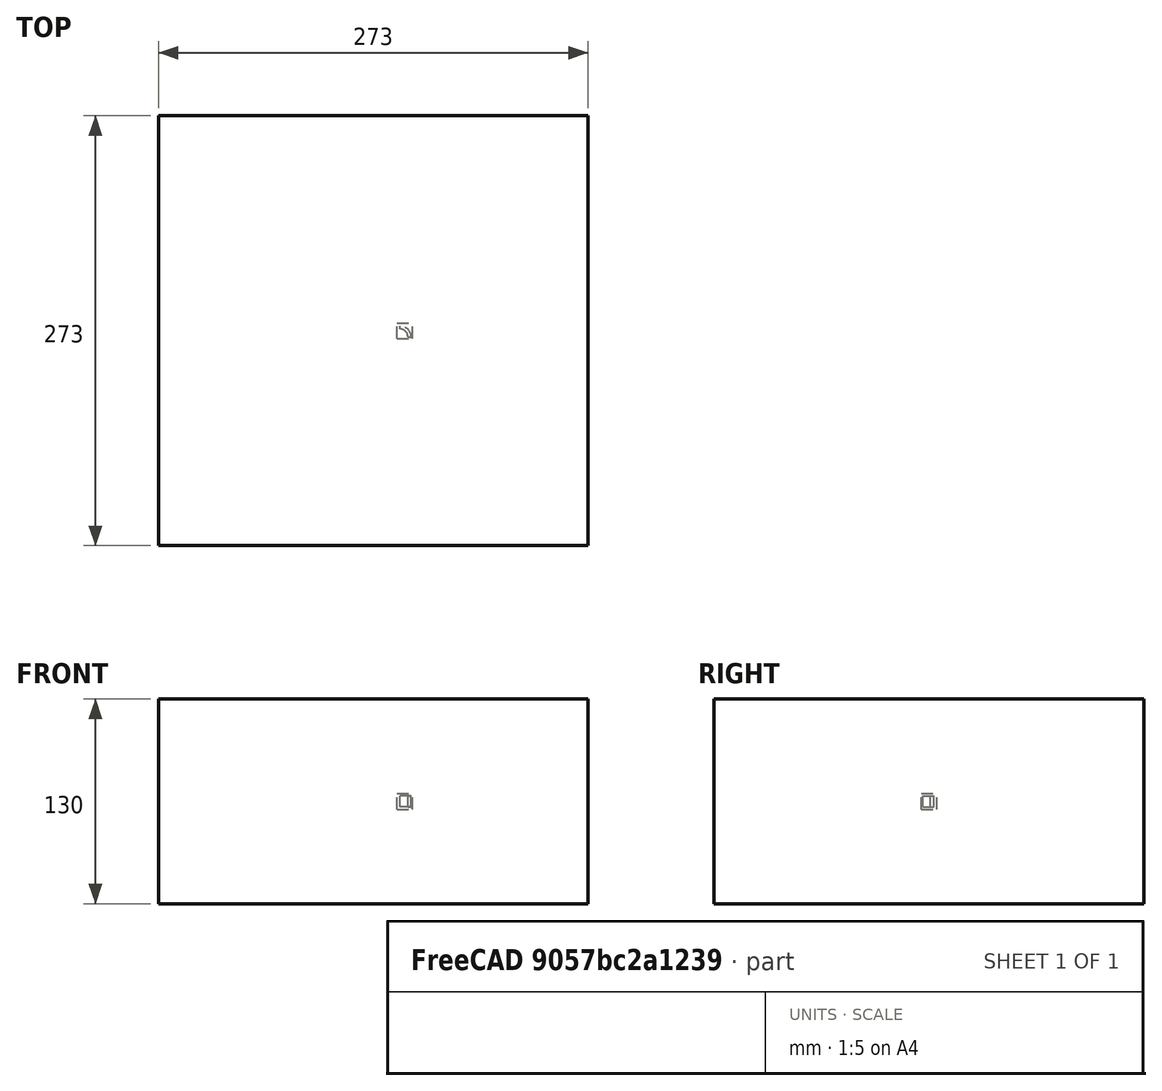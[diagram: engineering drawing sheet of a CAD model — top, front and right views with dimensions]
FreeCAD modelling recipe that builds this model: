
FCSTD DOCUMENT  (FreeCAD 1.0R39109 (Git))
Label: polarArray-of-Part-base-xformed
License: All rights reserved
LicenseURL: http://en.wikipedia.org/wiki/All_rights_reserved
objects: App::DocumentObjectGroupPython×1251, Part::FeaturePython×4, App::Part×4
note: 3 computed .brp shape members not serialized (recipe doc carries the construction recipe); baked Part::Feature solids carry a one-line shape summary decoded from their .brp

FEATURE [App::DocumentObjectGroupPython] HALFPI  # scripted group (container) (typed FeaturePython)
  name = HALFPI
  value = pi/2.
FEATURE [App::DocumentObjectGroupPython] PI  # scripted group (container) (typed FeaturePython)
  name = PI
  value = 1.*pi
FEATURE [App::DocumentObjectGroupPython] TWOPI  # scripted group (container) (typed FeaturePython)
  name = TWOPI
  value = 2.*pi
FEATURE [App::DocumentObjectGroupPython] Constants  # scripted group (container) (typed FeaturePython)
  Group = -> [HALFPI,PI,TWOPI]
FEATURE [App::DocumentObjectGroupPython] Variables  # scripted group (container) (typed FeaturePython)
FEATURE [App::DocumentObjectGroupPython] Quantities  # scripted group (container) (typed FeaturePython)
FEATURE [App::DocumentObjectGroupPython] Isotopes  # scripted group (container) (typed FeaturePython)
FEATURE [App::DocumentObjectGroupPython] Elements  # scripted group (container) (typed FeaturePython)
FEATURE [App::DocumentObjectGroupPython] Matrix  # scripted group (container) (typed FeaturePython)
FEATURE [App::DocumentObjectGroupPython] Surfaces  # scripted group (container) (typed FeaturePython)
FEATURE [App::DocumentObjectGroupPython] Opticals  # scripted group (container) (typed FeaturePython)
  Group = -> [Matrix,Surfaces]
FEATURE [App::DocumentObjectGroupPython] G4Isotopes  # scripted group (container) (typed FeaturePython)
FEATURE [App::DocumentObjectGroupPython] H_element  # scripted group (container) (typed FeaturePython)
  Z = 1
  atom_value = 1.008
  formula = H
  name = H_element
FEATURE [App::DocumentObjectGroupPython] He_element  # scripted group (container) (typed FeaturePython)
  Z = 2
  atom_value = 4.0026
  formula = He
  name = He_element
FEATURE [App::DocumentObjectGroupPython] Li_element  # scripted group (container) (typed FeaturePython)
  Z = 3
  atom_value = 6.94
  formula = Li
  name = Li_element
FEATURE [App::DocumentObjectGroupPython] Be_element  # scripted group (container) (typed FeaturePython)
  Z = 4
  atom_value = 9.01218
  formula = Be
  name = Be_element
FEATURE [App::DocumentObjectGroupPython] B_element  # scripted group (container) (typed FeaturePython)
  Z = 5
  atom_value = 10.81
  formula = B
  name = B_element
FEATURE [App::DocumentObjectGroupPython] C_element  # scripted group (container) (typed FeaturePython)
  Z = 6
  atom_value = 12.011
  formula = C
  name = C_element
FEATURE [App::DocumentObjectGroupPython] N_element  # scripted group (container) (typed FeaturePython)
  Z = 7
  atom_value = 14.007
  formula = N
  name = N_element
FEATURE [App::DocumentObjectGroupPython] O_element  # scripted group (container) (typed FeaturePython)
  Z = 8
  atom_value = 15.999
  formula = O
  name = O_element
FEATURE [App::DocumentObjectGroupPython] F_element  # scripted group (container) (typed FeaturePython)
  Z = 9
  atom_value = 18.9984
  formula = F
  name = F_element
FEATURE [App::DocumentObjectGroupPython] Ne_element  # scripted group (container) (typed FeaturePython)
  Z = 10
  atom_value = 20.1797
  formula = Ne
  name = Ne_element
FEATURE [App::DocumentObjectGroupPython] Na_element  # scripted group (container) (typed FeaturePython)
  Z = 11
  atom_value = 22.9898
  formula = Na
  name = Na_element
FEATURE [App::DocumentObjectGroupPython] Mg_element  # scripted group (container) (typed FeaturePython)
  Z = 12
  atom_value = 24.305
  formula = Mg
  name = Mg_element
FEATURE [App::DocumentObjectGroupPython] Al_element  # scripted group (container) (typed FeaturePython)
  Z = 13
  atom_value = 26.9815
  formula = Al
  name = Al_element
FEATURE [App::DocumentObjectGroupPython] Si_element  # scripted group (container) (typed FeaturePython)
  Z = 14
  atom_value = 28.085
  formula = Si
  name = Si_element
FEATURE [App::DocumentObjectGroupPython] P_element  # scripted group (container) (typed FeaturePython)
  Z = 15
  atom_value = 30.9738
  formula = P
  name = P_element
FEATURE [App::DocumentObjectGroupPython] S_element  # scripted group (container) (typed FeaturePython)
  Z = 16
  atom_value = 32.06
  formula = S
  name = S_element
FEATURE [App::DocumentObjectGroupPython] Cl_element  # scripted group (container) (typed FeaturePython)
  Z = 17
  atom_value = 35.45
  formula = Cl
  name = Cl_element
FEATURE [App::DocumentObjectGroupPython] Ar_element  # scripted group (container) (typed FeaturePython)
  Z = 18
  atom_value = 39.95
  formula = Ar
  name = Ar_element
FEATURE [App::DocumentObjectGroupPython] K_element  # scripted group (container) (typed FeaturePython)
  Z = 19
  atom_value = 39.0983
  formula = K
  name = K_element
FEATURE [App::DocumentObjectGroupPython] Ca_element  # scripted group (container) (typed FeaturePython)
  Z = 20
  atom_value = 40.078
  formula = Ca
  name = Ca_element
FEATURE [App::DocumentObjectGroupPython] Sc_element  # scripted group (container) (typed FeaturePython)
  Z = 21
  atom_value = 44.9559
  formula = Sc
  name = Sc_element
FEATURE [App::DocumentObjectGroupPython] Ti_element  # scripted group (container) (typed FeaturePython)
  Z = 22
  atom_value = 47.867
  formula = Ti
  name = Ti_element
FEATURE [App::DocumentObjectGroupPython] V_element  # scripted group (container) (typed FeaturePython)
  Z = 23
  atom_value = 50.9415
  formula = V
  name = V_element
FEATURE [App::DocumentObjectGroupPython] Cr_element  # scripted group (container) (typed FeaturePython)
  Z = 24
  atom_value = 51.9961
  formula = Cr
  name = Cr_element
FEATURE [App::DocumentObjectGroupPython] Mn_element  # scripted group (container) (typed FeaturePython)
  Z = 25
  atom_value = 54.938
  formula = Mn
  name = Mn_element
FEATURE [App::DocumentObjectGroupPython] Fe_element  # scripted group (container) (typed FeaturePython)
  Z = 26
  atom_value = 55.845
  formula = Fe
  name = Fe_element
FEATURE [App::DocumentObjectGroupPython] Co_element  # scripted group (container) (typed FeaturePython)
  Z = 27
  atom_value = 58.9332
  formula = Co
  name = Co_element
FEATURE [App::DocumentObjectGroupPython] Ni_element  # scripted group (container) (typed FeaturePython)
  Z = 28
  atom_value = 58.6934
  formula = Ni
  name = Ni_element
FEATURE [App::DocumentObjectGroupPython] Cu_element  # scripted group (container) (typed FeaturePython)
  Z = 29
  atom_value = 63.546
  formula = Cu
  name = Cu_element
FEATURE [App::DocumentObjectGroupPython] Zn_element  # scripted group (container) (typed FeaturePython)
  Z = 30
  atom_value = 65.38
  formula = Zn
  name = Zn_element
FEATURE [App::DocumentObjectGroupPython] Ga_element  # scripted group (container) (typed FeaturePython)
  Z = 31
  atom_value = 69.723
  formula = Ga
  name = Ga_element
FEATURE [App::DocumentObjectGroupPython] Ge_element  # scripted group (container) (typed FeaturePython)
  Z = 32
  atom_value = 72.63
  formula = Ge
  name = Ge_element
FEATURE [App::DocumentObjectGroupPython] As_element  # scripted group (container) (typed FeaturePython)
  Z = 33
  atom_value = 74.9216
  formula = As
  name = As_element
FEATURE [App::DocumentObjectGroupPython] Se_element  # scripted group (container) (typed FeaturePython)
  Z = 34
  atom_value = 78.971
  formula = Se
  name = Se_element
FEATURE [App::DocumentObjectGroupPython] Br_element  # scripted group (container) (typed FeaturePython)
  Z = 35
  atom_value = 79.904
  formula = Br
  name = Br_element
FEATURE [App::DocumentObjectGroupPython] Kr_element  # scripted group (container) (typed FeaturePython)
  Z = 36
  atom_value = 83.798
  formula = Kr
  name = Kr_element
FEATURE [App::DocumentObjectGroupPython] Rb_element  # scripted group (container) (typed FeaturePython)
  Z = 37
  atom_value = 85.4678
  formula = Rb
  name = Rb_element
FEATURE [App::DocumentObjectGroupPython] Sr_element  # scripted group (container) (typed FeaturePython)
  Z = 38
  atom_value = 87.62
  formula = Sr
  name = Sr_element
FEATURE [App::DocumentObjectGroupPython] Y_element  # scripted group (container) (typed FeaturePython)
  Z = 39
  atom_value = 88.9058
  formula = Y
  name = Y_element
FEATURE [App::DocumentObjectGroupPython] Zr_element  # scripted group (container) (typed FeaturePython)
  Z = 40
  atom_value = 91.224
  formula = Zr
  name = Zr_element
FEATURE [App::DocumentObjectGroupPython] Nb_element  # scripted group (container) (typed FeaturePython)
  Z = 41
  atom_value = 92.9064
  formula = Nb
  name = Nb_element
FEATURE [App::DocumentObjectGroupPython] Mo_element  # scripted group (container) (typed FeaturePython)
  Z = 42
  atom_value = 95.95
  formula = Mo
  name = Mo_element
FEATURE [App::DocumentObjectGroupPython] Tc_element  # scripted group (container) (typed FeaturePython)
  Z = 43
  atom_value = 97
  formula = Tc
  name = Tc_element
FEATURE [App::DocumentObjectGroupPython] Ru_element  # scripted group (container) (typed FeaturePython)
  Z = 44
  atom_value = 101.07
  formula = Ru
  name = Ru_element
FEATURE [App::DocumentObjectGroupPython] Rh_element  # scripted group (container) (typed FeaturePython)
  Z = 45
  atom_value = 102.905
  formula = Rh
  name = Rh_element
FEATURE [App::DocumentObjectGroupPython] Pd_element  # scripted group (container) (typed FeaturePython)
  Z = 46
  atom_value = 106.42
  formula = Pd
  name = Pd_element
FEATURE [App::DocumentObjectGroupPython] Ag_element  # scripted group (container) (typed FeaturePython)
  Z = 47
  atom_value = 107.868
  formula = Ag
  name = Ag_element
FEATURE [App::DocumentObjectGroupPython] Cd_element  # scripted group (container) (typed FeaturePython)
  Z = 48
  atom_value = 112.414
  formula = Cd
  name = Cd_element
FEATURE [App::DocumentObjectGroupPython] In_element  # scripted group (container) (typed FeaturePython)
  Z = 49
  atom_value = 114.818
  formula = In
  name = In_element
FEATURE [App::DocumentObjectGroupPython] Sn_element  # scripted group (container) (typed FeaturePython)
  Z = 50
  atom_value = 118.71
  formula = Sn
  name = Sn_element
FEATURE [App::DocumentObjectGroupPython] Sb_element  # scripted group (container) (typed FeaturePython)
  Z = 51
  atom_value = 121.76
  formula = Sb
  name = Sb_element
FEATURE [App::DocumentObjectGroupPython] Te_element  # scripted group (container) (typed FeaturePython)
  Z = 52
  atom_value = 127.6
  formula = Te
  name = Te_element
FEATURE [App::DocumentObjectGroupPython] I_element  # scripted group (container) (typed FeaturePython)
  Z = 53
  atom_value = 126.904
  formula = I
  name = I_element
FEATURE [App::DocumentObjectGroupPython] Xe_element  # scripted group (container) (typed FeaturePython)
  Z = 54
  atom_value = 131.293
  formula = Xe
  name = Xe_element
FEATURE [App::DocumentObjectGroupPython] Cs_element  # scripted group (container) (typed FeaturePython)
  Z = 55
  atom_value = 132.905
  formula = Cs
  name = Cs_element
FEATURE [App::DocumentObjectGroupPython] Ba_element  # scripted group (container) (typed FeaturePython)
  Z = 56
  atom_value = 137.327
  formula = Ba
  name = Ba_element
FEATURE [App::DocumentObjectGroupPython] La_element  # scripted group (container) (typed FeaturePython)
  Z = 57
  atom_value = 138.905
  formula = La
  name = La_element
FEATURE [App::DocumentObjectGroupPython] Ce_element  # scripted group (container) (typed FeaturePython)
  Z = 58
  atom_value = 140.116
  formula = Ce
  name = Ce_element
FEATURE [App::DocumentObjectGroupPython] Pr_element  # scripted group (container) (typed FeaturePython)
  Z = 59
  atom_value = 140.908
  formula = Pr
  name = Pr_element
FEATURE [App::DocumentObjectGroupPython] Nd_element  # scripted group (container) (typed FeaturePython)
  Z = 60
  atom_value = 144.242
  formula = Nd
  name = Nd_element
FEATURE [App::DocumentObjectGroupPython] Pm_element  # scripted group (container) (typed FeaturePython)
  Z = 61
  atom_value = 145
  formula = Pm
  name = Pm_element
FEATURE [App::DocumentObjectGroupPython] Sm_element  # scripted group (container) (typed FeaturePython)
  Z = 62
  atom_value = 150.36
  formula = Sm
  name = Sm_element
FEATURE [App::DocumentObjectGroupPython] Eu_element  # scripted group (container) (typed FeaturePython)
  Z = 63
  atom_value = 151.964
  formula = Eu
  name = Eu_element
FEATURE [App::DocumentObjectGroupPython] Gd_element  # scripted group (container) (typed FeaturePython)
  Z = 64
  atom_value = 157.25
  formula = Gd
  name = Gd_element
FEATURE [App::DocumentObjectGroupPython] Tb_element  # scripted group (container) (typed FeaturePython)
  Z = 65
  atom_value = 158.925
  formula = Tb
  name = Tb_element
FEATURE [App::DocumentObjectGroupPython] Dy_element  # scripted group (container) (typed FeaturePython)
  Z = 66
  atom_value = 162.5
  formula = Dy
  name = Dy_element
FEATURE [App::DocumentObjectGroupPython] Ho_element  # scripted group (container) (typed FeaturePython)
  Z = 67
  atom_value = 164.93
  formula = Ho
  name = Ho_element
FEATURE [App::DocumentObjectGroupPython] Er_element  # scripted group (container) (typed FeaturePython)
  Z = 68
  atom_value = 167.259
  formula = Er
  name = Er_element
FEATURE [App::DocumentObjectGroupPython] Tm_element  # scripted group (container) (typed FeaturePython)
  Z = 69
  atom_value = 168.934
  formula = Tm
  name = Tm_element
FEATURE [App::DocumentObjectGroupPython] Yb_element  # scripted group (container) (typed FeaturePython)
  Z = 70
  atom_value = 173.045
  formula = Yb
  name = Yb_element
FEATURE [App::DocumentObjectGroupPython] Lu_element  # scripted group (container) (typed FeaturePython)
  Z = 71
  atom_value = 174.967
  formula = Lu
  name = Lu_element
FEATURE [App::DocumentObjectGroupPython] Hf_element  # scripted group (container) (typed FeaturePython)
  Z = 72
  atom_value = 178.49
  formula = Hf
  name = Hf_element
FEATURE [App::DocumentObjectGroupPython] Ta_element  # scripted group (container) (typed FeaturePython)
  Z = 73
  atom_value = 180.948
  formula = Ta
  name = Ta_element
FEATURE [App::DocumentObjectGroupPython] W_element  # scripted group (container) (typed FeaturePython)
  Z = 74
  atom_value = 183.84
  formula = W
  name = W_element
FEATURE [App::DocumentObjectGroupPython] Re_element  # scripted group (container) (typed FeaturePython)
  Z = 75
  atom_value = 186.207
  formula = Re
  name = Re_element
FEATURE [App::DocumentObjectGroupPython] Os_element  # scripted group (container) (typed FeaturePython)
  Z = 76
  atom_value = 190.23
  formula = Os
  name = Os_element
FEATURE [App::DocumentObjectGroupPython] Ir_element  # scripted group (container) (typed FeaturePython)
  Z = 77
  atom_value = 192.217
  formula = Ir
  name = Ir_element
FEATURE [App::DocumentObjectGroupPython] Pt_element  # scripted group (container) (typed FeaturePython)
  Z = 78
  atom_value = 195.084
  formula = Pt
  name = Pt_element
FEATURE [App::DocumentObjectGroupPython] Au_element  # scripted group (container) (typed FeaturePython)
  Z = 79
  atom_value = 196.967
  formula = Au
  name = Au_element
FEATURE [App::DocumentObjectGroupPython] Hg_element  # scripted group (container) (typed FeaturePython)
  Z = 80
  atom_value = 200.592
  formula = Hg
  name = Hg_element
FEATURE [App::DocumentObjectGroupPython] Tl_element  # scripted group (container) (typed FeaturePython)
  Z = 81
  atom_value = 204.38
  formula = Tl
  name = Tl_element
FEATURE [App::DocumentObjectGroupPython] Pb_element  # scripted group (container) (typed FeaturePython)
  Z = 82
  atom_value = 207.2
  formula = Pb
  name = Pb_element
FEATURE [App::DocumentObjectGroupPython] Bi_element  # scripted group (container) (typed FeaturePython)
  Z = 83
  atom_value = 208.98
  formula = Bi
  name = Bi_element
FEATURE [App::DocumentObjectGroupPython] Po_element  # scripted group (container) (typed FeaturePython)
  Z = 84
  atom_value = 209
  formula = Po
  name = Po_element
FEATURE [App::DocumentObjectGroupPython] At_element  # scripted group (container) (typed FeaturePython)
  Z = 85
  atom_value = 210
  formula = At
  name = At_element
FEATURE [App::DocumentObjectGroupPython] Rn_element  # scripted group (container) (typed FeaturePython)
  Z = 86
  atom_value = 222
  formula = Rn
  name = Rn_element
FEATURE [App::DocumentObjectGroupPython] Fr_element  # scripted group (container) (typed FeaturePython)
  Z = 87
  atom_value = 223
  formula = Fr
  name = Fr_element
FEATURE [App::DocumentObjectGroupPython] Ra_element  # scripted group (container) (typed FeaturePython)
  Z = 88
  atom_value = 226
  formula = Ra
  name = Ra_element
FEATURE [App::DocumentObjectGroupPython] Ac_element  # scripted group (container) (typed FeaturePython)
  Z = 89
  atom_value = 227
  formula = Ac
  name = Ac_element
FEATURE [App::DocumentObjectGroupPython] Th_element  # scripted group (container) (typed FeaturePython)
  Z = 90
  atom_value = 232.038
  formula = Th
  name = Th_element
FEATURE [App::DocumentObjectGroupPython] Pa_element  # scripted group (container) (typed FeaturePython)
  Z = 91
  atom_value = 231.036
  formula = Pa
  name = Pa_element
FEATURE [App::DocumentObjectGroupPython] U_element  # scripted group (container) (typed FeaturePython)
  Z = 92
  atom_value = 238.029
  formula = U
  name = U_element
FEATURE [App::DocumentObjectGroupPython] Np_element  # scripted group (container) (typed FeaturePython)
  Z = 93
  atom_value = 237
  formula = Np
  name = Np_element
FEATURE [App::DocumentObjectGroupPython] Pu_element  # scripted group (container) (typed FeaturePython)
  Z = 94
  atom_value = 244
  formula = Pu
  name = Pu_element
FEATURE [App::DocumentObjectGroupPython] Am_element  # scripted group (container) (typed FeaturePython)
  Z = 95
  atom_value = 243
  formula = Am
  name = Am_element
FEATURE [App::DocumentObjectGroupPython] Cm_element  # scripted group (container) (typed FeaturePython)
  Z = 96
  atom_value = 247
  formula = Cm
  name = Cm_element
FEATURE [App::DocumentObjectGroupPython] Bk_element  # scripted group (container) (typed FeaturePython)
  Z = 97
  atom_value = 247
  formula = Bk
  name = Bk_element
FEATURE [App::DocumentObjectGroupPython] Cf_element  # scripted group (container) (typed FeaturePython)
  Z = 98
  atom_value = 251
  formula = Cf
  name = Cf_element
FEATURE [App::DocumentObjectGroupPython] G4Elements  # scripted group (container) (typed FeaturePython)
  Group = -> [H_element,He_element,Li_element,Be_element,B_element,C_element,N_element,O_element,F_element,Ne_element,Na_element,Mg_element,Al_element,Si_element,P_element,S_element,Cl_element,Ar_element,K_element,Ca_element,Sc_element,Ti_element,V_element,Cr_element,Mn_element,Fe_element,Co_element,Ni_element,Cu_element,Zn_element,Ga_element,Ge_element,As_element,Se_element,Br_element,Kr_element,Rb_element,+61 more]
FEATURE [App::DocumentObjectGroupPython] H_element001  label="H_element : 0.101"  # scripted group (container) (typed FeaturePython)
  n = 0.101327
FEATURE [App::DocumentObjectGroupPython] C_element001  label="C_element : 0.775"  # scripted group (container) (typed FeaturePython)
  n = 0.7755
FEATURE [App::DocumentObjectGroupPython] N_element001  label="N_element : 0.035"  # scripted group (container) (typed FeaturePython)
  n = 0.035057
FEATURE [App::DocumentObjectGroupPython] O_element001  label="O_element : 0.052"  # scripted group (container) (typed FeaturePython)
  n = 0.0523159
FEATURE [App::DocumentObjectGroupPython] F_element001  label="F_element : 0.017"  # scripted group (container) (typed FeaturePython)
  n = 0.017422
FEATURE [App::DocumentObjectGroupPython] Ca_element001  label="Ca_element : 0.018"  # scripted group (container) (typed FeaturePython)
  n = 0.018378
FEATURE [App::DocumentObjectGroupPython] G4_A_150_TISSUE  label="G4_A-150_TISSUE"  # scripted group (container) (typed FeaturePython)
  Dunit = g/cm3
  Dvalue = 1.127
  Group = -> [H_element001,C_element001,N_element001,O_element001,F_element001,Ca_element001]
  conduct = 2
  density = 1
  expand = 3
  formula = G4_A-150_TISSUE
  name = G4_A-150_TISSUE
  specific = 4
FEATURE [App::DocumentObjectGroupPython] C_element002  label="C_element : 3"  # scripted group (container) (typed FeaturePython)
  n = 3
  ref = C_element
FEATURE [App::DocumentObjectGroupPython] H_element002  label="H_element : 6"  # scripted group (container) (typed FeaturePython)
  n = 6
  ref = H_element
FEATURE [App::DocumentObjectGroupPython] O_element002  label="O_element : 1"  # scripted group (container) (typed FeaturePython)
  n = 1
  ref = O_element
FEATURE [App::DocumentObjectGroupPython] G4_ACETONE  # scripted group (container) (typed FeaturePython)
  Dunit = g/cm3
  Dvalue = 0.7899
  Group = -> [C_element002,H_element002,O_element002]
  conduct = 2
  density = 1
  expand = 3
  formula = G4_ACETONE
  name = G4_ACETONE
  specific = 4
FEATURE [App::DocumentObjectGroupPython] C_element003  label="C_element : 2"  # scripted group (container) (typed FeaturePython)
  n = 2
  ref = C_element
FEATURE [App::DocumentObjectGroupPython] H_element003  label="H_element : 2"  # scripted group (container) (typed FeaturePython)
  n = 2
  ref = H_element
FEATURE [App::DocumentObjectGroupPython] G4_ACETYLENE  # scripted group (container) (typed FeaturePython)
  Dunit = g/cm3
  Dvalue = 0.0010967
  Group = -> [C_element003,H_element003]
  conduct = 2
  density = 1
  expand = 3
  formula = G4_ACETYLENE
  name = G4_ACETYLENE
  specific = 4
FEATURE [App::DocumentObjectGroupPython] C_element004  label="C_element : 5"  # scripted group (container) (typed FeaturePython)
  n = 5
  ref = C_element
FEATURE [App::DocumentObjectGroupPython] H_element004  label="H_element : 5"  # scripted group (container) (typed FeaturePython)
  n = 5
  ref = H_element
FEATURE [App::DocumentObjectGroupPython] N_element002  label="N_element : 5"  # scripted group (container) (typed FeaturePython)
  n = 5
  ref = N_element
FEATURE [App::DocumentObjectGroupPython] G4_ADENINE  # scripted group (container) (typed FeaturePython)
  Dunit = g/cm3
  Dvalue = 1.6
  Group = -> [C_element004,H_element004,N_element002]
  conduct = 2
  density = 1
  expand = 3
  formula = G4_ADENINE
  name = G4_ADENINE
  specific = 4
FEATURE [App::DocumentObjectGroupPython] H_element005  label="H_element : 0.114"  # scripted group (container) (typed FeaturePython)
  n = 0.114
FEATURE [App::DocumentObjectGroupPython] C_element005  label="C_element : 0.598"  # scripted group (container) (typed FeaturePython)
  n = 0.598
FEATURE [App::DocumentObjectGroupPython] N_element003  label="N_element : 0.007"  # scripted group (container) (typed FeaturePython)
  n = 0.007
FEATURE [App::DocumentObjectGroupPython] O_element003  label="O_element : 0.278"  # scripted group (container) (typed FeaturePython)
  n = 0.278
FEATURE [App::DocumentObjectGroupPython] Na_element001  label="Na_element : 0.001"  # scripted group (container) (typed FeaturePython)
  n = 0.001
FEATURE [App::DocumentObjectGroupPython] S_element001  label="S_element : 0.001"  # scripted group (container) (typed FeaturePython)
  n = 0.001
FEATURE [App::DocumentObjectGroupPython] Cl_element001  label="Cl_element : 0.001"  # scripted group (container) (typed FeaturePython)
  n = 0.001
FEATURE [App::DocumentObjectGroupPython] G4_ADIPOSE_TISSUE_ICRP  # scripted group (container) (typed FeaturePython)
  Dunit = g/cm3
  Dvalue = 0.95
  Group = -> [H_element005,C_element005,N_element003,O_element003,Na_element001,S_element001,Cl_element001]
  conduct = 2
  density = 1
  expand = 3
  formula = G4_ADIPOSE_TISSUE_ICRP
  name = G4_ADIPOSE_TISSUE_ICRP
  specific = 4
FEATURE [App::DocumentObjectGroupPython] C_element006  label="C_element : 0.000"  # scripted group (container) (typed FeaturePython)
  n = 0.000124
FEATURE [App::DocumentObjectGroupPython] N_element004  label="N_element : 0.755"  # scripted group (container) (typed FeaturePython)
  n = 0.755268
FEATURE [App::DocumentObjectGroupPython] O_element004  label="O_element : 0.232"  # scripted group (container) (typed FeaturePython)
  n = 0.231781
FEATURE [App::DocumentObjectGroupPython] Ar_element001  label="Ar_element : 0.013"  # scripted group (container) (typed FeaturePython)
  n = 0.012827
FEATURE [App::DocumentObjectGroupPython] G4_AIR  # scripted group (container) (typed FeaturePython)
  Dunit = g/cm3
  Dvalue = 0.00120479
  Group = -> [C_element006,N_element004,O_element004,Ar_element001]
  conduct = 2
  density = 1
  expand = 3
  formula = G4_AIR
  name = G4_AIR
  specific = 4
FEATURE [App::DocumentObjectGroupPython] C_element007  label="C_element : 006"  # scripted group (container) (typed FeaturePython)
  n = 3
  ref = C_element
FEATURE [App::DocumentObjectGroupPython] H_element006  label="H_element : 7"  # scripted group (container) (typed FeaturePython)
  n = 7
  ref = H_element
FEATURE [App::DocumentObjectGroupPython] N_element005  label="N_element : 1"  # scripted group (container) (typed FeaturePython)
  n = 1
  ref = N_element
FEATURE [App::DocumentObjectGroupPython] O_element005  label="O_element : 2"  # scripted group (container) (typed FeaturePython)
  n = 2
  ref = O_element
FEATURE [App::DocumentObjectGroupPython] G4_ALANINE  # scripted group (container) (typed FeaturePython)
  Dunit = g/cm3
  Dvalue = 1.42
  Group = -> [C_element007,H_element006,N_element005,O_element005]
  conduct = 2
  density = 1
  expand = 3
  formula = G4_ALANINE
  name = G4_ALANINE
  specific = 4
FEATURE [App::DocumentObjectGroupPython] Al_element001  label="Al_element : 2"  # scripted group (container) (typed FeaturePython)
  n = 2
  ref = Al_element
FEATURE [App::DocumentObjectGroupPython] O_element006  label="O_element : 3"  # scripted group (container) (typed FeaturePython)
  n = 3
  ref = O_element
FEATURE [App::DocumentObjectGroupPython] G4_ALUMINUM_OXIDE  # scripted group (container) (typed FeaturePython)
  Dunit = g/cm3
  Dvalue = 3.97
  Group = -> [Al_element001,O_element006]
  conduct = 2
  density = 1
  expand = 3
  formula = G4_ALUMINUM_OXIDE
  name = G4_ALUMINUM_OXIDE
  specific = 4
FEATURE [App::DocumentObjectGroupPython] H_element007  label="H_element : 0.106"  # scripted group (container) (typed FeaturePython)
  n = 0.10593
FEATURE [App::DocumentObjectGroupPython] C_element008  label="C_element : 0.789"  # scripted group (container) (typed FeaturePython)
  n = 0.788974
FEATURE [App::DocumentObjectGroupPython] O_element007  label="O_element : 0.105"  # scripted group (container) (typed FeaturePython)
  n = 0.105096
FEATURE [App::DocumentObjectGroupPython] G4_AMBER  # scripted group (container) (typed FeaturePython)
  Dunit = g/cm3
  Dvalue = 1.1
  Group = -> [H_element007,C_element008,O_element007]
  conduct = 2
  density = 1
  expand = 3
  formula = G4_AMBER
  name = G4_AMBER
  specific = 4
FEATURE [App::DocumentObjectGroupPython] N_element006  label="N_element : 006"  # scripted group (container) (typed FeaturePython)
  n = 1
  ref = N_element
FEATURE [App::DocumentObjectGroupPython] H_element008  label="H_element : 3"  # scripted group (container) (typed FeaturePython)
  n = 3
  ref = H_element
FEATURE [App::DocumentObjectGroupPython] G4_AMMONIA  # scripted group (container) (typed FeaturePython)
  Dunit = g/cm3
  Dvalue = 0.000826019
  Group = -> [N_element006,H_element008]
  conduct = 2
  density = 1
  expand = 3
  formula = G4_AMMONIA
  name = G4_AMMONIA
  specific = 4
FEATURE [App::DocumentObjectGroupPython] C_element009  label="C_element : 6"  # scripted group (container) (typed FeaturePython)
  n = 6
  ref = C_element
FEATURE [App::DocumentObjectGroupPython] H_element009  label="H_element : 008"  # scripted group (container) (typed FeaturePython)
  n = 7
  ref = H_element
FEATURE [App::DocumentObjectGroupPython] N_element007  label="N_element : 007"  # scripted group (container) (typed FeaturePython)
  n = 1
  ref = N_element
FEATURE [App::DocumentObjectGroupPython] G4_ANILINE  # scripted group (container) (typed FeaturePython)
  Dunit = g/cm3
  Dvalue = 1.0235
  Group = -> [C_element009,H_element009,N_element007]
  conduct = 2
  density = 1
  expand = 3
  formula = G4_ANILINE
  name = G4_ANILINE
  specific = 4
FEATURE [App::DocumentObjectGroupPython] C_element010  label="C_element : 14"  # scripted group (container) (typed FeaturePython)
  n = 14
  ref = C_element
FEATURE [App::DocumentObjectGroupPython] H_element010  label="H_element : 10"  # scripted group (container) (typed FeaturePython)
  n = 10
  ref = H_element
FEATURE [App::DocumentObjectGroupPython] G4_ANTHRACENE  # scripted group (container) (typed FeaturePython)
  Dunit = g/cm3
  Dvalue = 1.283
  Group = -> [C_element010,H_element010]
  conduct = 2
  density = 1
  expand = 3
  formula = G4_ANTHRACENE
  name = G4_ANTHRACENE
  specific = 4
FEATURE [App::DocumentObjectGroupPython] H_element011  label="H_element : 0.065"  # scripted group (container) (typed FeaturePython)
  n = 0.0654709
FEATURE [App::DocumentObjectGroupPython] C_element011  label="C_element : 0.537"  # scripted group (container) (typed FeaturePython)
  n = 0.536944
FEATURE [App::DocumentObjectGroupPython] N_element008  label="N_element : 0.021"  # scripted group (container) (typed FeaturePython)
  n = 0.0215
FEATURE [App::DocumentObjectGroupPython] O_element008  label="O_element : 0.032"  # scripted group (container) (typed FeaturePython)
  n = 0.032085
FEATURE [App::DocumentObjectGroupPython] F_element002  label="F_element : 0.167"  # scripted group (container) (typed FeaturePython)
  n = 0.167411
FEATURE [App::DocumentObjectGroupPython] Ca_element002  label="Ca_element : 0.177"  # scripted group (container) (typed FeaturePython)
  n = 0.176589
FEATURE [App::DocumentObjectGroupPython] G4_B_100_BONE  label="G4_B-100_BONE"  # scripted group (container) (typed FeaturePython)
  Dunit = g/cm3
  Dvalue = 1.45
  Group = -> [H_element011,C_element011,N_element008,O_element008,F_element002,Ca_element002]
  conduct = 2
  density = 1
  expand = 3
  formula = G4_B-100_BONE
  name = G4_B-100_BONE
  specific = 4
FEATURE [App::DocumentObjectGroupPython] H_element012  label="H_element : 0.057"  # scripted group (container) (typed FeaturePython)
  n = 0.057441
FEATURE [App::DocumentObjectGroupPython] C_element012  label="C_element : 0.790"  # scripted group (container) (typed FeaturePython)
  n = 0.774591
FEATURE [App::DocumentObjectGroupPython] O_element009  label="O_element : 0.168"  # scripted group (container) (typed FeaturePython)
  n = 0.167968
FEATURE [App::DocumentObjectGroupPython] G4_BAKELITE  # scripted group (container) (typed FeaturePython)
  Dunit = g/cm3
  Dvalue = 1.25
  Group = -> [H_element012,C_element012,O_element009]
  conduct = 2
  density = 1
  expand = 3
  formula = G4_BAKELITE
  name = G4_BAKELITE
  specific = 4
FEATURE [App::DocumentObjectGroupPython] Ba_element001  label="Ba_element : 1"  # scripted group (container) (typed FeaturePython)
  n = 1
  ref = Ba_element
FEATURE [App::DocumentObjectGroupPython] F_element003  label="F_element : 2"  # scripted group (container) (typed FeaturePython)
  n = 2
  ref = F_element
FEATURE [App::DocumentObjectGroupPython] G4_BARIUM_FLUORIDE  # scripted group (container) (typed FeaturePython)
  Dunit = g/cm3
  Dvalue = 4.89
  Group = -> [Ba_element001,F_element003]
  conduct = 2
  density = 1
  expand = 3
  formula = G4_BARIUM_FLUORIDE
  name = G4_BARIUM_FLUORIDE
  specific = 4
FEATURE [App::DocumentObjectGroupPython] Ba_element002  label="Ba_element : 002"  # scripted group (container) (typed FeaturePython)
  n = 1
  ref = Ba_element
FEATURE [App::DocumentObjectGroupPython] S_element002  label="S_element : 1"  # scripted group (container) (typed FeaturePython)
  n = 1
  ref = S_element
FEATURE [App::DocumentObjectGroupPython] O_element010  label="O_element : 4"  # scripted group (container) (typed FeaturePython)
  n = 4
  ref = O_element
FEATURE [App::DocumentObjectGroupPython] G4_BARIUM_SULFATE  # scripted group (container) (typed FeaturePython)
  Dunit = g/cm3
  Dvalue = 4.5
  Group = -> [Ba_element002,S_element002,O_element010]
  conduct = 2
  density = 1
  expand = 3
  formula = G4_BARIUM_SULFATE
  name = G4_BARIUM_SULFATE
  specific = 4
FEATURE [App::DocumentObjectGroupPython] C_element013  label="C_element : 007"  # scripted group (container) (typed FeaturePython)
  n = 6
  ref = C_element
FEATURE [App::DocumentObjectGroupPython] H_element013  label="H_element : 009"  # scripted group (container) (typed FeaturePython)
  n = 6
  ref = H_element
FEATURE [App::DocumentObjectGroupPython] G4_BENZENE  # scripted group (container) (typed FeaturePython)
  Dunit = g/cm3
  Dvalue = 0.87865
  Group = -> [C_element013,H_element013]
  conduct = 2
  density = 1
  expand = 3
  formula = G4_BENZENE
  name = G4_BENZENE
  specific = 4
FEATURE [App::DocumentObjectGroupPython] Be_element001  label="Be_element : 1"  # scripted group (container) (typed FeaturePython)
  n = 1
  ref = Be_element
FEATURE [App::DocumentObjectGroupPython] O_element011  label="O_element : 005"  # scripted group (container) (typed FeaturePython)
  n = 1
  ref = O_element
FEATURE [App::DocumentObjectGroupPython] G4_BERYLLIUM_OXIDE  # scripted group (container) (typed FeaturePython)
  Dunit = g/cm3
  Dvalue = 3.01
  Group = -> [Be_element001,O_element011]
  conduct = 2
  density = 1
  expand = 3
  formula = G4_BERYLLIUM_OXIDE
  name = G4_BERYLLIUM_OXIDE
  specific = 4
FEATURE [App::DocumentObjectGroupPython] Bi_element001  label="Bi_element : 4"  # scripted group (container) (typed FeaturePython)
  n = 4
  ref = Bi_element
FEATURE [App::DocumentObjectGroupPython] Ge_element001  label="Ge_element : 3"  # scripted group (container) (typed FeaturePython)
  n = 3
  ref = Ge_element
FEATURE [App::DocumentObjectGroupPython] O_element012  label="O_element : 12"  # scripted group (container) (typed FeaturePython)
  n = 12
  ref = O_element
FEATURE [App::DocumentObjectGroupPython] G4_BGO  # scripted group (container) (typed FeaturePython)
  Dunit = g/cm3
  Dvalue = 7.13
  Group = -> [Bi_element001,Ge_element001,O_element012]
  conduct = 2
  density = 1
  expand = 3
  formula = G4_BGO
  name = G4_BGO
  specific = 4
FEATURE [App::DocumentObjectGroupPython] H_element014  label="H_element : 0.102"  # scripted group (container) (typed FeaturePython)
  n = 0.102
FEATURE [App::DocumentObjectGroupPython] C_element014  label="C_element : 0.110"  # scripted group (container) (typed FeaturePython)
  n = 0.11
FEATURE [App::DocumentObjectGroupPython] N_element009  label="N_element : 0.033"  # scripted group (container) (typed FeaturePython)
  n = 0.033
FEATURE [App::DocumentObjectGroupPython] O_element013  label="O_element : 0.745"  # scripted group (container) (typed FeaturePython)
  n = 0.745
FEATURE [App::DocumentObjectGroupPython] Na_element002  label="Na_element : 0.002"  # scripted group (container) (typed FeaturePython)
  n = 0.001
FEATURE [App::DocumentObjectGroupPython] P_element001  label="P_element : 0.001"  # scripted group (container) (typed FeaturePython)
  n = 0.001
FEATURE [App::DocumentObjectGroupPython] S_element003  label="S_element : 0.002"  # scripted group (container) (typed FeaturePython)
  n = 0.002
FEATURE [App::DocumentObjectGroupPython] Cl_element002  label="Cl_element : 0.003"  # scripted group (container) (typed FeaturePython)
  n = 0.003
FEATURE [App::DocumentObjectGroupPython] K_element001  label="K_element : 0.002"  # scripted group (container) (typed FeaturePython)
  n = 0.002
FEATURE [App::DocumentObjectGroupPython] Fe_element001  label="Fe_element : 0.001"  # scripted group (container) (typed FeaturePython)
  n = 0.001
FEATURE [App::DocumentObjectGroupPython] G4_BLOOD_ICRP  # scripted group (container) (typed FeaturePython)
  Dunit = g/cm3
  Dvalue = 1.06
  Group = -> [H_element014,C_element014,N_element009,O_element013,Na_element002,P_element001,S_element003,Cl_element002,K_element001,Fe_element001]
  conduct = 2
  density = 1
  expand = 3
  formula = G4_BLOOD_ICRP
  name = G4_BLOOD_ICRP
  specific = 4
FEATURE [App::DocumentObjectGroupPython] H_element015  label="H_element : 0.064"  # scripted group (container) (typed FeaturePython)
  n = 0.064
FEATURE [App::DocumentObjectGroupPython] C_element015  label="C_element : 0.278"  # scripted group (container) (typed FeaturePython)
  n = 0.278
FEATURE [App::DocumentObjectGroupPython] N_element010  label="N_element : 0.027"  # scripted group (container) (typed FeaturePython)
  n = 0.027
FEATURE [App::DocumentObjectGroupPython] O_element014  label="O_element : 0.410"  # scripted group (container) (typed FeaturePython)
  n = 0.41
FEATURE [App::DocumentObjectGroupPython] Mg_element001  label="Mg_element : 0.002"  # scripted group (container) (typed FeaturePython)
  n = 0.002
FEATURE [App::DocumentObjectGroupPython] P_element002  label="P_element : 0.070"  # scripted group (container) (typed FeaturePython)
  n = 0.07
FEATURE [App::DocumentObjectGroupPython] S_element004  label="S_element : 0.003"  # scripted group (container) (typed FeaturePython)
  n = 0.002
FEATURE [App::DocumentObjectGroupPython] Ca_element003  label="Ca_element : 0.147"  # scripted group (container) (typed FeaturePython)
  n = 0.147
FEATURE [App::DocumentObjectGroupPython] G4_BONE_COMPACT_ICRU  # scripted group (container) (typed FeaturePython)
  Dunit = g/cm3
  Dvalue = 1.85
  Group = -> [H_element015,C_element015,N_element010,O_element014,Mg_element001,P_element002,S_element004,Ca_element003]
  conduct = 2
  density = 1
  expand = 3
  formula = G4_BONE_COMPACT_ICRU
  name = G4_BONE_COMPACT_ICRU
  specific = 4
FEATURE [App::DocumentObjectGroupPython] H_element016  label="H_element : 0.034"  # scripted group (container) (typed FeaturePython)
  n = 0.034
FEATURE [App::DocumentObjectGroupPython] C_element016  label="C_element : 0.155"  # scripted group (container) (typed FeaturePython)
  n = 0.155
FEATURE [App::DocumentObjectGroupPython] N_element011  label="N_element : 0.042"  # scripted group (container) (typed FeaturePython)
  n = 0.042
FEATURE [App::DocumentObjectGroupPython] O_element015  label="O_element : 0.435"  # scripted group (container) (typed FeaturePython)
  n = 0.435
FEATURE [App::DocumentObjectGroupPython] Na_element003  label="Na_element : 0.003"  # scripted group (container) (typed FeaturePython)
  n = 0.001
FEATURE [App::DocumentObjectGroupPython] Mg_element002  label="Mg_element : 0.003"  # scripted group (container) (typed FeaturePython)
  n = 0.002
FEATURE [App::DocumentObjectGroupPython] P_element003  label="P_element : 0.103"  # scripted group (container) (typed FeaturePython)
  n = 0.103
FEATURE [App::DocumentObjectGroupPython] S_element005  label="S_element : 0.004"  # scripted group (container) (typed FeaturePython)
  n = 0.003
FEATURE [App::DocumentObjectGroupPython] Ca_element004  label="Ca_element : 0.225"  # scripted group (container) (typed FeaturePython)
  n = 0.225
FEATURE [App::DocumentObjectGroupPython] G4_BONE_CORTICAL_ICRP  # scripted group (container) (typed FeaturePython)
  Dunit = g/cm3
  Dvalue = 1.92
  Group = -> [H_element016,C_element016,N_element011,O_element015,Na_element003,Mg_element002,P_element003,S_element005,Ca_element004]
  conduct = 2
  density = 1
  expand = 3
  formula = G4_BONE_CORTICAL_ICRP
  name = G4_BONE_CORTICAL_ICRP
  specific = 4
FEATURE [App::DocumentObjectGroupPython] B_element001  label="B_element : 4"  # scripted group (container) (typed FeaturePython)
  n = 4
  ref = B_element
FEATURE [App::DocumentObjectGroupPython] C_element017  label="C_element : 1"  # scripted group (container) (typed FeaturePython)
  n = 1
  ref = C_element
FEATURE [App::DocumentObjectGroupPython] G4_BORON_CARBIDE  # scripted group (container) (typed FeaturePython)
  Dunit = g/cm3
  Dvalue = 2.52
  Group = -> [B_element001,C_element017]
  conduct = 2
  density = 1
  expand = 3
  formula = G4_BORON_CARBIDE
  name = G4_BORON_CARBIDE
  specific = 4
FEATURE [App::DocumentObjectGroupPython] B_element002  label="B_element : 2"  # scripted group (container) (typed FeaturePython)
  n = 2
  ref = B_element
FEATURE [App::DocumentObjectGroupPython] O_element016  label="O_element : 006"  # scripted group (container) (typed FeaturePython)
  n = 3
  ref = O_element
FEATURE [App::DocumentObjectGroupPython] G4_BORON_OXIDE  # scripted group (container) (typed FeaturePython)
  Dunit = g/cm3
  Dvalue = 1.812
  Group = -> [B_element002,O_element016]
  conduct = 2
  density = 1
  expand = 3
  formula = G4_BORON_OXIDE
  name = G4_BORON_OXIDE
  specific = 4
FEATURE [App::DocumentObjectGroupPython] H_element017  label="H_element : 0.107"  # scripted group (container) (typed FeaturePython)
  n = 0.107
FEATURE [App::DocumentObjectGroupPython] C_element018  label="C_element : 0.145"  # scripted group (container) (typed FeaturePython)
  n = 0.145
FEATURE [App::DocumentObjectGroupPython] N_element012  label="N_element : 0.022"  # scripted group (container) (typed FeaturePython)
  n = 0.022
FEATURE [App::DocumentObjectGroupPython] O_element017  label="O_element : 0.712"  # scripted group (container) (typed FeaturePython)
  n = 0.712
FEATURE [App::DocumentObjectGroupPython] Na_element004  label="Na_element : 0.004"  # scripted group (container) (typed FeaturePython)
  n = 0.002
FEATURE [App::DocumentObjectGroupPython] P_element004  label="P_element : 0.004"  # scripted group (container) (typed FeaturePython)
  n = 0.004
FEATURE [App::DocumentObjectGroupPython] S_element006  label="S_element : 0.005"  # scripted group (container) (typed FeaturePython)
  n = 0.002
FEATURE [App::DocumentObjectGroupPython] Cl_element003  label="Cl_element : 0.004"  # scripted group (container) (typed FeaturePython)
  n = 0.003
FEATURE [App::DocumentObjectGroupPython] K_element002  label="K_element : 0.003"  # scripted group (container) (typed FeaturePython)
  n = 0.003
FEATURE [App::DocumentObjectGroupPython] G4_BRAIN_ICRP  # scripted group (container) (typed FeaturePython)
  Dunit = g/cm3
  Dvalue = 1.04
  Group = -> [H_element017,C_element018,N_element012,O_element017,Na_element004,P_element004,S_element006,Cl_element003,K_element002]
  conduct = 2
  density = 1
  expand = 3
  formula = G4_BRAIN_ICRP
  name = G4_BRAIN_ICRP
  specific = 4
FEATURE [App::DocumentObjectGroupPython] C_element019  label="C_element : 4"  # scripted group (container) (typed FeaturePython)
  n = 4
  ref = C_element
FEATURE [App::DocumentObjectGroupPython] H_element018  label="H_element : 010"  # scripted group (container) (typed FeaturePython)
  n = 10
  ref = H_element
FEATURE [App::DocumentObjectGroupPython] G4_BUTANE  # scripted group (container) (typed FeaturePython)
  Dunit = g/cm3
  Dvalue = 0.00249343
  Group = -> [C_element019,H_element018]
  conduct = 2
  density = 1
  expand = 3
  formula = G4_BUTANE
  name = G4_BUTANE
  specific = 4
FEATURE [App::DocumentObjectGroupPython] C_element020  label="C_element : 008"  # scripted group (container) (typed FeaturePython)
  n = 4
  ref = C_element
FEATURE [App::DocumentObjectGroupPython] H_element019  label="H_element : 011"  # scripted group (container) (typed FeaturePython)
  n = 10
  ref = H_element
FEATURE [App::DocumentObjectGroupPython] O_element018  label="O_element : 007"  # scripted group (container) (typed FeaturePython)
  n = 1
  ref = O_element
FEATURE [App::DocumentObjectGroupPython] G4_N_BUTYL_ALCOHOL  label="G4_N-BUTYL_ALCOHOL"  # scripted group (container) (typed FeaturePython)
  Dunit = g/cm3
  Dvalue = 0.8098
  Group = -> [C_element020,H_element019,O_element018]
  conduct = 2
  density = 1
  expand = 3
  formula = G4_N-BUTYL_ALCOHOL
  name = G4_N-BUTYL_ALCOHOL
  specific = 4
FEATURE [App::DocumentObjectGroupPython] H_element020  label="H_element : 0.025"  # scripted group (container) (typed FeaturePython)
  n = 0.02468
FEATURE [App::DocumentObjectGroupPython] C_element021  label="C_element : 0.502"  # scripted group (container) (typed FeaturePython)
  n = 0.501611
FEATURE [App::DocumentObjectGroupPython] O_element019  label="O_element : 0.005"  # scripted group (container) (typed FeaturePython)
  n = 0.004527
FEATURE [App::DocumentObjectGroupPython] F_element004  label="F_element : 0.465"  # scripted group (container) (typed FeaturePython)
  n = 0.465209
FEATURE [App::DocumentObjectGroupPython] Si_element001  label="Si_element : 0.004"  # scripted group (container) (typed FeaturePython)
  n = 0.003973
FEATURE [App::DocumentObjectGroupPython] G4_C_552  label="G4_C-552"  # scripted group (container) (typed FeaturePython)
  Dunit = g/cm3
  Dvalue = 1.76
  Group = -> [H_element020,C_element021,O_element019,F_element004,Si_element001]
  conduct = 2
  density = 1
  expand = 3
  formula = G4_C-552
  name = G4_C-552
  specific = 4
FEATURE [App::DocumentObjectGroupPython] Cd_element001  label="Cd_element : 1"  # scripted group (container) (typed FeaturePython)
  n = 1
  ref = Cd_element
FEATURE [App::DocumentObjectGroupPython] Te_element001  label="Te_element : 1"  # scripted group (container) (typed FeaturePython)
  n = 1
  ref = Te_element
FEATURE [App::DocumentObjectGroupPython] G4_CADMIUM_TELLURIDE  # scripted group (container) (typed FeaturePython)
  Dunit = g/cm3
  Dvalue = 6.2
  Group = -> [Cd_element001,Te_element001]
  conduct = 2
  density = 1
  expand = 3
  formula = G4_CADMIUM_TELLURIDE
  name = G4_CADMIUM_TELLURIDE
  specific = 4
FEATURE [App::DocumentObjectGroupPython] Cd_element002  label="Cd_element : 002"  # scripted group (container) (typed FeaturePython)
  n = 1
  ref = Cd_element
FEATURE [App::DocumentObjectGroupPython] W_element001  label="W_element : 1"  # scripted group (container) (typed FeaturePython)
  n = 1
  ref = W_element
FEATURE [App::DocumentObjectGroupPython] O_element020  label="O_element : 008"  # scripted group (container) (typed FeaturePython)
  n = 4
  ref = O_element
FEATURE [App::DocumentObjectGroupPython] G4_CADMIUM_TUNGSTATE  # scripted group (container) (typed FeaturePython)
  Dunit = g/cm3
  Dvalue = 7.9
  Group = -> [Cd_element002,W_element001,O_element020]
  conduct = 2
  density = 1
  expand = 3
  formula = G4_CADMIUM_TUNGSTATE
  name = G4_CADMIUM_TUNGSTATE
  specific = 4
FEATURE [App::DocumentObjectGroupPython] Ca_element005  label="Ca_element : 1"  # scripted group (container) (typed FeaturePython)
  n = 1
  ref = Ca_element
FEATURE [App::DocumentObjectGroupPython] C_element022  label="C_element : 009"  # scripted group (container) (typed FeaturePython)
  n = 1
  ref = C_element
FEATURE [App::DocumentObjectGroupPython] O_element021  label="O_element : 009"  # scripted group (container) (typed FeaturePython)
  n = 3
  ref = O_element
FEATURE [App::DocumentObjectGroupPython] G4_CALCIUM_CARBONATE  # scripted group (container) (typed FeaturePython)
  Dunit = g/cm3
  Dvalue = 2.8
  Group = -> [Ca_element005,C_element022,O_element021]
  conduct = 2
  density = 1
  expand = 3
  formula = G4_CALCIUM_CARBONATE
  name = G4_CALCIUM_CARBONATE
  specific = 4
FEATURE [App::DocumentObjectGroupPython] Ca_element006  label="Ca_element : 002"  # scripted group (container) (typed FeaturePython)
  n = 1
  ref = Ca_element
FEATURE [App::DocumentObjectGroupPython] F_element005  label="F_element : 003"  # scripted group (container) (typed FeaturePython)
  n = 2
  ref = F_element
FEATURE [App::DocumentObjectGroupPython] G4_CALCIUM_FLUORIDE  # scripted group (container) (typed FeaturePython)
  Dunit = g/cm3
  Dvalue = 3.18
  Group = -> [Ca_element006,F_element005]
  conduct = 2
  density = 1
  expand = 3
  formula = G4_CALCIUM_FLUORIDE
  name = G4_CALCIUM_FLUORIDE
  specific = 4
FEATURE [App::DocumentObjectGroupPython] Ca_element007  label="Ca_element : 003"  # scripted group (container) (typed FeaturePython)
  n = 1
  ref = Ca_element
FEATURE [App::DocumentObjectGroupPython] O_element022  label="O_element : 010"  # scripted group (container) (typed FeaturePython)
  n = 1
  ref = O_element
FEATURE [App::DocumentObjectGroupPython] G4_CALCIUM_OXIDE  # scripted group (container) (typed FeaturePython)
  Dunit = g/cm3
  Dvalue = 3.3
  Group = -> [Ca_element007,O_element022]
  conduct = 2
  density = 1
  expand = 3
  formula = G4_CALCIUM_OXIDE
  name = G4_CALCIUM_OXIDE
  specific = 4
FEATURE [App::DocumentObjectGroupPython] Ca_element008  label="Ca_element : 004"  # scripted group (container) (typed FeaturePython)
  n = 1
  ref = Ca_element
FEATURE [App::DocumentObjectGroupPython] S_element007  label="S_element : 002"  # scripted group (container) (typed FeaturePython)
  n = 1
  ref = S_element
FEATURE [App::DocumentObjectGroupPython] O_element023  label="O_element : 011"  # scripted group (container) (typed FeaturePython)
  n = 4
  ref = O_element
FEATURE [App::DocumentObjectGroupPython] G4_CALCIUM_SULFATE  # scripted group (container) (typed FeaturePython)
  Dunit = g/cm3
  Dvalue = 2.96
  Group = -> [Ca_element008,S_element007,O_element023]
  conduct = 2
  density = 1
  expand = 3
  formula = G4_CALCIUM_SULFATE
  name = G4_CALCIUM_SULFATE
  specific = 4
FEATURE [App::DocumentObjectGroupPython] Ca_element009  label="Ca_element : 005"  # scripted group (container) (typed FeaturePython)
  n = 1
  ref = Ca_element
FEATURE [App::DocumentObjectGroupPython] W_element002  label="W_element : 002"  # scripted group (container) (typed FeaturePython)
  n = 1
  ref = W_element
FEATURE [App::DocumentObjectGroupPython] O_element024  label="O_element : 012"  # scripted group (container) (typed FeaturePython)
  n = 4
  ref = O_element
FEATURE [App::DocumentObjectGroupPython] G4_CALCIUM_TUNGSTATE  # scripted group (container) (typed FeaturePython)
  Dunit = g/cm3
  Dvalue = 6.062
  Group = -> [Ca_element009,W_element002,O_element024]
  conduct = 2
  density = 1
  expand = 3
  formula = G4_CALCIUM_TUNGSTATE
  name = G4_CALCIUM_TUNGSTATE
  specific = 4
FEATURE [App::DocumentObjectGroupPython] C_element023  label="C_element : 010"  # scripted group (container) (typed FeaturePython)
  n = 1
  ref = C_element
FEATURE [App::DocumentObjectGroupPython] O_element025  label="O_element : 013"  # scripted group (container) (typed FeaturePython)
  n = 2
  ref = O_element
FEATURE [App::DocumentObjectGroupPython] G4_CARBON_DIOXIDE  # scripted group (container) (typed FeaturePython)
  Dunit = g/cm3
  Dvalue = 0.00184212
  Group = -> [C_element023,O_element025]
  conduct = 2
  density = 1
  expand = 3
  formula = G4_CARBON_DIOXIDE
  name = G4_CARBON_DIOXIDE
  specific = 4
FEATURE [App::DocumentObjectGroupPython] C_element024  label="C_element : 011"  # scripted group (container) (typed FeaturePython)
  n = 1
  ref = C_element
FEATURE [App::DocumentObjectGroupPython] Cl_element004  label="Cl_element : 4"  # scripted group (container) (typed FeaturePython)
  n = 4
  ref = Cl_element
FEATURE [App::DocumentObjectGroupPython] G4_CARBON_TETRACHLORIDE  # scripted group (container) (typed FeaturePython)
  Dunit = g/cm3
  Dvalue = 1.594
  Group = -> [C_element024,Cl_element004]
  conduct = 2
  density = 1
  expand = 3
  formula = G4_CARBON_TETRACHLORIDE
  name = G4_CARBON_TETRACHLORIDE
  specific = 4
FEATURE [App::DocumentObjectGroupPython] C_element025  label="C_element : 012"  # scripted group (container) (typed FeaturePython)
  n = 6
  ref = C_element
FEATURE [App::DocumentObjectGroupPython] H_element021  label="H_element : 012"  # scripted group (container) (typed FeaturePython)
  n = 10
  ref = H_element
FEATURE [App::DocumentObjectGroupPython] O_element026  label="O_element : 5"  # scripted group (container) (typed FeaturePython)
  n = 5
  ref = O_element
FEATURE [App::DocumentObjectGroupPython] G4_CELLULOSE_CELLOPHANE  # scripted group (container) (typed FeaturePython)
  Dunit = g/cm3
  Dvalue = 1.42
  Group = -> [C_element025,H_element021,O_element026]
  conduct = 2
  density = 1
  expand = 3
  formula = G4_CELLULOSE_CELLOPHANE
  name = G4_CELLULOSE_CELLOPHANE
  specific = 4
FEATURE [App::DocumentObjectGroupPython] H_element022  label="H_element : 0.067"  # scripted group (container) (typed FeaturePython)
  n = 0.067125
FEATURE [App::DocumentObjectGroupPython] C_element026  label="C_element : 0.545"  # scripted group (container) (typed FeaturePython)
  n = 0.545403
FEATURE [App::DocumentObjectGroupPython] O_element027  label="O_element : 0.387"  # scripted group (container) (typed FeaturePython)
  n = 0.387472
FEATURE [App::DocumentObjectGroupPython] G4_CELLULOSE_BUTYRATE  # scripted group (container) (typed FeaturePython)
  Dunit = g/cm3
  Dvalue = 1.2
  Group = -> [H_element022,C_element026,O_element027]
  conduct = 2
  density = 1
  expand = 3
  formula = G4_CELLULOSE_BUTYRATE
  name = G4_CELLULOSE_BUTYRATE
  specific = 4
FEATURE [App::DocumentObjectGroupPython] H_element023  label="H_element : 0.029"  # scripted group (container) (typed FeaturePython)
  n = 0.029216
FEATURE [App::DocumentObjectGroupPython] C_element027  label="C_element : 0.271"  # scripted group (container) (typed FeaturePython)
  n = 0.271296
FEATURE [App::DocumentObjectGroupPython] N_element013  label="N_element : 0.121"  # scripted group (container) (typed FeaturePython)
  n = 0.121276
FEATURE [App::DocumentObjectGroupPython] O_element028  label="O_element : 0.578"  # scripted group (container) (typed FeaturePython)
  n = 0.578212
FEATURE [App::DocumentObjectGroupPython] G4_CELLULOSE_NITRATE  # scripted group (container) (typed FeaturePython)
  Dunit = g/cm3
  Dvalue = 1.49
  Group = -> [H_element023,C_element027,N_element013,O_element028]
  conduct = 2
  density = 1
  expand = 3
  formula = G4_CELLULOSE_NITRATE
  name = G4_CELLULOSE_NITRATE
  specific = 4
FEATURE [App::DocumentObjectGroupPython] H_element024  label="H_element : 0.108"  # scripted group (container) (typed FeaturePython)
  n = 0.107596
FEATURE [App::DocumentObjectGroupPython] N_element014  label="N_element : 0.001"  # scripted group (container) (typed FeaturePython)
  n = 0.0008
FEATURE [App::DocumentObjectGroupPython] O_element029  label="O_element : 0.875"  # scripted group (container) (typed FeaturePython)
  n = 0.874976
FEATURE [App::DocumentObjectGroupPython] S_element008  label="S_element : 0.015"  # scripted group (container) (typed FeaturePython)
  n = 0.014627
FEATURE [App::DocumentObjectGroupPython] Ce_element001  label="Ce_element : 0.002"  # scripted group (container) (typed FeaturePython)
  n = 0.002001
FEATURE [App::DocumentObjectGroupPython] G4_CERIC_SULFATE  # scripted group (container) (typed FeaturePython)
  Dunit = g/cm3
  Dvalue = 1.03
  Group = -> [H_element024,N_element014,O_element029,S_element008,Ce_element001]
  conduct = 2
  density = 1
  expand = 3
  formula = G4_CERIC_SULFATE
  name = G4_CERIC_SULFATE
  specific = 4
FEATURE [App::DocumentObjectGroupPython] Cs_element001  label="Cs_element : 1"  # scripted group (container) (typed FeaturePython)
  n = 1
  ref = Cs_element
FEATURE [App::DocumentObjectGroupPython] F_element006  label="F_element : 1"  # scripted group (container) (typed FeaturePython)
  n = 1
  ref = F_element
FEATURE [App::DocumentObjectGroupPython] G4_CESIUM_FLUORIDE  # scripted group (container) (typed FeaturePython)
  Dunit = g/cm3
  Dvalue = 4.115
  Group = -> [Cs_element001,F_element006]
  conduct = 2
  density = 1
  expand = 3
  formula = G4_CESIUM_FLUORIDE
  name = G4_CESIUM_FLUORIDE
  specific = 4
FEATURE [App::DocumentObjectGroupPython] Cs_element002  label="Cs_element : 002"  # scripted group (container) (typed FeaturePython)
  n = 1
  ref = Cs_element
FEATURE [App::DocumentObjectGroupPython] I_element001  label="I_element : 1"  # scripted group (container) (typed FeaturePython)
  n = 1
  ref = I_element
FEATURE [App::DocumentObjectGroupPython] G4_CESIUM_IODIDE  # scripted group (container) (typed FeaturePython)
  Dunit = g/cm3
  Dvalue = 4.51
  Group = -> [Cs_element002,I_element001]
  conduct = 2
  density = 1
  expand = 3
  formula = G4_CESIUM_IODIDE
  name = G4_CESIUM_IODIDE
  specific = 4
FEATURE [App::DocumentObjectGroupPython] C_element028  label="C_element : 013"  # scripted group (container) (typed FeaturePython)
  n = 6
  ref = C_element
FEATURE [App::DocumentObjectGroupPython] H_element025  label="H_element : 013"  # scripted group (container) (typed FeaturePython)
  n = 5
  ref = H_element
FEATURE [App::DocumentObjectGroupPython] Cl_element005  label="Cl_element : 1"  # scripted group (container) (typed FeaturePython)
  n = 1
  ref = Cl_element
FEATURE [App::DocumentObjectGroupPython] G4_CHLOROBENZENE  # scripted group (container) (typed FeaturePython)
  Dunit = g/cm3
  Dvalue = 1.1058
  Group = -> [C_element028,H_element025,Cl_element005]
  conduct = 2
  density = 1
  expand = 3
  formula = G4_CHLOROBENZENE
  name = G4_CHLOROBENZENE
  specific = 4
FEATURE [App::DocumentObjectGroupPython] C_element029  label="C_element : 014"  # scripted group (container) (typed FeaturePython)
  n = 1
  ref = C_element
FEATURE [App::DocumentObjectGroupPython] H_element026  label="H_element : 1"  # scripted group (container) (typed FeaturePython)
  n = 1
  ref = H_element
FEATURE [App::DocumentObjectGroupPython] Cl_element006  label="Cl_element : 3"  # scripted group (container) (typed FeaturePython)
  n = 3
  ref = Cl_element
FEATURE [App::DocumentObjectGroupPython] G4_CHLOROFORM  # scripted group (container) (typed FeaturePython)
  Dunit = g/cm3
  Dvalue = 1.4832
  Group = -> [C_element029,H_element026,Cl_element006]
  conduct = 2
  density = 1
  expand = 3
  formula = G4_CHLOROFORM
  name = G4_CHLOROFORM
  specific = 4
FEATURE [App::DocumentObjectGroupPython] H_element027  label="H_element : 0.010"  # scripted group (container) (typed FeaturePython)
  n = 0.01
FEATURE [App::DocumentObjectGroupPython] C_element030  label="C_element : 0.001"  # scripted group (container) (typed FeaturePython)
  n = 0.001
FEATURE [App::DocumentObjectGroupPython] O_element030  label="O_element : 0.529"  # scripted group (container) (typed FeaturePython)
  n = 0.529107
FEATURE [App::DocumentObjectGroupPython] Na_element005  label="Na_element : 0.016"  # scripted group (container) (typed FeaturePython)
  n = 0.016
FEATURE [App::DocumentObjectGroupPython] Mg_element003  label="Mg_element : 0.004"  # scripted group (container) (typed FeaturePython)
  n = 0.002
FEATURE [App::DocumentObjectGroupPython] Al_element002  label="Al_element : 0.034"  # scripted group (container) (typed FeaturePython)
  n = 0.033872
FEATURE [App::DocumentObjectGroupPython] Si_element002  label="Si_element : 0.337"  # scripted group (container) (typed FeaturePython)
  n = 0.337021
FEATURE [App::DocumentObjectGroupPython] K_element003  label="K_element : 0.013"  # scripted group (container) (typed FeaturePython)
  n = 0.013
FEATURE [App::DocumentObjectGroupPython] Ca_element010  label="Ca_element : 0.044"  # scripted group (container) (typed FeaturePython)
  n = 0.044
FEATURE [App::DocumentObjectGroupPython] Fe_element002  label="Fe_element : 0.014"  # scripted group (container) (typed FeaturePython)
  n = 0.014
FEATURE [App::DocumentObjectGroupPython] G4_CONCRETE  # scripted group (container) (typed FeaturePython)
  Dunit = g/cm3
  Dvalue = 2.3
  Group = -> [H_element027,C_element030,O_element030,Na_element005,Mg_element003,Al_element002,Si_element002,K_element003,Ca_element010,Fe_element002]
  conduct = 2
  density = 1
  expand = 3
  formula = G4_CONCRETE
  name = G4_CONCRETE
  specific = 4
FEATURE [App::DocumentObjectGroupPython] C_element031  label="C_element : 015"  # scripted group (container) (typed FeaturePython)
  n = 6
  ref = C_element
FEATURE [App::DocumentObjectGroupPython] H_element028  label="H_element : 12"  # scripted group (container) (typed FeaturePython)
  n = 12
  ref = H_element
FEATURE [App::DocumentObjectGroupPython] G4_CYCLOHEXANE  # scripted group (container) (typed FeaturePython)
  Dunit = g/cm3
  Dvalue = 0.779
  Group = -> [C_element031,H_element028]
  conduct = 2
  density = 1
  expand = 3
  formula = G4_CYCLOHEXANE
  name = G4_CYCLOHEXANE
  specific = 4
FEATURE [App::DocumentObjectGroupPython] C_element032  label="C_element : 016"  # scripted group (container) (typed FeaturePython)
  n = 6
  ref = C_element
FEATURE [App::DocumentObjectGroupPython] H_element029  label="H_element : 4"  # scripted group (container) (typed FeaturePython)
  n = 4
  ref = H_element
FEATURE [App::DocumentObjectGroupPython] Cl_element007  label="Cl_element : 2"  # scripted group (container) (typed FeaturePython)
  n = 2
  ref = Cl_element
FEATURE [App::DocumentObjectGroupPython] G4_1_2_DICHLOROBENZENE  label="G4_1.2-DICHLOROBENZENE"  # scripted group (container) (typed FeaturePython)
  Dunit = g/cm3
  Dvalue = 1.3048
  Group = -> [C_element032,H_element029,Cl_element007]
  conduct = 2
  density = 1
  expand = 3
  formula = G4_1.2-DICHLOROBENZENE
  name = G4_1.2-DICHLOROBENZENE
  specific = 4
FEATURE [App::DocumentObjectGroupPython] C_element033  label="C_element : 017"  # scripted group (container) (typed FeaturePython)
  n = 4
  ref = C_element
FEATURE [App::DocumentObjectGroupPython] H_element030  label="H_element : 8"  # scripted group (container) (typed FeaturePython)
  n = 8
  ref = H_element
FEATURE [App::DocumentObjectGroupPython] O_element031  label="O_element : 014"  # scripted group (container) (typed FeaturePython)
  n = 1
  ref = O_element
FEATURE [App::DocumentObjectGroupPython] Cl_element008  label="Cl_element : 005"  # scripted group (container) (typed FeaturePython)
  n = 2
  ref = Cl_element
FEATURE [App::DocumentObjectGroupPython] G4_DICHLORODIETHYL_ETHER  # scripted group (container) (typed FeaturePython)
  Dunit = g/cm3
  Dvalue = 1.2199
  Group = -> [C_element033,H_element030,O_element031,Cl_element008]
  conduct = 2
  density = 1
  expand = 3
  formula = G4_DICHLORODIETHYL_ETHER
  name = G4_DICHLORODIETHYL_ETHER
  specific = 4
FEATURE [App::DocumentObjectGroupPython] C_element034  label="C_element : 018"  # scripted group (container) (typed FeaturePython)
  n = 2
  ref = C_element
FEATURE [App::DocumentObjectGroupPython] H_element031  label="H_element : 014"  # scripted group (container) (typed FeaturePython)
  n = 4
  ref = H_element
FEATURE [App::DocumentObjectGroupPython] Cl_element009  label="Cl_element : 006"  # scripted group (container) (typed FeaturePython)
  n = 2
  ref = Cl_element
FEATURE [App::DocumentObjectGroupPython] G4_1_2_DICHLOROETHANE  label="G4_1.2-DICHLOROETHANE"  # scripted group (container) (typed FeaturePython)
  Dunit = g/cm3
  Dvalue = 1.2351
  Group = -> [C_element034,H_element031,Cl_element009]
  conduct = 2
  density = 1
  expand = 3
  formula = G4_1.2-DICHLOROETHANE
  name = G4_1.2-DICHLOROETHANE
  specific = 4
FEATURE [App::DocumentObjectGroupPython] C_element035  label="C_element : 019"  # scripted group (container) (typed FeaturePython)
  n = 4
  ref = C_element
FEATURE [App::DocumentObjectGroupPython] H_element032  label="H_element : 015"  # scripted group (container) (typed FeaturePython)
  n = 10
  ref = H_element
FEATURE [App::DocumentObjectGroupPython] O_element032  label="O_element : 015"  # scripted group (container) (typed FeaturePython)
  n = 1
  ref = O_element
FEATURE [App::DocumentObjectGroupPython] G4_DIETHYL_ETHER  # scripted group (container) (typed FeaturePython)
  Dunit = g/cm3
  Dvalue = 0.71378
  Group = -> [C_element035,H_element032,O_element032]
  conduct = 2
  density = 1
  expand = 3
  formula = G4_DIETHYL_ETHER
  name = G4_DIETHYL_ETHER
  specific = 4
FEATURE [App::DocumentObjectGroupPython] C_element036  label="C_element : 020"  # scripted group (container) (typed FeaturePython)
  n = 3
  ref = C_element
FEATURE [App::DocumentObjectGroupPython] H_element033  label="H_element : 016"  # scripted group (container) (typed FeaturePython)
  n = 7
  ref = H_element
FEATURE [App::DocumentObjectGroupPython] N_element015  label="N_element : 008"  # scripted group (container) (typed FeaturePython)
  n = 1
  ref = N_element
FEATURE [App::DocumentObjectGroupPython] O_element033  label="O_element : 016"  # scripted group (container) (typed FeaturePython)
  n = 1
  ref = O_element
FEATURE [App::DocumentObjectGroupPython] G4_N_N_DIMETHYL_FORMAMIDE  label="G4_N.N-DIMETHYL_FORMAMIDE"  # scripted group (container) (typed FeaturePython)
  Dunit = g/cm3
  Dvalue = 0.9487
  Group = -> [C_element036,H_element033,N_element015,O_element033]
  conduct = 2
  density = 1
  expand = 3
  formula = G4_N.N-DIMETHYL_FORMAMIDE
  name = G4_N.N-DIMETHYL_FORMAMIDE
  specific = 4
FEATURE [App::DocumentObjectGroupPython] C_element037  label="C_element : 021"  # scripted group (container) (typed FeaturePython)
  n = 2
  ref = C_element
FEATURE [App::DocumentObjectGroupPython] H_element034  label="H_element : 017"  # scripted group (container) (typed FeaturePython)
  n = 6
  ref = H_element
FEATURE [App::DocumentObjectGroupPython] O_element034  label="O_element : 017"  # scripted group (container) (typed FeaturePython)
  n = 1
  ref = O_element
FEATURE [App::DocumentObjectGroupPython] S_element009  label="S_element : 003"  # scripted group (container) (typed FeaturePython)
  n = 1
  ref = S_element
FEATURE [App::DocumentObjectGroupPython] G4_DIMETHYL_SULFOXIDE  # scripted group (container) (typed FeaturePython)
  Dunit = g/cm3
  Dvalue = 1.1014
  Group = -> [C_element037,H_element034,O_element034,S_element009]
  conduct = 2
  density = 1
  expand = 3
  formula = G4_DIMETHYL_SULFOXIDE
  name = G4_DIMETHYL_SULFOXIDE
  specific = 4
FEATURE [App::DocumentObjectGroupPython] C_element038  label="C_element : 022"  # scripted group (container) (typed FeaturePython)
  n = 2
  ref = C_element
FEATURE [App::DocumentObjectGroupPython] H_element035  label="H_element : 018"  # scripted group (container) (typed FeaturePython)
  n = 6
  ref = H_element
FEATURE [App::DocumentObjectGroupPython] G4_ETHANE  # scripted group (container) (typed FeaturePython)
  Dunit = g/cm3
  Dvalue = 0.00125324
  Group = -> [C_element038,H_element035]
  conduct = 2
  density = 1
  expand = 3
  formula = G4_ETHANE
  name = G4_ETHANE
  specific = 4
FEATURE [App::DocumentObjectGroupPython] C_element039  label="C_element : 023"  # scripted group (container) (typed FeaturePython)
  n = 2
  ref = C_element
FEATURE [App::DocumentObjectGroupPython] H_element036  label="H_element : 019"  # scripted group (container) (typed FeaturePython)
  n = 6
  ref = H_element
FEATURE [App::DocumentObjectGroupPython] O_element035  label="O_element : 018"  # scripted group (container) (typed FeaturePython)
  n = 1
  ref = O_element
FEATURE [App::DocumentObjectGroupPython] G4_ETHYL_ALCOHOL  # scripted group (container) (typed FeaturePython)
  Dunit = g/cm3
  Dvalue = 0.7893
  Group = -> [C_element039,H_element036,O_element035]
  conduct = 2
  density = 1
  expand = 3
  formula = G4_ETHYL_ALCOHOL
  name = G4_ETHYL_ALCOHOL
  specific = 4
FEATURE [App::DocumentObjectGroupPython] H_element037  label="H_element : 0.090"  # scripted group (container) (typed FeaturePython)
  n = 0.090027
FEATURE [App::DocumentObjectGroupPython] C_element040  label="C_element : 0.585"  # scripted group (container) (typed FeaturePython)
  n = 0.585182
FEATURE [App::DocumentObjectGroupPython] O_element036  label="O_element : 0.325"  # scripted group (container) (typed FeaturePython)
  n = 0.324791
FEATURE [App::DocumentObjectGroupPython] G4_ETHYL_CELLULOSE  # scripted group (container) (typed FeaturePython)
  Dunit = g/cm3
  Dvalue = 1.13
  Group = -> [H_element037,C_element040,O_element036]
  conduct = 2
  density = 1
  expand = 3
  formula = G4_ETHYL_CELLULOSE
  name = G4_ETHYL_CELLULOSE
  specific = 4
FEATURE [App::DocumentObjectGroupPython] C_element041  label="C_element : 024"  # scripted group (container) (typed FeaturePython)
  n = 2
  ref = C_element
FEATURE [App::DocumentObjectGroupPython] H_element038  label="H_element : 020"  # scripted group (container) (typed FeaturePython)
  n = 4
  ref = H_element
FEATURE [App::DocumentObjectGroupPython] G4_ETHYLENE  # scripted group (container) (typed FeaturePython)
  Dunit = g/cm3
  Dvalue = 0.00117497
  Group = -> [C_element041,H_element038]
  conduct = 2
  density = 1
  expand = 3
  formula = G4_ETHYLENE
  name = G4_ETHYLENE
  specific = 4
FEATURE [App::DocumentObjectGroupPython] H_element039  label="H_element : 0.096"  # scripted group (container) (typed FeaturePython)
  n = 0.096
FEATURE [App::DocumentObjectGroupPython] C_element042  label="C_element : 0.195"  # scripted group (container) (typed FeaturePython)
  n = 0.195
FEATURE [App::DocumentObjectGroupPython] N_element016  label="N_element : 0.057"  # scripted group (container) (typed FeaturePython)
  n = 0.057
FEATURE [App::DocumentObjectGroupPython] O_element037  label="O_element : 0.646"  # scripted group (container) (typed FeaturePython)
  n = 0.646
FEATURE [App::DocumentObjectGroupPython] Na_element006  label="Na_element : 0.017"  # scripted group (container) (typed FeaturePython)
  n = 0.001
FEATURE [App::DocumentObjectGroupPython] P_element005  label="P_element : 0.104"  # scripted group (container) (typed FeaturePython)
  n = 0.001
FEATURE [App::DocumentObjectGroupPython] S_element010  label="S_element : 0.016"  # scripted group (container) (typed FeaturePython)
  n = 0.003
FEATURE [App::DocumentObjectGroupPython] Cl_element010  label="Cl_element : 0.005"  # scripted group (container) (typed FeaturePython)
  n = 0.001
FEATURE [App::DocumentObjectGroupPython] G4_EYE_LENS_ICRP  # scripted group (container) (typed FeaturePython)
  Dunit = g/cm3
  Dvalue = 1.07
  Group = -> [H_element039,C_element042,N_element016,O_element037,Na_element006,P_element005,S_element010,Cl_element010]
  conduct = 2
  density = 1
  expand = 3
  formula = G4_EYE_LENS_ICRP
  name = G4_EYE_LENS_ICRP
  specific = 4
FEATURE [App::DocumentObjectGroupPython] Fe_element003  label="Fe_element : 2"  # scripted group (container) (typed FeaturePython)
  n = 2
  ref = Fe_element
FEATURE [App::DocumentObjectGroupPython] O_element038  label="O_element : 019"  # scripted group (container) (typed FeaturePython)
  n = 3
  ref = O_element
FEATURE [App::DocumentObjectGroupPython] G4_FERRIC_OXIDE  # scripted group (container) (typed FeaturePython)
  Dunit = g/cm3
  Dvalue = 5.2
  Group = -> [Fe_element003,O_element038]
  conduct = 2
  density = 1
  expand = 3
  formula = G4_FERRIC_OXIDE
  name = G4_FERRIC_OXIDE
  specific = 4
FEATURE [App::DocumentObjectGroupPython] Fe_element004  label="Fe_element : 1"  # scripted group (container) (typed FeaturePython)
  n = 1
  ref = Fe_element
FEATURE [App::DocumentObjectGroupPython] B_element003  label="B_element : 1"  # scripted group (container) (typed FeaturePython)
  n = 1
  ref = B_element
FEATURE [App::DocumentObjectGroupPython] G4_FERROBORIDE  # scripted group (container) (typed FeaturePython)
  Dunit = g/cm3
  Dvalue = 7.15
  Group = -> [Fe_element004,B_element003]
  conduct = 2
  density = 1
  expand = 3
  formula = G4_FERROBORIDE
  name = G4_FERROBORIDE
  specific = 4
FEATURE [App::DocumentObjectGroupPython] Fe_element005  label="Fe_element : 003"  # scripted group (container) (typed FeaturePython)
  n = 1
  ref = Fe_element
FEATURE [App::DocumentObjectGroupPython] O_element039  label="O_element : 020"  # scripted group (container) (typed FeaturePython)
  n = 1
  ref = O_element
FEATURE [App::DocumentObjectGroupPython] G4_FERROUS_OXIDE  # scripted group (container) (typed FeaturePython)
  Dunit = g/cm3
  Dvalue = 5.7
  Group = -> [Fe_element005,O_element039]
  conduct = 2
  density = 1
  expand = 3
  formula = G4_FERROUS_OXIDE
  name = G4_FERROUS_OXIDE
  specific = 4
FEATURE [App::DocumentObjectGroupPython] H_element040  label="H_element : 0.115"  # scripted group (container) (typed FeaturePython)
  n = 0.108259
FEATURE [App::DocumentObjectGroupPython] N_element017  label="N_element : 0.000"  # scripted group (container) (typed FeaturePython)
  n = 2.7e-05
FEATURE [App::DocumentObjectGroupPython] O_element040  label="O_element : 0.879"  # scripted group (container) (typed FeaturePython)
  n = 0.878636
FEATURE [App::DocumentObjectGroupPython] Na_element007  label="Na_element : 0.000"  # scripted group (container) (typed FeaturePython)
  n = 2.2e-05
FEATURE [App::DocumentObjectGroupPython] S_element011  label="S_element : 0.013"  # scripted group (container) (typed FeaturePython)
  n = 0.012968
FEATURE [App::DocumentObjectGroupPython] Cl_element011  label="Cl_element : 0.000"  # scripted group (container) (typed FeaturePython)
  n = 3.4e-05
FEATURE [App::DocumentObjectGroupPython] Fe_element006  label="Fe_element : 0.000"  # scripted group (container) (typed FeaturePython)
  n = 5.4e-05
FEATURE [App::DocumentObjectGroupPython] G4_FERROUS_SULFATE  # scripted group (container) (typed FeaturePython)
  Dunit = g/cm3
  Dvalue = 1.024
  Group = -> [H_element040,N_element017,O_element040,Na_element007,S_element011,Cl_element011,Fe_element006]
  conduct = 2
  density = 1
  expand = 3
  formula = G4_FERROUS_SULFATE
  name = G4_FERROUS_SULFATE
  specific = 4
FEATURE [App::DocumentObjectGroupPython] C_element043  label="C_element : 0.099"  # scripted group (container) (typed FeaturePython)
  n = 0.099335
FEATURE [App::DocumentObjectGroupPython] F_element007  label="F_element : 0.314"  # scripted group (container) (typed FeaturePython)
  n = 0.314247
FEATURE [App::DocumentObjectGroupPython] Cl_element012  label="Cl_element : 0.586"  # scripted group (container) (typed FeaturePython)
  n = 0.586418
FEATURE [App::DocumentObjectGroupPython] G4_FREON_12  label="G4_FREON-12"  # scripted group (container) (typed FeaturePython)
  Dunit = g/cm3
  Dvalue = 1.12
  Group = -> [C_element043,F_element007,Cl_element012]
  conduct = 2
  density = 1
  expand = 3
  formula = G4_FREON-12
  name = G4_FREON-12
  specific = 4
FEATURE [App::DocumentObjectGroupPython] C_element044  label="C_element : 0.057"  # scripted group (container) (typed FeaturePython)
  n = 0.057245
FEATURE [App::DocumentObjectGroupPython] F_element008  label="F_element : 0.181"  # scripted group (container) (typed FeaturePython)
  n = 0.181096
FEATURE [App::DocumentObjectGroupPython] Br_element001  label="Br_element : 0.762"  # scripted group (container) (typed FeaturePython)
  n = 0.761659
FEATURE [App::DocumentObjectGroupPython] G4_FREON_12B2  label="G4_FREON-12B2"  # scripted group (container) (typed FeaturePython)
  Dunit = g/cm3
  Dvalue = 1.8
  Group = -> [C_element044,F_element008,Br_element001]
  conduct = 2
  density = 1
  expand = 3
  formula = G4_FREON-12B2
  name = G4_FREON-12B2
  specific = 4
FEATURE [App::DocumentObjectGroupPython] C_element045  label="C_element : 0.115"  # scripted group (container) (typed FeaturePython)
  n = 0.114983
FEATURE [App::DocumentObjectGroupPython] F_element009  label="F_element : 0.546"  # scripted group (container) (typed FeaturePython)
  n = 0.545621
FEATURE [App::DocumentObjectGroupPython] Cl_element013  label="Cl_element : 0.339"  # scripted group (container) (typed FeaturePython)
  n = 0.339396
FEATURE [App::DocumentObjectGroupPython] G4_FREON_13  label="G4_FREON-13"  # scripted group (container) (typed FeaturePython)
  Dunit = g/cm3
  Dvalue = 0.95
  Group = -> [C_element045,F_element009,Cl_element013]
  conduct = 2
  density = 1
  expand = 3
  formula = G4_FREON-13
  name = G4_FREON-13
  specific = 4
FEATURE [App::DocumentObjectGroupPython] C_element046  label="C_element : 025"  # scripted group (container) (typed FeaturePython)
  n = 1
  ref = C_element
FEATURE [App::DocumentObjectGroupPython] F_element010  label="F_element : 3"  # scripted group (container) (typed FeaturePython)
  n = 3
  ref = F_element
FEATURE [App::DocumentObjectGroupPython] Br_element002  label="Br_element : 1"  # scripted group (container) (typed FeaturePython)
  n = 1
  ref = Br_element
FEATURE [App::DocumentObjectGroupPython] G4_FREON_13B1  label="G4_FREON-13B1"  # scripted group (container) (typed FeaturePython)
  Dunit = g/cm3
  Dvalue = 1.5
  Group = -> [C_element046,F_element010,Br_element002]
  conduct = 2
  density = 1
  expand = 3
  formula = G4_FREON-13B1
  name = G4_FREON-13B1
  specific = 4
FEATURE [App::DocumentObjectGroupPython] C_element047  label="C_element : 0.061"  # scripted group (container) (typed FeaturePython)
  n = 0.061309
FEATURE [App::DocumentObjectGroupPython] F_element011  label="F_element : 0.291"  # scripted group (container) (typed FeaturePython)
  n = 0.290924
FEATURE [App::DocumentObjectGroupPython] I_element002  label="I_element : 0.648"  # scripted group (container) (typed FeaturePython)
  n = 0.647767
FEATURE [App::DocumentObjectGroupPython] G4_FREON_13I1  label="G4_FREON-13I1"  # scripted group (container) (typed FeaturePython)
  Dunit = g/cm3
  Dvalue = 1.8
  Group = -> [C_element047,F_element011,I_element002]
  conduct = 2
  density = 1
  expand = 3
  formula = G4_FREON-13I1
  name = G4_FREON-13I1
  specific = 4
FEATURE [App::DocumentObjectGroupPython] Gd_element001  label="Gd_element : 2"  # scripted group (container) (typed FeaturePython)
  n = 2
  ref = Gd_element
FEATURE [App::DocumentObjectGroupPython] O_element041  label="O_element : 021"  # scripted group (container) (typed FeaturePython)
  n = 2
  ref = O_element
FEATURE [App::DocumentObjectGroupPython] S_element012  label="S_element : 004"  # scripted group (container) (typed FeaturePython)
  n = 1
  ref = S_element
FEATURE [App::DocumentObjectGroupPython] G4_GADOLINIUM_OXYSULFIDE  # scripted group (container) (typed FeaturePython)
  Dunit = g/cm3
  Dvalue = 7.44
  Group = -> [Gd_element001,O_element041,S_element012]
  conduct = 2
  density = 1
  expand = 3
  formula = G4_GADOLINIUM_OXYSULFIDE
  name = G4_GADOLINIUM_OXYSULFIDE
  specific = 4
FEATURE [App::DocumentObjectGroupPython] Ga_element001  label="Ga_element : 1"  # scripted group (container) (typed FeaturePython)
  n = 1
  ref = Ga_element
FEATURE [App::DocumentObjectGroupPython] As_element001  label="As_element : 1"  # scripted group (container) (typed FeaturePython)
  n = 1
  ref = As_element
FEATURE [App::DocumentObjectGroupPython] G4_GALLIUM_ARSENIDE  # scripted group (container) (typed FeaturePython)
  Dunit = g/cm3
  Dvalue = 5.31
  Group = -> [Ga_element001,As_element001]
  conduct = 2
  density = 1
  expand = 3
  formula = G4_GALLIUM_ARSENIDE
  name = G4_GALLIUM_ARSENIDE
  specific = 4
FEATURE [App::DocumentObjectGroupPython] H_element041  label="H_element : 0.081"  # scripted group (container) (typed FeaturePython)
  n = 0.08118
FEATURE [App::DocumentObjectGroupPython] C_element048  label="C_element : 0.416"  # scripted group (container) (typed FeaturePython)
  n = 0.41606
FEATURE [App::DocumentObjectGroupPython] N_element018  label="N_element : 0.111"  # scripted group (container) (typed FeaturePython)
  n = 0.11124
FEATURE [App::DocumentObjectGroupPython] O_element042  label="O_element : 0.381"  # scripted group (container) (typed FeaturePython)
  n = 0.38064
FEATURE [App::DocumentObjectGroupPython] S_element013  label="S_element : 0.011"  # scripted group (container) (typed FeaturePython)
  n = 0.01088
FEATURE [App::DocumentObjectGroupPython] G4_GEL_PHOTO_EMULSION  # scripted group (container) (typed FeaturePython)
  Dunit = g/cm3
  Dvalue = 1.2914
  Group = -> [H_element041,C_element048,N_element018,O_element042,S_element013]
  conduct = 2
  density = 1
  expand = 3
  formula = G4_GEL_PHOTO_EMULSION
  name = G4_GEL_PHOTO_EMULSION
  specific = 4
FEATURE [App::DocumentObjectGroupPython] B_element004  label="B_element : 0.040"  # scripted group (container) (typed FeaturePython)
  n = 0.0400639
FEATURE [App::DocumentObjectGroupPython] O_element043  label="O_element : 0.540"  # scripted group (container) (typed FeaturePython)
  n = 0.539561
FEATURE [App::DocumentObjectGroupPython] Na_element008  label="Na_element : 0.028"  # scripted group (container) (typed FeaturePython)
  n = 0.0281909
FEATURE [App::DocumentObjectGroupPython] Al_element003  label="Al_element : 0.012"  # scripted group (container) (typed FeaturePython)
  n = 0.011644
FEATURE [App::DocumentObjectGroupPython] Si_element003  label="Si_element : 0.377"  # scripted group (container) (typed FeaturePython)
  n = 0.377219
FEATURE [App::DocumentObjectGroupPython] K_element004  label="K_element : 0.014"  # scripted group (container) (typed FeaturePython)
  n = 0.00332099
FEATURE [App::DocumentObjectGroupPython] G4_Pyrex_Glass  # scripted group (container) (typed FeaturePython)
  Dunit = g/cm3
  Dvalue = 2.23
  Group = -> [B_element004,O_element043,Na_element008,Al_element003,Si_element003,K_element004]
  conduct = 2
  density = 1
  expand = 3
  formula = G4_Pyrex_Glass
  name = G4_Pyrex_Glass
  specific = 4
FEATURE [App::DocumentObjectGroupPython] O_element044  label="O_element : 0.156"  # scripted group (container) (typed FeaturePython)
  n = 0.156453
FEATURE [App::DocumentObjectGroupPython] Si_element004  label="Si_element : 0.081"  # scripted group (container) (typed FeaturePython)
  n = 0.080866
FEATURE [App::DocumentObjectGroupPython] Ti_element001  label="Ti_element : 0.008"  # scripted group (container) (typed FeaturePython)
  n = 0.008092
FEATURE [App::DocumentObjectGroupPython] As_element002  label="As_element : 0.003"  # scripted group (container) (typed FeaturePython)
  n = 0.002651
FEATURE [App::DocumentObjectGroupPython] Pb_element001  label="Pb_element : 0.752"  # scripted group (container) (typed FeaturePython)
  n = 0.751938
FEATURE [App::DocumentObjectGroupPython] G4_GLASS_LEAD  # scripted group (container) (typed FeaturePython)
  Dunit = g/cm3
  Dvalue = 6.22
  Group = -> [O_element044,Si_element004,Ti_element001,As_element002,Pb_element001]
  conduct = 2
  density = 1
  expand = 3
  formula = G4_GLASS_LEAD
  name = G4_GLASS_LEAD
  specific = 4
FEATURE [App::DocumentObjectGroupPython] O_element045  label="O_element : 0.460"  # scripted group (container) (typed FeaturePython)
  n = 0.4598
FEATURE [App::DocumentObjectGroupPython] Na_element009  label="Na_element : 0.096"  # scripted group (container) (typed FeaturePython)
  n = 0.0964411
FEATURE [App::DocumentObjectGroupPython] Si_element005  label="Si_element : 0.378"  # scripted group (container) (typed FeaturePython)
  n = 0.336553
FEATURE [App::DocumentObjectGroupPython] Ca_element011  label="Ca_element : 0.107"  # scripted group (container) (typed FeaturePython)
  n = 0.107205
FEATURE [App::DocumentObjectGroupPython] G4_GLASS_PLATE  # scripted group (container) (typed FeaturePython)
  Dunit = g/cm3
  Dvalue = 2.4
  Group = -> [O_element045,Na_element009,Si_element005,Ca_element011]
  conduct = 2
  density = 1
  expand = 3
  formula = G4_GLASS_PLATE
  name = G4_GLASS_PLATE
  specific = 4
FEATURE [App::DocumentObjectGroupPython] C_element049  label="C_element : 026"  # scripted group (container) (typed FeaturePython)
  n = 5
  ref = C_element
FEATURE [App::DocumentObjectGroupPython] H_element042  label="H_element : 021"  # scripted group (container) (typed FeaturePython)
  n = 10
  ref = H_element
FEATURE [App::DocumentObjectGroupPython] N_element019  label="N_element : 2"  # scripted group (container) (typed FeaturePython)
  n = 2
  ref = N_element
FEATURE [App::DocumentObjectGroupPython] O_element046  label="O_element : 022"  # scripted group (container) (typed FeaturePython)
  n = 3
  ref = O_element
FEATURE [App::DocumentObjectGroupPython] G4_GLUTAMINE  # scripted group (container) (typed FeaturePython)
  Dunit = g/cm3
  Dvalue = 1.46
  Group = -> [C_element049,H_element042,N_element019,O_element046]
  conduct = 2
  density = 1
  expand = 3
  formula = G4_GLUTAMINE
  name = G4_GLUTAMINE
  specific = 4
FEATURE [App::DocumentObjectGroupPython] C_element050  label="C_element : 027"  # scripted group (container) (typed FeaturePython)
  n = 3
  ref = C_element
FEATURE [App::DocumentObjectGroupPython] H_element043  label="H_element : 022"  # scripted group (container) (typed FeaturePython)
  n = 8
  ref = H_element
FEATURE [App::DocumentObjectGroupPython] O_element047  label="O_element : 023"  # scripted group (container) (typed FeaturePython)
  n = 3
  ref = O_element
FEATURE [App::DocumentObjectGroupPython] G4_GLYCEROL  # scripted group (container) (typed FeaturePython)
  Dunit = g/cm3
  Dvalue = 1.2613
  Group = -> [C_element050,H_element043,O_element047]
  conduct = 2
  density = 1
  expand = 3
  formula = G4_GLYCEROL
  name = G4_GLYCEROL
  specific = 4
FEATURE [App::DocumentObjectGroupPython] C_element051  label="C_element : 028"  # scripted group (container) (typed FeaturePython)
  n = 5
  ref = C_element
FEATURE [App::DocumentObjectGroupPython] H_element044  label="H_element : 023"  # scripted group (container) (typed FeaturePython)
  n = 5
  ref = H_element
FEATURE [App::DocumentObjectGroupPython] N_element020  label="N_element : 009"  # scripted group (container) (typed FeaturePython)
  n = 5
  ref = N_element
FEATURE [App::DocumentObjectGroupPython] O_element048  label="O_element : 024"  # scripted group (container) (typed FeaturePython)
  n = 1
  ref = O_element
FEATURE [App::DocumentObjectGroupPython] G4_GUANINE  # scripted group (container) (typed FeaturePython)
  Dunit = g/cm3
  Dvalue = 2.2
  Group = -> [C_element051,H_element044,N_element020,O_element048]
  conduct = 2
  density = 1
  expand = 3
  formula = G4_GUANINE
  name = G4_GUANINE
  specific = 4
FEATURE [App::DocumentObjectGroupPython] Ca_element012  label="Ca_element : 006"  # scripted group (container) (typed FeaturePython)
  n = 1
  ref = Ca_element
FEATURE [App::DocumentObjectGroupPython] S_element014  label="S_element : 005"  # scripted group (container) (typed FeaturePython)
  n = 1
  ref = S_element
FEATURE [App::DocumentObjectGroupPython] O_element049  label="O_element : 6"  # scripted group (container) (typed FeaturePython)
  n = 6
  ref = O_element
FEATURE [App::DocumentObjectGroupPython] H_element045  label="H_element : 024"  # scripted group (container) (typed FeaturePython)
  n = 4
  ref = H_element
FEATURE [App::DocumentObjectGroupPython] G4_GYPSUM  # scripted group (container) (typed FeaturePython)
  Dunit = g/cm3
  Dvalue = 2.32
  Group = -> [Ca_element012,S_element014,O_element049,H_element045]
  conduct = 2
  density = 1
  expand = 3
  formula = G4_GYPSUM
  name = G4_GYPSUM
  specific = 4
FEATURE [App::DocumentObjectGroupPython] C_element052  label="C_element : 7"  # scripted group (container) (typed FeaturePython)
  n = 7
  ref = C_element
FEATURE [App::DocumentObjectGroupPython] H_element046  label="H_element : 16"  # scripted group (container) (typed FeaturePython)
  n = 16
  ref = H_element
FEATURE [App::DocumentObjectGroupPython] G4_N_HEPTANE  label="G4_N-HEPTANE"  # scripted group (container) (typed FeaturePython)
  Dunit = g/cm3
  Dvalue = 0.68376
  Group = -> [C_element052,H_element046]
  conduct = 2
  density = 1
  expand = 3
  formula = G4_N-HEPTANE
  name = G4_N-HEPTANE
  specific = 4
FEATURE [App::DocumentObjectGroupPython] C_element053  label="C_element : 029"  # scripted group (container) (typed FeaturePython)
  n = 6
  ref = C_element
FEATURE [App::DocumentObjectGroupPython] H_element047  label="H_element : 14"  # scripted group (container) (typed FeaturePython)
  n = 14
  ref = H_element
FEATURE [App::DocumentObjectGroupPython] G4_N_HEXANE  label="G4_N-HEXANE"  # scripted group (container) (typed FeaturePython)
  Dunit = g/cm3
  Dvalue = 0.6603
  Group = -> [C_element053,H_element047]
  conduct = 2
  density = 1
  expand = 3
  formula = G4_N-HEXANE
  name = G4_N-HEXANE
  specific = 4
FEATURE [App::DocumentObjectGroupPython] C_element054  label="C_element : 22"  # scripted group (container) (typed FeaturePython)
  n = 22
  ref = C_element
FEATURE [App::DocumentObjectGroupPython] H_element048  label="H_element : 025"  # scripted group (container) (typed FeaturePython)
  n = 10
  ref = H_element
FEATURE [App::DocumentObjectGroupPython] N_element021  label="N_element : 010"  # scripted group (container) (typed FeaturePython)
  n = 2
  ref = N_element
FEATURE [App::DocumentObjectGroupPython] O_element050  label="O_element : 025"  # scripted group (container) (typed FeaturePython)
  n = 5
  ref = O_element
FEATURE [App::DocumentObjectGroupPython] G4_KAPTON  # scripted group (container) (typed FeaturePython)
  Dunit = g/cm3
  Dvalue = 1.42
  Group = -> [C_element054,H_element048,N_element021,O_element050]
  conduct = 2
  density = 1
  expand = 3
  formula = G4_KAPTON
  name = G4_KAPTON
  specific = 4
FEATURE [App::DocumentObjectGroupPython] La_element001  label="La_element : 1"  # scripted group (container) (typed FeaturePython)
  n = 1
  ref = La_element
FEATURE [App::DocumentObjectGroupPython] Br_element003  label="Br_element : 002"  # scripted group (container) (typed FeaturePython)
  n = 1
  ref = Br_element
FEATURE [App::DocumentObjectGroupPython] O_element051  label="O_element : 026"  # scripted group (container) (typed FeaturePython)
  n = 1
  ref = O_element
FEATURE [App::DocumentObjectGroupPython] G4_LANTHANUM_OXYBROMIDE  # scripted group (container) (typed FeaturePython)
  Dunit = g/cm3
  Dvalue = 6.28
  Group = -> [La_element001,Br_element003,O_element051]
  conduct = 2
  density = 1
  expand = 3
  formula = G4_LANTHANUM_OXYBROMIDE
  name = G4_LANTHANUM_OXYBROMIDE
  specific = 4
FEATURE [App::DocumentObjectGroupPython] La_element002  label="La_element : 2"  # scripted group (container) (typed FeaturePython)
  n = 2
  ref = La_element
FEATURE [App::DocumentObjectGroupPython] O_element052  label="O_element : 027"  # scripted group (container) (typed FeaturePython)
  n = 2
  ref = O_element
FEATURE [App::DocumentObjectGroupPython] S_element015  label="S_element : 006"  # scripted group (container) (typed FeaturePython)
  n = 1
  ref = S_element
FEATURE [App::DocumentObjectGroupPython] G4_LANTHANUM_OXYSULFIDE  # scripted group (container) (typed FeaturePython)
  Dunit = g/cm3
  Dvalue = 5.86
  Group = -> [La_element002,O_element052,S_element015]
  conduct = 2
  density = 1
  expand = 3
  formula = G4_LANTHANUM_OXYSULFIDE
  name = G4_LANTHANUM_OXYSULFIDE
  specific = 4
FEATURE [App::DocumentObjectGroupPython] O_element053  label="O_element : 0.072"  # scripted group (container) (typed FeaturePython)
  n = 0.071682
FEATURE [App::DocumentObjectGroupPython] Pb_element002  label="Pb_element : 0.928"  # scripted group (container) (typed FeaturePython)
  n = 0.928318
FEATURE [App::DocumentObjectGroupPython] G4_LEAD_OXIDE  # scripted group (container) (typed FeaturePython)
  Dunit = g/cm3
  Dvalue = 9.53
  Group = -> [O_element053,Pb_element002]
  conduct = 2
  density = 1
  expand = 3
  formula = G4_LEAD_OXIDE
  name = G4_LEAD_OXIDE
  specific = 4
FEATURE [App::DocumentObjectGroupPython] Li_element001  label="Li_element : 1"  # scripted group (container) (typed FeaturePython)
  n = 1
  ref = Li_element
FEATURE [App::DocumentObjectGroupPython] N_element022  label="N_element : 011"  # scripted group (container) (typed FeaturePython)
  n = 1
  ref = N_element
FEATURE [App::DocumentObjectGroupPython] H_element049  label="H_element : 026"  # scripted group (container) (typed FeaturePython)
  n = 2
  ref = H_element
FEATURE [App::DocumentObjectGroupPython] G4_LITHIUM_AMIDE  # scripted group (container) (typed FeaturePython)
  Dunit = g/cm3
  Dvalue = 1.178
  Group = -> [Li_element001,N_element022,H_element049]
  conduct = 2
  density = 1
  expand = 3
  formula = G4_LITHIUM_AMIDE
  name = G4_LITHIUM_AMIDE
  specific = 4
FEATURE [App::DocumentObjectGroupPython] Li_element002  label="Li_element : 2"  # scripted group (container) (typed FeaturePython)
  n = 2
  ref = Li_element
FEATURE [App::DocumentObjectGroupPython] C_element055  label="C_element : 030"  # scripted group (container) (typed FeaturePython)
  n = 1
  ref = C_element
FEATURE [App::DocumentObjectGroupPython] O_element054  label="O_element : 028"  # scripted group (container) (typed FeaturePython)
  n = 3
  ref = O_element
FEATURE [App::DocumentObjectGroupPython] G4_LITHIUM_CARBONATE  # scripted group (container) (typed FeaturePython)
  Dunit = g/cm3
  Dvalue = 2.11
  Group = -> [Li_element002,C_element055,O_element054]
  conduct = 2
  density = 1
  expand = 3
  formula = G4_LITHIUM_CARBONATE
  name = G4_LITHIUM_CARBONATE
  specific = 4
FEATURE [App::DocumentObjectGroupPython] Li_element003  label="Li_element : 003"  # scripted group (container) (typed FeaturePython)
  n = 1
  ref = Li_element
FEATURE [App::DocumentObjectGroupPython] F_element012  label="F_element : 004"  # scripted group (container) (typed FeaturePython)
  n = 1
  ref = F_element
FEATURE [App::DocumentObjectGroupPython] G4_LITHIUM_FLUORIDE  # scripted group (container) (typed FeaturePython)
  Dunit = g/cm3
  Dvalue = 2.635
  Group = -> [Li_element003,F_element012]
  conduct = 2
  density = 1
  expand = 3
  formula = G4_LITHIUM_FLUORIDE
  name = G4_LITHIUM_FLUORIDE
  specific = 4
FEATURE [App::DocumentObjectGroupPython] Li_element004  label="Li_element : 004"  # scripted group (container) (typed FeaturePython)
  n = 1
  ref = Li_element
FEATURE [App::DocumentObjectGroupPython] H_element050  label="H_element : 027"  # scripted group (container) (typed FeaturePython)
  n = 1
  ref = H_element
FEATURE [App::DocumentObjectGroupPython] G4_LITHIUM_HYDRIDE  # scripted group (container) (typed FeaturePython)
  Dunit = g/cm3
  Dvalue = 0.82
  Group = -> [Li_element004,H_element050]
  conduct = 2
  density = 1
  expand = 3
  formula = G4_LITHIUM_HYDRIDE
  name = G4_LITHIUM_HYDRIDE
  specific = 4
FEATURE [App::DocumentObjectGroupPython] Li_element005  label="Li_element : 005"  # scripted group (container) (typed FeaturePython)
  n = 1
  ref = Li_element
FEATURE [App::DocumentObjectGroupPython] I_element003  label="I_element : 002"  # scripted group (container) (typed FeaturePython)
  n = 1
  ref = I_element
FEATURE [App::DocumentObjectGroupPython] G4_LITHIUM_IODIDE  # scripted group (container) (typed FeaturePython)
  Dunit = g/cm3
  Dvalue = 3.494
  Group = -> [Li_element005,I_element003]
  conduct = 2
  density = 1
  expand = 3
  formula = G4_LITHIUM_IODIDE
  name = G4_LITHIUM_IODIDE
  specific = 4
FEATURE [App::DocumentObjectGroupPython] Li_element006  label="Li_element : 006"  # scripted group (container) (typed FeaturePython)
  n = 2
  ref = Li_element
FEATURE [App::DocumentObjectGroupPython] O_element055  label="O_element : 029"  # scripted group (container) (typed FeaturePython)
  n = 1
  ref = O_element
FEATURE [App::DocumentObjectGroupPython] G4_LITHIUM_OXIDE  # scripted group (container) (typed FeaturePython)
  Dunit = g/cm3
  Dvalue = 2.013
  Group = -> [Li_element006,O_element055]
  conduct = 2
  density = 1
  expand = 3
  formula = G4_LITHIUM_OXIDE
  name = G4_LITHIUM_OXIDE
  specific = 4
FEATURE [App::DocumentObjectGroupPython] Li_element007  label="Li_element : 007"  # scripted group (container) (typed FeaturePython)
  n = 2
  ref = Li_element
FEATURE [App::DocumentObjectGroupPython] B_element005  label="B_element : 005"  # scripted group (container) (typed FeaturePython)
  n = 4
  ref = B_element
FEATURE [App::DocumentObjectGroupPython] O_element056  label="O_element : 7"  # scripted group (container) (typed FeaturePython)
  n = 7
  ref = O_element
FEATURE [App::DocumentObjectGroupPython] G4_LITHIUM_TETRABORATE  # scripted group (container) (typed FeaturePython)
  Dunit = g/cm3
  Dvalue = 2.44
  Group = -> [Li_element007,B_element005,O_element056]
  conduct = 2
  density = 1
  expand = 3
  formula = G4_LITHIUM_TETRABORATE
  name = G4_LITHIUM_TETRABORATE
  specific = 4
FEATURE [App::DocumentObjectGroupPython] H_element051  label="H_element : 0.105"  # scripted group (container) (typed FeaturePython)
  n = 0.105
FEATURE [App::DocumentObjectGroupPython] C_element056  label="C_element : 0.083"  # scripted group (container) (typed FeaturePython)
  n = 0.083
FEATURE [App::DocumentObjectGroupPython] N_element023  label="N_element : 0.023"  # scripted group (container) (typed FeaturePython)
  n = 0.023
FEATURE [App::DocumentObjectGroupPython] O_element057  label="O_element : 0.779"  # scripted group (container) (typed FeaturePython)
  n = 0.779
FEATURE [App::DocumentObjectGroupPython] Na_element010  label="Na_element : 0.097"  # scripted group (container) (typed FeaturePython)
  n = 0.002
FEATURE [App::DocumentObjectGroupPython] P_element006  label="P_element : 0.105"  # scripted group (container) (typed FeaturePython)
  n = 0.001
FEATURE [App::DocumentObjectGroupPython] S_element016  label="S_element : 0.017"  # scripted group (container) (typed FeaturePython)
  n = 0.002
FEATURE [App::DocumentObjectGroupPython] Cl_element014  label="Cl_element : 0.587"  # scripted group (container) (typed FeaturePython)
  n = 0.003
FEATURE [App::DocumentObjectGroupPython] K_element005  label="K_element : 0.015"  # scripted group (container) (typed FeaturePython)
  n = 0.002
FEATURE [App::DocumentObjectGroupPython] G4_LUNG_ICRP  # scripted group (container) (typed FeaturePython)
  Dunit = g/cm3
  Dvalue = 1.04
  Group = -> [H_element051,C_element056,N_element023,O_element057,Na_element010,P_element006,S_element016,Cl_element014,K_element005]
  conduct = 2
  density = 1
  expand = 3
  formula = G4_LUNG_ICRP
  name = G4_LUNG_ICRP
  specific = 4
FEATURE [App::DocumentObjectGroupPython] H_element052  label="H_element : 0.116"  # scripted group (container) (typed FeaturePython)
  n = 0.114318
FEATURE [App::DocumentObjectGroupPython] C_element057  label="C_element : 0.656"  # scripted group (container) (typed FeaturePython)
  n = 0.655824
FEATURE [App::DocumentObjectGroupPython] O_element058  label="O_element : 0.092"  # scripted group (container) (typed FeaturePython)
  n = 0.0921831
FEATURE [App::DocumentObjectGroupPython] Mg_element004  label="Mg_element : 0.135"  # scripted group (container) (typed FeaturePython)
  n = 0.134792
FEATURE [App::DocumentObjectGroupPython] Ca_element013  label="Ca_element : 0.003"  # scripted group (container) (typed FeaturePython)
  n = 0.002883
FEATURE [App::DocumentObjectGroupPython] G4_M3_WAX  # scripted group (container) (typed FeaturePython)
  Dunit = g/cm3
  Dvalue = 1.05
  Group = -> [H_element052,C_element057,O_element058,Mg_element004,Ca_element013]
  conduct = 2
  density = 1
  expand = 3
  formula = G4_M3_WAX
  name = G4_M3_WAX
  specific = 4
FEATURE [App::DocumentObjectGroupPython] Mg_element005  label="Mg_element : 1"  # scripted group (container) (typed FeaturePython)
  n = 1
  ref = Mg_element
FEATURE [App::DocumentObjectGroupPython] C_element058  label="C_element : 031"  # scripted group (container) (typed FeaturePython)
  n = 1
  ref = C_element
FEATURE [App::DocumentObjectGroupPython] O_element059  label="O_element : 030"  # scripted group (container) (typed FeaturePython)
  n = 3
  ref = O_element
FEATURE [App::DocumentObjectGroupPython] G4_MAGNESIUM_CARBONATE  # scripted group (container) (typed FeaturePython)
  Dunit = g/cm3
  Dvalue = 2.958
  Group = -> [Mg_element005,C_element058,O_element059]
  conduct = 2
  density = 1
  expand = 3
  formula = G4_MAGNESIUM_CARBONATE
  name = G4_MAGNESIUM_CARBONATE
  specific = 4
FEATURE [App::DocumentObjectGroupPython] Mg_element006  label="Mg_element : 002"  # scripted group (container) (typed FeaturePython)
  n = 1
  ref = Mg_element
FEATURE [App::DocumentObjectGroupPython] F_element013  label="F_element : 005"  # scripted group (container) (typed FeaturePython)
  n = 2
  ref = F_element
FEATURE [App::DocumentObjectGroupPython] G4_MAGNESIUM_FLUORIDE  # scripted group (container) (typed FeaturePython)
  Dunit = g/cm3
  Dvalue = 3
  Group = -> [Mg_element006,F_element013]
  conduct = 2
  density = 1
  expand = 3
  formula = G4_MAGNESIUM_FLUORIDE
  name = G4_MAGNESIUM_FLUORIDE
  specific = 4
FEATURE [App::DocumentObjectGroupPython] Mg_element007  label="Mg_element : 003"  # scripted group (container) (typed FeaturePython)
  n = 1
  ref = Mg_element
FEATURE [App::DocumentObjectGroupPython] O_element060  label="O_element : 031"  # scripted group (container) (typed FeaturePython)
  n = 1
  ref = O_element
FEATURE [App::DocumentObjectGroupPython] G4_MAGNESIUM_OXIDE  # scripted group (container) (typed FeaturePython)
  Dunit = g/cm3
  Dvalue = 3.58
  Group = -> [Mg_element007,O_element060]
  conduct = 2
  density = 1
  expand = 3
  formula = G4_MAGNESIUM_OXIDE
  name = G4_MAGNESIUM_OXIDE
  specific = 4
FEATURE [App::DocumentObjectGroupPython] Mg_element008  label="Mg_element : 004"  # scripted group (container) (typed FeaturePython)
  n = 1
  ref = Mg_element
FEATURE [App::DocumentObjectGroupPython] B_element006  label="B_element : 006"  # scripted group (container) (typed FeaturePython)
  n = 4
  ref = B_element
FEATURE [App::DocumentObjectGroupPython] O_element061  label="O_element : 032"  # scripted group (container) (typed FeaturePython)
  n = 7
  ref = O_element
FEATURE [App::DocumentObjectGroupPython] G4_MAGNESIUM_TETRABORATE  # scripted group (container) (typed FeaturePython)
  Dunit = g/cm3
  Dvalue = 2.53
  Group = -> [Mg_element008,B_element006,O_element061]
  conduct = 2
  density = 1
  expand = 3
  formula = G4_MAGNESIUM_TETRABORATE
  name = G4_MAGNESIUM_TETRABORATE
  specific = 4
FEATURE [App::DocumentObjectGroupPython] Hg_element001  label="Hg_element : 1"  # scripted group (container) (typed FeaturePython)
  n = 1
  ref = Hg_element
FEATURE [App::DocumentObjectGroupPython] I_element004  label="I_element : 2"  # scripted group (container) (typed FeaturePython)
  n = 2
  ref = I_element
FEATURE [App::DocumentObjectGroupPython] G4_MERCURIC_IODIDE  # scripted group (container) (typed FeaturePython)
  Dunit = g/cm3
  Dvalue = 6.36
  Group = -> [Hg_element001,I_element004]
  conduct = 2
  density = 1
  expand = 3
  formula = G4_MERCURIC_IODIDE
  name = G4_MERCURIC_IODIDE
  specific = 4
FEATURE [App::DocumentObjectGroupPython] C_element059  label="C_element : 032"  # scripted group (container) (typed FeaturePython)
  n = 1
  ref = C_element
FEATURE [App::DocumentObjectGroupPython] H_element053  label="H_element : 028"  # scripted group (container) (typed FeaturePython)
  n = 4
  ref = H_element
FEATURE [App::DocumentObjectGroupPython] G4_METHANE  # scripted group (container) (typed FeaturePython)
  Dunit = g/cm3
  Dvalue = 0.000667151
  Group = -> [C_element059,H_element053]
  conduct = 2
  density = 1
  expand = 3
  formula = G4_METHANE
  name = G4_METHANE
  specific = 4
FEATURE [App::DocumentObjectGroupPython] C_element060  label="C_element : 033"  # scripted group (container) (typed FeaturePython)
  n = 1
  ref = C_element
FEATURE [App::DocumentObjectGroupPython] H_element054  label="H_element : 029"  # scripted group (container) (typed FeaturePython)
  n = 4
  ref = H_element
FEATURE [App::DocumentObjectGroupPython] O_element062  label="O_element : 033"  # scripted group (container) (typed FeaturePython)
  n = 1
  ref = O_element
FEATURE [App::DocumentObjectGroupPython] G4_METHANOL  # scripted group (container) (typed FeaturePython)
  Dunit = g/cm3
  Dvalue = 0.7914
  Group = -> [C_element060,H_element054,O_element062]
  conduct = 2
  density = 1
  expand = 3
  formula = G4_METHANOL
  name = G4_METHANOL
  specific = 4
FEATURE [App::DocumentObjectGroupPython] H_element055  label="H_element : 0.134"  # scripted group (container) (typed FeaturePython)
  n = 0.13404
FEATURE [App::DocumentObjectGroupPython] C_element061  label="C_element : 0.778"  # scripted group (container) (typed FeaturePython)
  n = 0.77796
FEATURE [App::DocumentObjectGroupPython] O_element063  label="O_element : 0.035"  # scripted group (container) (typed FeaturePython)
  n = 0.03502
FEATURE [App::DocumentObjectGroupPython] Mg_element009  label="Mg_element : 0.039"  # scripted group (container) (typed FeaturePython)
  n = 0.038594
FEATURE [App::DocumentObjectGroupPython] Ti_element002  label="Ti_element : 0.014"  # scripted group (container) (typed FeaturePython)
  n = 0.014386
FEATURE [App::DocumentObjectGroupPython] G4_MIX_D_WAX  # scripted group (container) (typed FeaturePython)
  Dunit = g/cm3
  Dvalue = 0.99
  Group = -> [H_element055,C_element061,O_element063,Mg_element009,Ti_element002]
  conduct = 2
  density = 1
  expand = 3
  formula = G4_MIX_D_WAX
  name = G4_MIX_D_WAX
  specific = 4
FEATURE [App::DocumentObjectGroupPython] H_element056  label="H_element : 0.135"  # scripted group (container) (typed FeaturePython)
  n = 0.081192
FEATURE [App::DocumentObjectGroupPython] C_element062  label="C_element : 0.583"  # scripted group (container) (typed FeaturePython)
  n = 0.583442
FEATURE [App::DocumentObjectGroupPython] N_element024  label="N_element : 0.018"  # scripted group (container) (typed FeaturePython)
  n = 0.017798
FEATURE [App::DocumentObjectGroupPython] O_element064  label="O_element : 0.186"  # scripted group (container) (typed FeaturePython)
  n = 0.186381
FEATURE [App::DocumentObjectGroupPython] Mg_element010  label="Mg_element : 0.130"  # scripted group (container) (typed FeaturePython)
  n = 0.130287
FEATURE [App::DocumentObjectGroupPython] Cl_element015  label="Cl_element : 0.588"  # scripted group (container) (typed FeaturePython)
  n = 0.0009
FEATURE [App::DocumentObjectGroupPython] G4_MS20_TISSUE  # scripted group (container) (typed FeaturePython)
  Dunit = g/cm3
  Dvalue = 1
  Group = -> [H_element056,C_element062,N_element024,O_element064,Mg_element010,Cl_element015]
  conduct = 2
  density = 1
  expand = 3
  formula = G4_MS20_TISSUE
  name = G4_MS20_TISSUE
  specific = 4
FEATURE [App::DocumentObjectGroupPython] H_element057  label="H_element : 0.136"  # scripted group (container) (typed FeaturePython)
  n = 0.102
FEATURE [App::DocumentObjectGroupPython] C_element063  label="C_element : 0.143"  # scripted group (container) (typed FeaturePython)
  n = 0.143
FEATURE [App::DocumentObjectGroupPython] N_element025  label="N_element : 0.034"  # scripted group (container) (typed FeaturePython)
  n = 0.034
FEATURE [App::DocumentObjectGroupPython] O_element065  label="O_element : 0.710"  # scripted group (container) (typed FeaturePython)
  n = 0.71
FEATURE [App::DocumentObjectGroupPython] Na_element011  label="Na_element : 0.098"  # scripted group (container) (typed FeaturePython)
  n = 0.001
FEATURE [App::DocumentObjectGroupPython] P_element007  label="P_element : 0.002"  # scripted group (container) (typed FeaturePython)
  n = 0.002
FEATURE [App::DocumentObjectGroupPython] S_element017  label="S_element : 0.018"  # scripted group (container) (typed FeaturePython)
  n = 0.003
FEATURE [App::DocumentObjectGroupPython] Cl_element016  label="Cl_element : 0.589"  # scripted group (container) (typed FeaturePython)
  n = 0.001
FEATURE [App::DocumentObjectGroupPython] K_element006  label="K_element : 0.004"  # scripted group (container) (typed FeaturePython)
  n = 0.004
FEATURE [App::DocumentObjectGroupPython] G4_MUSCLE_SKELETAL_ICRP  # scripted group (container) (typed FeaturePython)
  Dunit = g/cm3
  Dvalue = 1.05
  Group = -> [H_element057,C_element063,N_element025,O_element065,Na_element011,P_element007,S_element017,Cl_element016,K_element006]
  conduct = 2
  density = 1
  expand = 3
  formula = G4_MUSCLE_SKELETAL_ICRP
  name = G4_MUSCLE_SKELETAL_ICRP
  specific = 4
FEATURE [App::DocumentObjectGroupPython] H_element058  label="H_element : 0.137"  # scripted group (container) (typed FeaturePython)
  n = 0.102102
FEATURE [App::DocumentObjectGroupPython] C_element064  label="C_element : 0.123"  # scripted group (container) (typed FeaturePython)
  n = 0.123123
FEATURE [App::DocumentObjectGroupPython] N_element026  label="N_element : 0.756"  # scripted group (container) (typed FeaturePython)
  n = 0.035035
FEATURE [App::DocumentObjectGroupPython] O_element066  label="O_element : 0.730"  # scripted group (container) (typed FeaturePython)
  n = 0.72973
FEATURE [App::DocumentObjectGroupPython] Na_element012  label="Na_element : 0.099"  # scripted group (container) (typed FeaturePython)
  n = 0.001001
FEATURE [App::DocumentObjectGroupPython] P_element008  label="P_element : 0.106"  # scripted group (container) (typed FeaturePython)
  n = 0.002002
FEATURE [App::DocumentObjectGroupPython] S_element018  label="S_element : 0.019"  # scripted group (container) (typed FeaturePython)
  n = 0.004004
FEATURE [App::DocumentObjectGroupPython] K_element007  label="K_element : 0.016"  # scripted group (container) (typed FeaturePython)
  n = 0.003003
FEATURE [App::DocumentObjectGroupPython] G4_MUSCLE_STRIATED_ICRU  # scripted group (container) (typed FeaturePython)
  Dunit = g/cm3
  Dvalue = 1.04
  Group = -> [H_element058,C_element064,N_element026,O_element066,Na_element012,P_element008,S_element018,K_element007]
  conduct = 2
  density = 1
  expand = 3
  formula = G4_MUSCLE_STRIATED_ICRU
  name = G4_MUSCLE_STRIATED_ICRU
  specific = 4
FEATURE [App::DocumentObjectGroupPython] H_element059  label="H_element : 0.098"  # scripted group (container) (typed FeaturePython)
  n = 0.0982341
FEATURE [App::DocumentObjectGroupPython] C_element065  label="C_element : 0.156"  # scripted group (container) (typed FeaturePython)
  n = 0.156214
FEATURE [App::DocumentObjectGroupPython] N_element027  label="N_element : 0.757"  # scripted group (container) (typed FeaturePython)
  n = 0.035451
FEATURE [App::DocumentObjectGroupPython] O_element067  label="O_element : 0.880"  # scripted group (container) (typed FeaturePython)
  n = 0.710101
FEATURE [App::DocumentObjectGroupPython] G4_MUSCLE_WITH_SUCROSE  # scripted group (container) (typed FeaturePython)
  Dunit = g/cm3
  Dvalue = 1.11
  Group = -> [H_element059,C_element065,N_element027,O_element067]
  conduct = 2
  density = 1
  expand = 3
  formula = G4_MUSCLE_WITH_SUCROSE
  name = G4_MUSCLE_WITH_SUCROSE
  specific = 4
FEATURE [App::DocumentObjectGroupPython] H_element060  label="H_element : 0.138"  # scripted group (container) (typed FeaturePython)
  n = 0.101969
FEATURE [App::DocumentObjectGroupPython] C_element066  label="C_element : 0.120"  # scripted group (container) (typed FeaturePython)
  n = 0.120058
FEATURE [App::DocumentObjectGroupPython] N_element028  label="N_element : 0.758"  # scripted group (container) (typed FeaturePython)
  n = 0.035451
FEATURE [App::DocumentObjectGroupPython] O_element068  label="O_element : 0.743"  # scripted group (container) (typed FeaturePython)
  n = 0.742522
FEATURE [App::DocumentObjectGroupPython] G4_MUSCLE_WITHOUT_SUCROSE  # scripted group (container) (typed FeaturePython)
  Dunit = g/cm3
  Dvalue = 1.07
  Group = -> [H_element060,C_element066,N_element028,O_element068]
  conduct = 2
  density = 1
  expand = 3
  formula = G4_MUSCLE_WITHOUT_SUCROSE
  name = G4_MUSCLE_WITHOUT_SUCROSE
  specific = 4
FEATURE [App::DocumentObjectGroupPython] C_element067  label="C_element : 10"  # scripted group (container) (typed FeaturePython)
  n = 10
  ref = C_element
FEATURE [App::DocumentObjectGroupPython] H_element061  label="H_element : 030"  # scripted group (container) (typed FeaturePython)
  n = 8
  ref = H_element
FEATURE [App::DocumentObjectGroupPython] G4_NAPHTHALENE  # scripted group (container) (typed FeaturePython)
  Dunit = g/cm3
  Dvalue = 1.145
  Group = -> [C_element067,H_element061]
  conduct = 2
  density = 1
  expand = 3
  formula = G4_NAPHTHALENE
  name = G4_NAPHTHALENE
  specific = 4
FEATURE [App::DocumentObjectGroupPython] C_element068  label="C_element : 034"  # scripted group (container) (typed FeaturePython)
  n = 6
  ref = C_element
FEATURE [App::DocumentObjectGroupPython] H_element062  label="H_element : 031"  # scripted group (container) (typed FeaturePython)
  n = 5
  ref = H_element
FEATURE [App::DocumentObjectGroupPython] N_element029  label="N_element : 012"  # scripted group (container) (typed FeaturePython)
  n = 1
  ref = N_element
FEATURE [App::DocumentObjectGroupPython] O_element069  label="O_element : 034"  # scripted group (container) (typed FeaturePython)
  n = 2
  ref = O_element
FEATURE [App::DocumentObjectGroupPython] G4_NITROBENZENE  # scripted group (container) (typed FeaturePython)
  Dunit = g/cm3
  Dvalue = 1.19867
  Group = -> [C_element068,H_element062,N_element029,O_element069]
  conduct = 2
  density = 1
  expand = 3
  formula = G4_NITROBENZENE
  name = G4_NITROBENZENE
  specific = 4
FEATURE [App::DocumentObjectGroupPython] N_element030  label="N_element : 013"  # scripted group (container) (typed FeaturePython)
  n = 2
  ref = N_element
FEATURE [App::DocumentObjectGroupPython] O_element070  label="O_element : 035"  # scripted group (container) (typed FeaturePython)
  n = 1
  ref = O_element
FEATURE [App::DocumentObjectGroupPython] G4_NITROUS_OXIDE  # scripted group (container) (typed FeaturePython)
  Dunit = g/cm3
  Dvalue = 0.00183094
  Group = -> [N_element030,O_element070]
  conduct = 2
  density = 1
  expand = 3
  formula = G4_NITROUS_OXIDE
  name = G4_NITROUS_OXIDE
  specific = 4
FEATURE [App::DocumentObjectGroupPython] H_element063  label="H_element : 0.104"  # scripted group (container) (typed FeaturePython)
  n = 0.103509
FEATURE [App::DocumentObjectGroupPython] C_element069  label="C_element : 0.648"  # scripted group (container) (typed FeaturePython)
  n = 0.648416
FEATURE [App::DocumentObjectGroupPython] N_element031  label="N_element : 0.100"  # scripted group (container) (typed FeaturePython)
  n = 0.0995361
FEATURE [App::DocumentObjectGroupPython] O_element071  label="O_element : 0.149"  # scripted group (container) (typed FeaturePython)
  n = 0.148539
FEATURE [App::DocumentObjectGroupPython] G4_NYLON_8062  label="G4_NYLON-8062"  # scripted group (container) (typed FeaturePython)
  Dunit = g/cm3
  Dvalue = 1.08
  Group = -> [H_element063,C_element069,N_element031,O_element071]
  conduct = 2
  density = 1
  expand = 3
  formula = G4_NYLON-8062
  name = G4_NYLON-8062
  specific = 4
FEATURE [App::DocumentObjectGroupPython] C_element070  label="C_element : 035"  # scripted group (container) (typed FeaturePython)
  n = 6
  ref = C_element
FEATURE [App::DocumentObjectGroupPython] H_element064  label="H_element : 11"  # scripted group (container) (typed FeaturePython)
  n = 11
  ref = H_element
FEATURE [App::DocumentObjectGroupPython] N_element032  label="N_element : 014"  # scripted group (container) (typed FeaturePython)
  n = 1
  ref = N_element
FEATURE [App::DocumentObjectGroupPython] O_element072  label="O_element : 036"  # scripted group (container) (typed FeaturePython)
  n = 1
  ref = O_element
FEATURE [App::DocumentObjectGroupPython] G4_NYLON_6_6  label="G4_NYLON-6-6"  # scripted group (container) (typed FeaturePython)
  Dunit = g/cm3
  Dvalue = 1.14
  Group = -> [C_element070,H_element064,N_element032,O_element072]
  conduct = 2
  density = 1
  expand = 3
  formula = G4_NYLON-6-6
  name = G4_NYLON-6-6
  specific = 4
FEATURE [App::DocumentObjectGroupPython] H_element065  label="H_element : 0.139"  # scripted group (container) (typed FeaturePython)
  n = 0.107062
FEATURE [App::DocumentObjectGroupPython] C_element071  label="C_element : 0.680"  # scripted group (container) (typed FeaturePython)
  n = 0.680449
FEATURE [App::DocumentObjectGroupPython] N_element033  label="N_element : 0.099"  # scripted group (container) (typed FeaturePython)
  n = 0.099189
FEATURE [App::DocumentObjectGroupPython] O_element073  label="O_element : 0.113"  # scripted group (container) (typed FeaturePython)
  n = 0.1133
FEATURE [App::DocumentObjectGroupPython] G4_NYLON_6_10  label="G4_NYLON-6-10"  # scripted group (container) (typed FeaturePython)
  Dunit = g/cm3
  Dvalue = 1.14
  Group = -> [H_element065,C_element071,N_element033,O_element073]
  conduct = 2
  density = 1
  expand = 3
  formula = G4_NYLON-6-10
  name = G4_NYLON-6-10
  specific = 4
FEATURE [App::DocumentObjectGroupPython] H_element066  label="H_element : 0.140"  # scripted group (container) (typed FeaturePython)
  n = 0.115476
FEATURE [App::DocumentObjectGroupPython] C_element072  label="C_element : 0.721"  # scripted group (container) (typed FeaturePython)
  n = 0.720818
FEATURE [App::DocumentObjectGroupPython] N_element034  label="N_element : 0.076"  # scripted group (container) (typed FeaturePython)
  n = 0.0764169
FEATURE [App::DocumentObjectGroupPython] O_element074  label="O_element : 0.087"  # scripted group (container) (typed FeaturePython)
  n = 0.0872889
FEATURE [App::DocumentObjectGroupPython] G4_NYLON_11_RILSAN  label="G4_NYLON-11_RILSAN"  # scripted group (container) (typed FeaturePython)
  Dunit = g/cm3
  Dvalue = 1.425
  Group = -> [H_element066,C_element072,N_element034,O_element074]
  conduct = 2
  density = 1
  expand = 3
  formula = G4_NYLON-11_RILSAN
  name = G4_NYLON-11_RILSAN
  specific = 4
FEATURE [App::DocumentObjectGroupPython] C_element073  label="C_element : 8"  # scripted group (container) (typed FeaturePython)
  n = 8
  ref = C_element
FEATURE [App::DocumentObjectGroupPython] H_element067  label="H_element : 18"  # scripted group (container) (typed FeaturePython)
  n = 18
  ref = H_element
FEATURE [App::DocumentObjectGroupPython] G4_OCTANE  # scripted group (container) (typed FeaturePython)
  Dunit = g/cm3
  Dvalue = 0.7026
  Group = -> [C_element073,H_element067]
  conduct = 2
  density = 1
  expand = 3
  formula = G4_OCTANE
  name = G4_OCTANE
  specific = 4
FEATURE [App::DocumentObjectGroupPython] C_element074  label="C_element : 25"  # scripted group (container) (typed FeaturePython)
  n = 25
  ref = C_element
FEATURE [App::DocumentObjectGroupPython] H_element068  label="H_element : 52"  # scripted group (container) (typed FeaturePython)
  n = 52
  ref = H_element
FEATURE [App::DocumentObjectGroupPython] G4_PARAFFIN  # scripted group (container) (typed FeaturePython)
  Dunit = g/cm3
  Dvalue = 0.93
  Group = -> [C_element074,H_element068]
  conduct = 2
  density = 1
  expand = 3
  formula = G4_PARAFFIN
  name = G4_PARAFFIN
  specific = 4
FEATURE [App::DocumentObjectGroupPython] C_element075  label="C_element : 036"  # scripted group (container) (typed FeaturePython)
  n = 5
  ref = C_element
FEATURE [App::DocumentObjectGroupPython] H_element069  label="H_element : 032"  # scripted group (container) (typed FeaturePython)
  n = 12
  ref = H_element
FEATURE [App::DocumentObjectGroupPython] G4_N_PENTANE  label="G4_N-PENTANE"  # scripted group (container) (typed FeaturePython)
  Dunit = g/cm3
  Dvalue = 0.6262
  Group = -> [C_element075,H_element069]
  conduct = 2
  density = 1
  expand = 3
  formula = G4_N-PENTANE
  name = G4_N-PENTANE
  specific = 4
FEATURE [App::DocumentObjectGroupPython] H_element070  label="H_element : 0.014"  # scripted group (container) (typed FeaturePython)
  n = 0.0141
FEATURE [App::DocumentObjectGroupPython] C_element076  label="C_element : 0.072"  # scripted group (container) (typed FeaturePython)
  n = 0.072261
FEATURE [App::DocumentObjectGroupPython] N_element035  label="N_element : 0.019"  # scripted group (container) (typed FeaturePython)
  n = 0.01932
FEATURE [App::DocumentObjectGroupPython] O_element075  label="O_element : 0.066"  # scripted group (container) (typed FeaturePython)
  n = 0.066101
FEATURE [App::DocumentObjectGroupPython] S_element019  label="S_element : 0.020"  # scripted group (container) (typed FeaturePython)
  n = 0.00189
FEATURE [App::DocumentObjectGroupPython] Br_element004  label="Br_element : 0.349"  # scripted group (container) (typed FeaturePython)
  n = 0.349103
FEATURE [App::DocumentObjectGroupPython] Ag_element001  label="Ag_element : 0.474"  # scripted group (container) (typed FeaturePython)
  n = 0.474105
FEATURE [App::DocumentObjectGroupPython] I_element005  label="I_element : 0.003"  # scripted group (container) (typed FeaturePython)
  n = 0.00312
FEATURE [App::DocumentObjectGroupPython] G4_PHOTO_EMULSION  # scripted group (container) (typed FeaturePython)
  Dunit = g/cm3
  Dvalue = 3.815
  Group = -> [H_element070,C_element076,N_element035,O_element075,S_element019,Br_element004,Ag_element001,I_element005]
  conduct = 2
  density = 1
  expand = 3
  formula = G4_PHOTO_EMULSION
  name = G4_PHOTO_EMULSION
  specific = 4
FEATURE [App::DocumentObjectGroupPython] C_element077  label="C_element : 9"  # scripted group (container) (typed FeaturePython)
  n = 9
  ref = C_element
FEATURE [App::DocumentObjectGroupPython] H_element071  label="H_element : 033"  # scripted group (container) (typed FeaturePython)
  n = 10
  ref = H_element
FEATURE [App::DocumentObjectGroupPython] G4_PLASTIC_SC_VINYLTOLUENE  # scripted group (container) (typed FeaturePython)
  Dunit = g/cm3
  Dvalue = 1.032
  Group = -> [C_element077,H_element071]
  conduct = 2
  density = 1
  expand = 3
  formula = G4_PLASTIC_SC_VINYLTOLUENE
  name = G4_PLASTIC_SC_VINYLTOLUENE
  specific = 4
FEATURE [App::DocumentObjectGroupPython] Pu_element001  label="Pu_element : 1"  # scripted group (container) (typed FeaturePython)
  n = 1
  ref = Pu_element
FEATURE [App::DocumentObjectGroupPython] O_element076  label="O_element : 037"  # scripted group (container) (typed FeaturePython)
  n = 2
  ref = O_element
FEATURE [App::DocumentObjectGroupPython] G4_PLUTONIUM_DIOXIDE  # scripted group (container) (typed FeaturePython)
  Dunit = g/cm3
  Dvalue = 11.46
  Group = -> [Pu_element001,O_element076]
  conduct = 2
  density = 1
  expand = 3
  formula = G4_PLUTONIUM_DIOXIDE
  name = G4_PLUTONIUM_DIOXIDE
  specific = 4
FEATURE [App::DocumentObjectGroupPython] C_element078  label="C_element : 037"  # scripted group (container) (typed FeaturePython)
  n = 3
  ref = C_element
FEATURE [App::DocumentObjectGroupPython] H_element072  label="H_element : 034"  # scripted group (container) (typed FeaturePython)
  n = 3
  ref = H_element
FEATURE [App::DocumentObjectGroupPython] N_element036  label="N_element : 015"  # scripted group (container) (typed FeaturePython)
  n = 1
  ref = N_element
FEATURE [App::DocumentObjectGroupPython] G4_POLYACRYLONITRILE  # scripted group (container) (typed FeaturePython)
  Dunit = g/cm3
  Dvalue = 1.17
  Group = -> [C_element078,H_element072,N_element036]
  conduct = 2
  density = 1
  expand = 3
  formula = G4_POLYACRYLONITRILE
  name = G4_POLYACRYLONITRILE
  specific = 4
FEATURE [App::DocumentObjectGroupPython] C_element079  label="C_element : 16"  # scripted group (container) (typed FeaturePython)
  n = 16
  ref = C_element
FEATURE [App::DocumentObjectGroupPython] H_element073  label="H_element : 035"  # scripted group (container) (typed FeaturePython)
  n = 14
  ref = H_element
FEATURE [App::DocumentObjectGroupPython] O_element077  label="O_element : 038"  # scripted group (container) (typed FeaturePython)
  n = 3
  ref = O_element
FEATURE [App::DocumentObjectGroupPython] G4_POLYCARBONATE  # scripted group (container) (typed FeaturePython)
  Dunit = g/cm3
  Dvalue = 1.2
  Group = -> [C_element079,H_element073,O_element077]
  conduct = 2
  density = 1
  expand = 3
  formula = G4_POLYCARBONATE
  name = G4_POLYCARBONATE
  specific = 4
FEATURE [App::DocumentObjectGroupPython] C_element080  label="C_element : 038"  # scripted group (container) (typed FeaturePython)
  n = 8
  ref = C_element
FEATURE [App::DocumentObjectGroupPython] H_element074  label="H_element : 036"  # scripted group (container) (typed FeaturePython)
  n = 7
  ref = H_element
FEATURE [App::DocumentObjectGroupPython] Cl_element017  label="Cl_element : 007"  # scripted group (container) (typed FeaturePython)
  n = 1
  ref = Cl_element
FEATURE [App::DocumentObjectGroupPython] G4_POLYCHLOROSTYRENE  # scripted group (container) (typed FeaturePython)
  Dunit = g/cm3
  Dvalue = 1.3
  Group = -> [C_element080,H_element074,Cl_element017]
  conduct = 2
  density = 1
  expand = 3
  formula = G4_POLYCHLOROSTYRENE
  name = G4_POLYCHLOROSTYRENE
  specific = 4
FEATURE [App::DocumentObjectGroupPython] C_element081  label="C_element : 039"  # scripted group (container) (typed FeaturePython)
  n = 1
  ref = C_element
FEATURE [App::DocumentObjectGroupPython] H_element075  label="H_element : 037"  # scripted group (container) (typed FeaturePython)
  n = 2
  ref = H_element
FEATURE [App::DocumentObjectGroupPython] G4_POLYETHYLENE  # scripted group (container) (typed FeaturePython)
  Dunit = g/cm3
  Dvalue = 0.94
  Group = -> [C_element081,H_element075]
  conduct = 2
  density = 1
  expand = 3
  formula = G4_POLYETHYLENE
  name = G4_POLYETHYLENE
  specific = 4
FEATURE [App::DocumentObjectGroupPython] C_element082  label="C_element : 040"  # scripted group (container) (typed FeaturePython)
  n = 10
  ref = C_element
FEATURE [App::DocumentObjectGroupPython] H_element076  label="H_element : 038"  # scripted group (container) (typed FeaturePython)
  n = 8
  ref = H_element
FEATURE [App::DocumentObjectGroupPython] O_element078  label="O_element : 039"  # scripted group (container) (typed FeaturePython)
  n = 4
  ref = O_element
FEATURE [App::DocumentObjectGroupPython] G4_MYLAR  # scripted group (container) (typed FeaturePython)
  Dunit = g/cm3
  Dvalue = 1.4
  Group = -> [C_element082,H_element076,O_element078]
  conduct = 2
  density = 1
  expand = 3
  formula = G4_MYLAR
  name = G4_MYLAR
  specific = 4
FEATURE [App::DocumentObjectGroupPython] C_element083  label="C_element : 041"  # scripted group (container) (typed FeaturePython)
  n = 5
  ref = C_element
FEATURE [App::DocumentObjectGroupPython] H_element077  label="H_element : 039"  # scripted group (container) (typed FeaturePython)
  n = 8
  ref = H_element
FEATURE [App::DocumentObjectGroupPython] O_element079  label="O_element : 040"  # scripted group (container) (typed FeaturePython)
  n = 2
  ref = O_element
FEATURE [App::DocumentObjectGroupPython] G4_PLEXIGLASS  # scripted group (container) (typed FeaturePython)
  Dunit = g/cm3
  Dvalue = 1.19
  Group = -> [C_element083,H_element077,O_element079]
  conduct = 2
  density = 1
  expand = 3
  formula = G4_PLEXIGLASS
  name = G4_PLEXIGLASS
  specific = 4
FEATURE [App::DocumentObjectGroupPython] C_element084  label="C_element : 042"  # scripted group (container) (typed FeaturePython)
  n = 1
  ref = C_element
FEATURE [App::DocumentObjectGroupPython] H_element078  label="H_element : 040"  # scripted group (container) (typed FeaturePython)
  n = 2
  ref = H_element
FEATURE [App::DocumentObjectGroupPython] O_element080  label="O_element : 041"  # scripted group (container) (typed FeaturePython)
  n = 1
  ref = O_element
FEATURE [App::DocumentObjectGroupPython] G4_POLYOXYMETHYLENE  # scripted group (container) (typed FeaturePython)
  Dunit = g/cm3
  Dvalue = 1.425
  Group = -> [C_element084,H_element078,O_element080]
  conduct = 2
  density = 1
  expand = 3
  formula = G4_POLYOXYMETHYLENE
  name = G4_POLYOXYMETHYLENE
  specific = 4
FEATURE [App::DocumentObjectGroupPython] C_element085  label="C_element : 043"  # scripted group (container) (typed FeaturePython)
  n = 2
  ref = C_element
FEATURE [App::DocumentObjectGroupPython] H_element079  label="H_element : 041"  # scripted group (container) (typed FeaturePython)
  n = 4
  ref = H_element
FEATURE [App::DocumentObjectGroupPython] G4_POLYPROPYLENE  # scripted group (container) (typed FeaturePython)
  Dunit = g/cm3
  Dvalue = 0.9
  Group = -> [C_element085,H_element079]
  conduct = 2
  density = 1
  expand = 3
  formula = G4_POLYPROPYLENE
  name = G4_POLYPROPYLENE
  specific = 4
FEATURE [App::DocumentObjectGroupPython] C_element086  label="C_element : 044"  # scripted group (container) (typed FeaturePython)
  n = 8
  ref = C_element
FEATURE [App::DocumentObjectGroupPython] H_element080  label="H_element : 042"  # scripted group (container) (typed FeaturePython)
  n = 8
  ref = H_element
FEATURE [App::DocumentObjectGroupPython] G4_POLYSTYRENE  # scripted group (container) (typed FeaturePython)
  Dunit = g/cm3
  Dvalue = 1.06
  Group = -> [C_element086,H_element080]
  conduct = 2
  density = 1
  expand = 3
  formula = G4_POLYSTYRENE
  name = G4_POLYSTYRENE
  specific = 4
FEATURE [App::DocumentObjectGroupPython] C_element087  label="C_element : 045"  # scripted group (container) (typed FeaturePython)
  n = 2
  ref = C_element
FEATURE [App::DocumentObjectGroupPython] F_element014  label="F_element : 4"  # scripted group (container) (typed FeaturePython)
  n = 4
  ref = F_element
FEATURE [App::DocumentObjectGroupPython] G4_TEFLON  # scripted group (container) (typed FeaturePython)
  Dunit = g/cm3
  Dvalue = 2.2
  Group = -> [C_element087,F_element014]
  conduct = 2
  density = 1
  expand = 3
  formula = G4_TEFLON
  name = G4_TEFLON
  specific = 4
FEATURE [App::DocumentObjectGroupPython] C_element088  label="C_element : 046"  # scripted group (container) (typed FeaturePython)
  n = 2
  ref = C_element
FEATURE [App::DocumentObjectGroupPython] F_element015  label="F_element : 006"  # scripted group (container) (typed FeaturePython)
  n = 3
  ref = F_element
FEATURE [App::DocumentObjectGroupPython] Cl_element018  label="Cl_element : 008"  # scripted group (container) (typed FeaturePython)
  n = 1
  ref = Cl_element
FEATURE [App::DocumentObjectGroupPython] G4_POLYTRIFLUOROCHLOROETHYLENE  # scripted group (container) (typed FeaturePython)
  Dunit = g/cm3
  Dvalue = 2.1
  Group = -> [C_element088,F_element015,Cl_element018]
  conduct = 2
  density = 1
  expand = 3
  formula = G4_POLYTRIFLUOROCHLOROETHYLENE
  name = G4_POLYTRIFLUOROCHLOROETHYLENE
  specific = 4
FEATURE [App::DocumentObjectGroupPython] C_element089  label="C_element : 047"  # scripted group (container) (typed FeaturePython)
  n = 4
  ref = C_element
FEATURE [App::DocumentObjectGroupPython] H_element081  label="H_element : 043"  # scripted group (container) (typed FeaturePython)
  n = 6
  ref = H_element
FEATURE [App::DocumentObjectGroupPython] O_element081  label="O_element : 042"  # scripted group (container) (typed FeaturePython)
  n = 2
  ref = O_element
FEATURE [App::DocumentObjectGroupPython] G4_POLYVINYL_ACETATE  # scripted group (container) (typed FeaturePython)
  Dunit = g/cm3
  Dvalue = 1.19
  Group = -> [C_element089,H_element081,O_element081]
  conduct = 2
  density = 1
  expand = 3
  formula = G4_POLYVINYL_ACETATE
  name = G4_POLYVINYL_ACETATE
  specific = 4
FEATURE [App::DocumentObjectGroupPython] C_element090  label="C_element : 048"  # scripted group (container) (typed FeaturePython)
  n = 2
  ref = C_element
FEATURE [App::DocumentObjectGroupPython] H_element082  label="H_element : 044"  # scripted group (container) (typed FeaturePython)
  n = 4
  ref = H_element
FEATURE [App::DocumentObjectGroupPython] O_element082  label="O_element : 043"  # scripted group (container) (typed FeaturePython)
  n = 1
  ref = O_element
FEATURE [App::DocumentObjectGroupPython] G4_POLYVINYL_ALCOHOL  # scripted group (container) (typed FeaturePython)
  Dunit = g/cm3
  Dvalue = 1.3
  Group = -> [C_element090,H_element082,O_element082]
  conduct = 2
  density = 1
  expand = 3
  formula = G4_POLYVINYL_ALCOHOL
  name = G4_POLYVINYL_ALCOHOL
  specific = 4
FEATURE [App::DocumentObjectGroupPython] C_element091  label="C_element : 049"  # scripted group (container) (typed FeaturePython)
  n = 8
  ref = C_element
FEATURE [App::DocumentObjectGroupPython] H_element083  label="H_element : 045"  # scripted group (container) (typed FeaturePython)
  n = 14
  ref = H_element
FEATURE [App::DocumentObjectGroupPython] O_element083  label="O_element : 044"  # scripted group (container) (typed FeaturePython)
  n = 2
  ref = O_element
FEATURE [App::DocumentObjectGroupPython] G4_POLYVINYL_BUTYRAL  # scripted group (container) (typed FeaturePython)
  Dunit = g/cm3
  Dvalue = 1.12
  Group = -> [C_element091,H_element083,O_element083]
  conduct = 2
  density = 1
  expand = 3
  formula = G4_POLYVINYL_BUTYRAL
  name = G4_POLYVINYL_BUTYRAL
  specific = 4
FEATURE [App::DocumentObjectGroupPython] C_element092  label="C_element : 050"  # scripted group (container) (typed FeaturePython)
  n = 2
  ref = C_element
FEATURE [App::DocumentObjectGroupPython] H_element084  label="H_element : 046"  # scripted group (container) (typed FeaturePython)
  n = 3
  ref = H_element
FEATURE [App::DocumentObjectGroupPython] Cl_element019  label="Cl_element : 009"  # scripted group (container) (typed FeaturePython)
  n = 1
  ref = Cl_element
FEATURE [App::DocumentObjectGroupPython] G4_POLYVINYL_CHLORIDE  # scripted group (container) (typed FeaturePython)
  Dunit = g/cm3
  Dvalue = 1.3
  Group = -> [C_element092,H_element084,Cl_element019]
  conduct = 2
  density = 1
  expand = 3
  formula = G4_POLYVINYL_CHLORIDE
  name = G4_POLYVINYL_CHLORIDE
  specific = 4
FEATURE [App::DocumentObjectGroupPython] C_element093  label="C_element : 051"  # scripted group (container) (typed FeaturePython)
  n = 2
  ref = C_element
FEATURE [App::DocumentObjectGroupPython] H_element085  label="H_element : 047"  # scripted group (container) (typed FeaturePython)
  n = 2
  ref = H_element
FEATURE [App::DocumentObjectGroupPython] Cl_element020  label="Cl_element : 010"  # scripted group (container) (typed FeaturePython)
  n = 2
  ref = Cl_element
FEATURE [App::DocumentObjectGroupPython] G4_POLYVINYLIDENE_CHLORIDE  # scripted group (container) (typed FeaturePython)
  Dunit = g/cm3
  Dvalue = 1.7
  Group = -> [C_element093,H_element085,Cl_element020]
  conduct = 2
  density = 1
  expand = 3
  formula = G4_POLYVINYLIDENE_CHLORIDE
  name = G4_POLYVINYLIDENE_CHLORIDE
  specific = 4
FEATURE [App::DocumentObjectGroupPython] C_element094  label="C_element : 052"  # scripted group (container) (typed FeaturePython)
  n = 2
  ref = C_element
FEATURE [App::DocumentObjectGroupPython] H_element086  label="H_element : 048"  # scripted group (container) (typed FeaturePython)
  n = 2
  ref = H_element
FEATURE [App::DocumentObjectGroupPython] F_element016  label="F_element : 007"  # scripted group (container) (typed FeaturePython)
  n = 2
  ref = F_element
FEATURE [App::DocumentObjectGroupPython] G4_POLYVINYLIDENE_FLUORIDE  # scripted group (container) (typed FeaturePython)
  Dunit = g/cm3
  Dvalue = 1.76
  Group = -> [C_element094,H_element086,F_element016]
  conduct = 2
  density = 1
  expand = 3
  formula = G4_POLYVINYLIDENE_FLUORIDE
  name = G4_POLYVINYLIDENE_FLUORIDE
  specific = 4
FEATURE [App::DocumentObjectGroupPython] C_element095  label="C_element : 053"  # scripted group (container) (typed FeaturePython)
  n = 6
  ref = C_element
FEATURE [App::DocumentObjectGroupPython] H_element087  label="H_element : 9"  # scripted group (container) (typed FeaturePython)
  n = 9
  ref = H_element
FEATURE [App::DocumentObjectGroupPython] N_element037  label="N_element : 016"  # scripted group (container) (typed FeaturePython)
  n = 1
  ref = N_element
FEATURE [App::DocumentObjectGroupPython] O_element084  label="O_element : 045"  # scripted group (container) (typed FeaturePython)
  n = 1
  ref = O_element
FEATURE [App::DocumentObjectGroupPython] G4_POLYVINYL_PYRROLIDONE  # scripted group (container) (typed FeaturePython)
  Dunit = g/cm3
  Dvalue = 1.25
  Group = -> [C_element095,H_element087,N_element037,O_element084]
  conduct = 2
  density = 1
  expand = 3
  formula = G4_POLYVINYL_PYRROLIDONE
  name = G4_POLYVINYL_PYRROLIDONE
  specific = 4
FEATURE [App::DocumentObjectGroupPython] K_element008  label="K_element : 1"  # scripted group (container) (typed FeaturePython)
  n = 1
  ref = K_element
FEATURE [App::DocumentObjectGroupPython] I_element006  label="I_element : 003"  # scripted group (container) (typed FeaturePython)
  n = 1
  ref = I_element
FEATURE [App::DocumentObjectGroupPython] G4_POTASSIUM_IODIDE  # scripted group (container) (typed FeaturePython)
  Dunit = g/cm3
  Dvalue = 3.13
  Group = -> [K_element008,I_element006]
  conduct = 2
  density = 1
  expand = 3
  formula = G4_POTASSIUM_IODIDE
  name = G4_POTASSIUM_IODIDE
  specific = 4
FEATURE [App::DocumentObjectGroupPython] K_element009  label="K_element : 2"  # scripted group (container) (typed FeaturePython)
  n = 2
  ref = K_element
FEATURE [App::DocumentObjectGroupPython] O_element085  label="O_element : 046"  # scripted group (container) (typed FeaturePython)
  n = 1
  ref = O_element
FEATURE [App::DocumentObjectGroupPython] G4_POTASSIUM_OXIDE  # scripted group (container) (typed FeaturePython)
  Dunit = g/cm3
  Dvalue = 2.32
  Group = -> [K_element009,O_element085]
  conduct = 2
  density = 1
  expand = 3
  formula = G4_POTASSIUM_OXIDE
  name = G4_POTASSIUM_OXIDE
  specific = 4
FEATURE [App::DocumentObjectGroupPython] C_element096  label="C_element : 054"  # scripted group (container) (typed FeaturePython)
  n = 3
  ref = C_element
FEATURE [App::DocumentObjectGroupPython] H_element088  label="H_element : 049"  # scripted group (container) (typed FeaturePython)
  n = 8
  ref = H_element
FEATURE [App::DocumentObjectGroupPython] G4_PROPANE  # scripted group (container) (typed FeaturePython)
  Dunit = g/cm3
  Dvalue = 0.00187939
  Group = -> [C_element096,H_element088]
  conduct = 2
  density = 1
  expand = 3
  formula = G4_PROPANE
  name = G4_PROPANE
  specific = 4
FEATURE [App::DocumentObjectGroupPython] C_element097  label="C_element : 055"  # scripted group (container) (typed FeaturePython)
  n = 3
  ref = C_element
FEATURE [App::DocumentObjectGroupPython] H_element089  label="H_element : 050"  # scripted group (container) (typed FeaturePython)
  n = 8
  ref = H_element
FEATURE [App::DocumentObjectGroupPython] G4_lPROPANE  # scripted group (container) (typed FeaturePython)
  Dunit = g/cm3
  Dvalue = 0.43
  Group = -> [C_element097,H_element089]
  conduct = 2
  density = 1
  expand = 3
  formula = G4_lPROPANE
  name = G4_lPROPANE
  specific = 4
FEATURE [App::DocumentObjectGroupPython] C_element098  label="C_element : 056"  # scripted group (container) (typed FeaturePython)
  n = 3
  ref = C_element
FEATURE [App::DocumentObjectGroupPython] H_element090  label="H_element : 051"  # scripted group (container) (typed FeaturePython)
  n = 8
  ref = H_element
FEATURE [App::DocumentObjectGroupPython] O_element086  label="O_element : 047"  # scripted group (container) (typed FeaturePython)
  n = 1
  ref = O_element
FEATURE [App::DocumentObjectGroupPython] G4_N_PROPYL_ALCOHOL  label="G4_N-PROPYL_ALCOHOL"  # scripted group (container) (typed FeaturePython)
  Dunit = g/cm3
  Dvalue = 0.8035
  Group = -> [C_element098,H_element090,O_element086]
  conduct = 2
  density = 1
  expand = 3
  formula = G4_N-PROPYL_ALCOHOL
  name = G4_N-PROPYL_ALCOHOL
  specific = 4
FEATURE [App::DocumentObjectGroupPython] C_element099  label="C_element : 057"  # scripted group (container) (typed FeaturePython)
  n = 5
  ref = C_element
FEATURE [App::DocumentObjectGroupPython] H_element091  label="H_element : 052"  # scripted group (container) (typed FeaturePython)
  n = 5
  ref = H_element
FEATURE [App::DocumentObjectGroupPython] N_element038  label="N_element : 017"  # scripted group (container) (typed FeaturePython)
  n = 1
  ref = N_element
FEATURE [App::DocumentObjectGroupPython] G4_PYRIDINE  # scripted group (container) (typed FeaturePython)
  Dunit = g/cm3
  Dvalue = 0.9819
  Group = -> [C_element099,H_element091,N_element038]
  conduct = 2
  density = 1
  expand = 3
  formula = G4_PYRIDINE
  name = G4_PYRIDINE
  specific = 4
FEATURE [App::DocumentObjectGroupPython] H_element092  label="H_element : 0.144"  # scripted group (container) (typed FeaturePython)
  n = 0.143711
FEATURE [App::DocumentObjectGroupPython] C_element100  label="C_element : 0.856"  # scripted group (container) (typed FeaturePython)
  n = 0.856289
FEATURE [App::DocumentObjectGroupPython] G4_RUBBER_BUTYL  # scripted group (container) (typed FeaturePython)
  Dunit = g/cm3
  Dvalue = 0.92
  Group = -> [H_element092,C_element100]
  conduct = 2
  density = 1
  expand = 3
  formula = G4_RUBBER_BUTYL
  name = G4_RUBBER_BUTYL
  specific = 4
FEATURE [App::DocumentObjectGroupPython] H_element093  label="H_element : 0.118"  # scripted group (container) (typed FeaturePython)
  n = 0.118371
FEATURE [App::DocumentObjectGroupPython] C_element101  label="C_element : 0.882"  # scripted group (container) (typed FeaturePython)
  n = 0.881629
FEATURE [App::DocumentObjectGroupPython] G4_RUBBER_NATURAL  # scripted group (container) (typed FeaturePython)
  Dunit = g/cm3
  Dvalue = 0.92
  Group = -> [H_element093,C_element101]
  conduct = 2
  density = 1
  expand = 3
  formula = G4_RUBBER_NATURAL
  name = G4_RUBBER_NATURAL
  specific = 4
FEATURE [App::DocumentObjectGroupPython] H_element094  label="H_element : 0.145"  # scripted group (container) (typed FeaturePython)
  n = 0.05692
FEATURE [App::DocumentObjectGroupPython] C_element102  label="C_element : 0.543"  # scripted group (container) (typed FeaturePython)
  n = 0.542646
FEATURE [App::DocumentObjectGroupPython] Cl_element021  label="Cl_element : 0.400"  # scripted group (container) (typed FeaturePython)
  n = 0.400434
FEATURE [App::DocumentObjectGroupPython] G4_RUBBER_NEOPRENE  # scripted group (container) (typed FeaturePython)
  Dunit = g/cm3
  Dvalue = 1.23
  Group = -> [H_element094,C_element102,Cl_element021]
  conduct = 2
  density = 1
  expand = 3
  formula = G4_RUBBER_NEOPRENE
  name = G4_RUBBER_NEOPRENE
  specific = 4
FEATURE [App::DocumentObjectGroupPython] Si_element006  label="Si_element : 1"  # scripted group (container) (typed FeaturePython)
  n = 1
  ref = Si_element
FEATURE [App::DocumentObjectGroupPython] O_element087  label="O_element : 048"  # scripted group (container) (typed FeaturePython)
  n = 2
  ref = O_element
FEATURE [App::DocumentObjectGroupPython] G4_SILICON_DIOXIDE  # scripted group (container) (typed FeaturePython)
  Dunit = g/cm3
  Dvalue = 2.32
  Group = -> [Si_element006,O_element087]
  conduct = 2
  density = 1
  expand = 3
  formula = G4_SILICON_DIOXIDE
  name = G4_SILICON_DIOXIDE
  specific = 4
FEATURE [App::DocumentObjectGroupPython] Ag_element002  label="Ag_element : 1"  # scripted group (container) (typed FeaturePython)
  n = 1
  ref = Ag_element
FEATURE [App::DocumentObjectGroupPython] Br_element005  label="Br_element : 003"  # scripted group (container) (typed FeaturePython)
  n = 1
  ref = Br_element
FEATURE [App::DocumentObjectGroupPython] G4_SILVER_BROMIDE  # scripted group (container) (typed FeaturePython)
  Dunit = g/cm3
  Dvalue = 6.473
  Group = -> [Ag_element002,Br_element005]
  conduct = 2
  density = 1
  expand = 3
  formula = G4_SILVER_BROMIDE
  name = G4_SILVER_BROMIDE
  specific = 4
FEATURE [App::DocumentObjectGroupPython] Ag_element003  label="Ag_element : 002"  # scripted group (container) (typed FeaturePython)
  n = 1
  ref = Ag_element
FEATURE [App::DocumentObjectGroupPython] Cl_element022  label="Cl_element : 011"  # scripted group (container) (typed FeaturePython)
  n = 1
  ref = Cl_element
FEATURE [App::DocumentObjectGroupPython] G4_SILVER_CHLORIDE  # scripted group (container) (typed FeaturePython)
  Dunit = g/cm3
  Dvalue = 5.56
  Group = -> [Ag_element003,Cl_element022]
  conduct = 2
  density = 1
  expand = 3
  formula = G4_SILVER_CHLORIDE
  name = G4_SILVER_CHLORIDE
  specific = 4
FEATURE [App::DocumentObjectGroupPython] Br_element006  label="Br_element : 0.423"  # scripted group (container) (typed FeaturePython)
  n = 0.422895
FEATURE [App::DocumentObjectGroupPython] Ag_element004  label="Ag_element : 0.574"  # scripted group (container) (typed FeaturePython)
  n = 0.573748
FEATURE [App::DocumentObjectGroupPython] I_element007  label="I_element : 0.649"  # scripted group (container) (typed FeaturePython)
  n = 0.003357
FEATURE [App::DocumentObjectGroupPython] G4_SILVER_HALIDES  # scripted group (container) (typed FeaturePython)
  Dunit = g/cm3
  Dvalue = 6.47
  Group = -> [Br_element006,Ag_element004,I_element007]
  conduct = 2
  density = 1
  expand = 3
  formula = G4_SILVER_HALIDES
  name = G4_SILVER_HALIDES
  specific = 4
FEATURE [App::DocumentObjectGroupPython] Ag_element005  label="Ag_element : 003"  # scripted group (container) (typed FeaturePython)
  n = 1
  ref = Ag_element
FEATURE [App::DocumentObjectGroupPython] I_element008  label="I_element : 004"  # scripted group (container) (typed FeaturePython)
  n = 1
  ref = I_element
FEATURE [App::DocumentObjectGroupPython] G4_SILVER_IODIDE  # scripted group (container) (typed FeaturePython)
  Dunit = g/cm3
  Dvalue = 6.01
  Group = -> [Ag_element005,I_element008]
  conduct = 2
  density = 1
  expand = 3
  formula = G4_SILVER_IODIDE
  name = G4_SILVER_IODIDE
  specific = 4
FEATURE [App::DocumentObjectGroupPython] H_element095  label="H_element : 0.100"  # scripted group (container) (typed FeaturePython)
  n = 0.1
FEATURE [App::DocumentObjectGroupPython] C_element103  label="C_element : 0.204"  # scripted group (container) (typed FeaturePython)
  n = 0.204
FEATURE [App::DocumentObjectGroupPython] N_element039  label="N_element : 0.759"  # scripted group (container) (typed FeaturePython)
  n = 0.042
FEATURE [App::DocumentObjectGroupPython] O_element088  label="O_element : 0.645"  # scripted group (container) (typed FeaturePython)
  n = 0.645
FEATURE [App::DocumentObjectGroupPython] Na_element013  label="Na_element : 0.100"  # scripted group (container) (typed FeaturePython)
  n = 0.002
FEATURE [App::DocumentObjectGroupPython] P_element009  label="P_element : 0.107"  # scripted group (container) (typed FeaturePython)
  n = 0.001
FEATURE [App::DocumentObjectGroupPython] S_element020  label="S_element : 0.021"  # scripted group (container) (typed FeaturePython)
  n = 0.002
FEATURE [App::DocumentObjectGroupPython] Cl_element023  label="Cl_element : 0.590"  # scripted group (container) (typed FeaturePython)
  n = 0.003
FEATURE [App::DocumentObjectGroupPython] K_element010  label="K_element : 0.001"  # scripted group (container) (typed FeaturePython)
  n = 0.001
FEATURE [App::DocumentObjectGroupPython] G4_SKIN_ICRP  # scripted group (container) (typed FeaturePython)
  Dunit = g/cm3
  Dvalue = 1.09
  Group = -> [H_element095,C_element103,N_element039,O_element088,Na_element013,P_element009,S_element020,Cl_element023,K_element010]
  conduct = 2
  density = 1
  expand = 3
  formula = G4_SKIN_ICRP
  name = G4_SKIN_ICRP
  specific = 4
FEATURE [App::DocumentObjectGroupPython] Na_element014  label="Na_element : 2"  # scripted group (container) (typed FeaturePython)
  n = 2
  ref = Na_element
FEATURE [App::DocumentObjectGroupPython] C_element104  label="C_element : 058"  # scripted group (container) (typed FeaturePython)
  n = 1
  ref = C_element
FEATURE [App::DocumentObjectGroupPython] O_element089  label="O_element : 049"  # scripted group (container) (typed FeaturePython)
  n = 3
  ref = O_element
FEATURE [App::DocumentObjectGroupPython] G4_SODIUM_CARBONATE  # scripted group (container) (typed FeaturePython)
  Dunit = g/cm3
  Dvalue = 2.532
  Group = -> [Na_element014,C_element104,O_element089]
  conduct = 2
  density = 1
  expand = 3
  formula = G4_SODIUM_CARBONATE
  name = G4_SODIUM_CARBONATE
  specific = 4
FEATURE [App::DocumentObjectGroupPython] Na_element015  label="Na_element : 1"  # scripted group (container) (typed FeaturePython)
  n = 1
  ref = Na_element
FEATURE [App::DocumentObjectGroupPython] I_element009  label="I_element : 005"  # scripted group (container) (typed FeaturePython)
  n = 1
  ref = I_element
FEATURE [App::DocumentObjectGroupPython] G4_SODIUM_IODIDE  # scripted group (container) (typed FeaturePython)
  Dunit = g/cm3
  Dvalue = 3.667
  Group = -> [Na_element015,I_element009]
  conduct = 2
  density = 1
  expand = 3
  formula = G4_SODIUM_IODIDE
  name = G4_SODIUM_IODIDE
  specific = 4
FEATURE [App::DocumentObjectGroupPython] Na_element016  label="Na_element : 003"  # scripted group (container) (typed FeaturePython)
  n = 2
  ref = Na_element
FEATURE [App::DocumentObjectGroupPython] O_element090  label="O_element : 050"  # scripted group (container) (typed FeaturePython)
  n = 1
  ref = O_element
FEATURE [App::DocumentObjectGroupPython] G4_SODIUM_MONOXIDE  # scripted group (container) (typed FeaturePython)
  Dunit = g/cm3
  Dvalue = 2.27
  Group = -> [Na_element016,O_element090]
  conduct = 2
  density = 1
  expand = 3
  formula = G4_SODIUM_MONOXIDE
  name = G4_SODIUM_MONOXIDE
  specific = 4
FEATURE [App::DocumentObjectGroupPython] Na_element017  label="Na_element : 004"  # scripted group (container) (typed FeaturePython)
  n = 1
  ref = Na_element
FEATURE [App::DocumentObjectGroupPython] N_element040  label="N_element : 018"  # scripted group (container) (typed FeaturePython)
  n = 1
  ref = N_element
FEATURE [App::DocumentObjectGroupPython] O_element091  label="O_element : 051"  # scripted group (container) (typed FeaturePython)
  n = 3
  ref = O_element
FEATURE [App::DocumentObjectGroupPython] G4_SODIUM_NITRATE  # scripted group (container) (typed FeaturePython)
  Dunit = g/cm3
  Dvalue = 2.261
  Group = -> [Na_element017,N_element040,O_element091]
  conduct = 2
  density = 1
  expand = 3
  formula = G4_SODIUM_NITRATE
  name = G4_SODIUM_NITRATE
  specific = 4
FEATURE [App::DocumentObjectGroupPython] C_element105  label="C_element : 059"  # scripted group (container) (typed FeaturePython)
  n = 14
  ref = C_element
FEATURE [App::DocumentObjectGroupPython] H_element096  label="H_element : 053"  # scripted group (container) (typed FeaturePython)
  n = 12
  ref = H_element
FEATURE [App::DocumentObjectGroupPython] G4_STILBENE  # scripted group (container) (typed FeaturePython)
  Dunit = g/cm3
  Dvalue = 0.9707
  Group = -> [C_element105,H_element096]
  conduct = 2
  density = 1
  expand = 3
  formula = G4_STILBENE
  name = G4_STILBENE
  specific = 4
FEATURE [App::DocumentObjectGroupPython] C_element106  label="C_element : 12"  # scripted group (container) (typed FeaturePython)
  n = 12
  ref = C_element
FEATURE [App::DocumentObjectGroupPython] H_element097  label="H_element : 22"  # scripted group (container) (typed FeaturePython)
  n = 22
  ref = H_element
FEATURE [App::DocumentObjectGroupPython] O_element092  label="O_element : 11"  # scripted group (container) (typed FeaturePython)
  n = 11
  ref = O_element
FEATURE [App::DocumentObjectGroupPython] G4_SUCROSE  # scripted group (container) (typed FeaturePython)
  Dunit = g/cm3
  Dvalue = 1.5805
  Group = -> [C_element106,H_element097,O_element092]
  conduct = 2
  density = 1
  expand = 3
  formula = G4_SUCROSE
  name = G4_SUCROSE
  specific = 4
FEATURE [App::DocumentObjectGroupPython] C_element107  label="C_element : 18"  # scripted group (container) (typed FeaturePython)
  n = 18
  ref = C_element
FEATURE [App::DocumentObjectGroupPython] H_element098  label="H_element : 054"  # scripted group (container) (typed FeaturePython)
  n = 14
  ref = H_element
FEATURE [App::DocumentObjectGroupPython] G4_TERPHENYL  # scripted group (container) (typed FeaturePython)
  Dunit = g/cm3
  Dvalue = 1.24
  Group = -> [C_element107,H_element098]
  conduct = 2
  density = 1
  expand = 3
  formula = G4_TERPHENYL
  name = G4_TERPHENYL
  specific = 4
FEATURE [App::DocumentObjectGroupPython] H_element099  label="H_element : 0.146"  # scripted group (container) (typed FeaturePython)
  n = 0.106
FEATURE [App::DocumentObjectGroupPython] C_element108  label="C_element : 0.883"  # scripted group (container) (typed FeaturePython)
  n = 0.099
FEATURE [App::DocumentObjectGroupPython] N_element041  label="N_element : 0.020"  # scripted group (container) (typed FeaturePython)
  n = 0.02
FEATURE [App::DocumentObjectGroupPython] O_element093  label="O_element : 0.766"  # scripted group (container) (typed FeaturePython)
  n = 0.766
FEATURE [App::DocumentObjectGroupPython] Na_element018  label="Na_element : 0.101"  # scripted group (container) (typed FeaturePython)
  n = 0.002
FEATURE [App::DocumentObjectGroupPython] P_element010  label="P_element : 0.108"  # scripted group (container) (typed FeaturePython)
  n = 0.001
FEATURE [App::DocumentObjectGroupPython] S_element021  label="S_element : 0.022"  # scripted group (container) (typed FeaturePython)
  n = 0.002
FEATURE [App::DocumentObjectGroupPython] Cl_element024  label="Cl_element : 0.002"  # scripted group (container) (typed FeaturePython)
  n = 0.002
FEATURE [App::DocumentObjectGroupPython] K_element011  label="K_element : 0.017"  # scripted group (container) (typed FeaturePython)
  n = 0.002
FEATURE [App::DocumentObjectGroupPython] G4_TESTIS_ICRP  # scripted group (container) (typed FeaturePython)
  Dunit = g/cm3
  Dvalue = 1.04
  Group = -> [H_element099,C_element108,N_element041,O_element093,Na_element018,P_element010,S_element021,Cl_element024,K_element011]
  conduct = 2
  density = 1
  expand = 3
  formula = G4_TESTIS_ICRP
  name = G4_TESTIS_ICRP
  specific = 4
FEATURE [App::DocumentObjectGroupPython] C_element109  label="C_element : 060"  # scripted group (container) (typed FeaturePython)
  n = 2
  ref = C_element
FEATURE [App::DocumentObjectGroupPython] Cl_element025  label="Cl_element : 012"  # scripted group (container) (typed FeaturePython)
  n = 4
  ref = Cl_element
FEATURE [App::DocumentObjectGroupPython] G4_TETRACHLOROETHYLENE  # scripted group (container) (typed FeaturePython)
  Dunit = g/cm3
  Dvalue = 1.625
  Group = -> [C_element109,Cl_element025]
  conduct = 2
  density = 1
  expand = 3
  formula = G4_TETRACHLOROETHYLENE
  name = G4_TETRACHLOROETHYLENE
  specific = 4
FEATURE [App::DocumentObjectGroupPython] Tl_element001  label="Tl_element : 1"  # scripted group (container) (typed FeaturePython)
  n = 1
  ref = Tl_element
FEATURE [App::DocumentObjectGroupPython] Cl_element026  label="Cl_element : 013"  # scripted group (container) (typed FeaturePython)
  n = 1
  ref = Cl_element
FEATURE [App::DocumentObjectGroupPython] G4_THALLIUM_CHLORIDE  # scripted group (container) (typed FeaturePython)
  Dunit = g/cm3
  Dvalue = 7.004
  Group = -> [Tl_element001,Cl_element026]
  conduct = 2
  density = 1
  expand = 3
  formula = G4_THALLIUM_CHLORIDE
  name = G4_THALLIUM_CHLORIDE
  specific = 4
FEATURE [App::DocumentObjectGroupPython] H_element100  label="H_element : 0.147"  # scripted group (container) (typed FeaturePython)
  n = 0.105
FEATURE [App::DocumentObjectGroupPython] C_element110  label="C_element : 0.256"  # scripted group (container) (typed FeaturePython)
  n = 0.256
FEATURE [App::DocumentObjectGroupPython] N_element042  label="N_element : 0.760"  # scripted group (container) (typed FeaturePython)
  n = 0.027
FEATURE [App::DocumentObjectGroupPython] O_element094  label="O_element : 0.602"  # scripted group (container) (typed FeaturePython)
  n = 0.602
FEATURE [App::DocumentObjectGroupPython] Na_element019  label="Na_element : 0.102"  # scripted group (container) (typed FeaturePython)
  n = 0.001
FEATURE [App::DocumentObjectGroupPython] P_element011  label="P_element : 0.109"  # scripted group (container) (typed FeaturePython)
  n = 0.002
FEATURE [App::DocumentObjectGroupPython] S_element022  label="S_element : 0.023"  # scripted group (container) (typed FeaturePython)
  n = 0.003
FEATURE [App::DocumentObjectGroupPython] Cl_element027  label="Cl_element : 0.591"  # scripted group (container) (typed FeaturePython)
  n = 0.002
FEATURE [App::DocumentObjectGroupPython] K_element012  label="K_element : 0.018"  # scripted group (container) (typed FeaturePython)
  n = 0.002
FEATURE [App::DocumentObjectGroupPython] G4_TISSUE_SOFT_ICRP  # scripted group (container) (typed FeaturePython)
  Dunit = g/cm3
  Dvalue = 1.03
  Group = -> [H_element100,C_element110,N_element042,O_element094,Na_element019,P_element011,S_element022,Cl_element027,K_element012]
  conduct = 2
  density = 1
  expand = 3
  formula = G4_TISSUE_SOFT_ICRP
  name = G4_TISSUE_SOFT_ICRP
  specific = 4
FEATURE [App::DocumentObjectGroupPython] H_element101  label="H_element : 0.148"  # scripted group (container) (typed FeaturePython)
  n = 0.101
FEATURE [App::DocumentObjectGroupPython] C_element111  label="C_element : 0.111"  # scripted group (container) (typed FeaturePython)
  n = 0.111
FEATURE [App::DocumentObjectGroupPython] N_element043  label="N_element : 0.026"  # scripted group (container) (typed FeaturePython)
  n = 0.026
FEATURE [App::DocumentObjectGroupPython] O_element095  label="O_element : 0.762"  # scripted group (container) (typed FeaturePython)
  n = 0.762
FEATURE [App::DocumentObjectGroupPython] G4_TISSUE_SOFT_ICRU_4  label="G4_TISSUE_SOFT_ICRU-4"  # scripted group (container) (typed FeaturePython)
  Dunit = g/cm3
  Dvalue = 1
  Group = -> [H_element101,C_element111,N_element043,O_element095]
  conduct = 2
  density = 1
  expand = 3
  formula = G4_TISSUE_SOFT_ICRU-4
  name = G4_TISSUE_SOFT_ICRU-4
  specific = 4
FEATURE [App::DocumentObjectGroupPython] H_element102  label="H_element : 0.149"  # scripted group (container) (typed FeaturePython)
  n = 0.101869
FEATURE [App::DocumentObjectGroupPython] C_element112  label="C_element : 0.456"  # scripted group (container) (typed FeaturePython)
  n = 0.456179
FEATURE [App::DocumentObjectGroupPython] N_element044  label="N_element : 0.761"  # scripted group (container) (typed FeaturePython)
  n = 0.035172
FEATURE [App::DocumentObjectGroupPython] O_element096  label="O_element : 0.407"  # scripted group (container) (typed FeaturePython)
  n = 0.40678
FEATURE [App::DocumentObjectGroupPython] G4_TISSUE_METHANE  label="G4_TISSUE-METHANE"  # scripted group (container) (typed FeaturePython)
  Dunit = g/cm3
  Dvalue = 0.00106409
  Group = -> [H_element102,C_element112,N_element044,O_element096]
  conduct = 2
  density = 1
  expand = 3
  formula = G4_TISSUE-METHANE
  name = G4_TISSUE-METHANE
  specific = 4
FEATURE [App::DocumentObjectGroupPython] H_element103  label="H_element : 0.103"  # scripted group (container) (typed FeaturePython)
  n = 0.102672
FEATURE [App::DocumentObjectGroupPython] C_element113  label="C_element : 0.569"  # scripted group (container) (typed FeaturePython)
  n = 0.56894
FEATURE [App::DocumentObjectGroupPython] N_element045  label="N_element : 0.762"  # scripted group (container) (typed FeaturePython)
  n = 0.035022
FEATURE [App::DocumentObjectGroupPython] O_element097  label="O_element : 0.293"  # scripted group (container) (typed FeaturePython)
  n = 0.293366
FEATURE [App::DocumentObjectGroupPython] G4_TISSUE_PROPANE  label="G4_TISSUE-PROPANE"  # scripted group (container) (typed FeaturePython)
  Dunit = g/cm3
  Dvalue = 0.00182628
  Group = -> [H_element103,C_element113,N_element045,O_element097]
  conduct = 2
  density = 1
  expand = 3
  formula = G4_TISSUE-PROPANE
  name = G4_TISSUE-PROPANE
  specific = 4
FEATURE [App::DocumentObjectGroupPython] Ti_element003  label="Ti_element : 1"  # scripted group (container) (typed FeaturePython)
  n = 1
  ref = Ti_element
FEATURE [App::DocumentObjectGroupPython] O_element098  label="O_element : 052"  # scripted group (container) (typed FeaturePython)
  n = 2
  ref = O_element
FEATURE [App::DocumentObjectGroupPython] G4_TITANIUM_DIOXIDE  # scripted group (container) (typed FeaturePython)
  Dunit = g/cm3
  Dvalue = 4.26
  Group = -> [Ti_element003,O_element098]
  conduct = 2
  density = 1
  expand = 3
  formula = G4_TITANIUM_DIOXIDE
  name = G4_TITANIUM_DIOXIDE
  specific = 4
FEATURE [App::DocumentObjectGroupPython] C_element114  label="C_element : 061"  # scripted group (container) (typed FeaturePython)
  n = 7
  ref = C_element
FEATURE [App::DocumentObjectGroupPython] H_element104  label="H_element : 055"  # scripted group (container) (typed FeaturePython)
  n = 8
  ref = H_element
FEATURE [App::DocumentObjectGroupPython] G4_TOLUENE  # scripted group (container) (typed FeaturePython)
  Dunit = g/cm3
  Dvalue = 0.8669
  Group = -> [C_element114,H_element104]
  conduct = 2
  density = 1
  expand = 3
  formula = G4_TOLUENE
  name = G4_TOLUENE
  specific = 4
FEATURE [App::DocumentObjectGroupPython] C_element115  label="C_element : 062"  # scripted group (container) (typed FeaturePython)
  n = 2
  ref = C_element
FEATURE [App::DocumentObjectGroupPython] H_element105  label="H_element : 056"  # scripted group (container) (typed FeaturePython)
  n = 1
  ref = H_element
FEATURE [App::DocumentObjectGroupPython] Cl_element028  label="Cl_element : 014"  # scripted group (container) (typed FeaturePython)
  n = 3
  ref = Cl_element
FEATURE [App::DocumentObjectGroupPython] G4_TRICHLOROETHYLENE  # scripted group (container) (typed FeaturePython)
  Dunit = g/cm3
  Dvalue = 1.46
  Group = -> [C_element115,H_element105,Cl_element028]
  conduct = 2
  density = 1
  expand = 3
  formula = G4_TRICHLOROETHYLENE
  name = G4_TRICHLOROETHYLENE
  specific = 4
FEATURE [App::DocumentObjectGroupPython] C_element116  label="C_element : 063"  # scripted group (container) (typed FeaturePython)
  n = 6
  ref = C_element
FEATURE [App::DocumentObjectGroupPython] H_element106  label="H_element : 15"  # scripted group (container) (typed FeaturePython)
  n = 15
  ref = H_element
FEATURE [App::DocumentObjectGroupPython] O_element099  label="O_element : 053"  # scripted group (container) (typed FeaturePython)
  n = 4
  ref = O_element
FEATURE [App::DocumentObjectGroupPython] P_element012  label="P_element : 1"  # scripted group (container) (typed FeaturePython)
  n = 1
  ref = P_element
FEATURE [App::DocumentObjectGroupPython] G4_TRIETHYL_PHOSPHATE  # scripted group (container) (typed FeaturePython)
  Dunit = g/cm3
  Dvalue = 1.07
  Group = -> [C_element116,H_element106,O_element099,P_element012]
  conduct = 2
  density = 1
  expand = 3
  formula = G4_TRIETHYL_PHOSPHATE
  name = G4_TRIETHYL_PHOSPHATE
  specific = 4
FEATURE [App::DocumentObjectGroupPython] W_element003  label="W_element : 003"  # scripted group (container) (typed FeaturePython)
  n = 1
  ref = W_element
FEATURE [App::DocumentObjectGroupPython] F_element017  label="F_element : 6"  # scripted group (container) (typed FeaturePython)
  n = 6
  ref = F_element
FEATURE [App::DocumentObjectGroupPython] G4_TUNGSTEN_HEXAFLUORIDE  # scripted group (container) (typed FeaturePython)
  Dunit = g/cm3
  Dvalue = 2.4
  Group = -> [W_element003,F_element017]
  conduct = 2
  density = 1
  expand = 3
  formula = G4_TUNGSTEN_HEXAFLUORIDE
  name = G4_TUNGSTEN_HEXAFLUORIDE
  specific = 4
FEATURE [App::DocumentObjectGroupPython] U_element001  label="U_element : 1"  # scripted group (container) (typed FeaturePython)
  n = 1
  ref = U_element
FEATURE [App::DocumentObjectGroupPython] C_element117  label="C_element : 064"  # scripted group (container) (typed FeaturePython)
  n = 2
  ref = C_element
FEATURE [App::DocumentObjectGroupPython] G4_URANIUM_DICARBIDE  # scripted group (container) (typed FeaturePython)
  Dunit = g/cm3
  Dvalue = 11.28
  Group = -> [U_element001,C_element117]
  conduct = 2
  density = 1
  expand = 3
  formula = G4_URANIUM_DICARBIDE
  name = G4_URANIUM_DICARBIDE
  specific = 4
FEATURE [App::DocumentObjectGroupPython] U_element002  label="U_element : 002"  # scripted group (container) (typed FeaturePython)
  n = 1
  ref = U_element
FEATURE [App::DocumentObjectGroupPython] C_element118  label="C_element : 065"  # scripted group (container) (typed FeaturePython)
  n = 1
  ref = C_element
FEATURE [App::DocumentObjectGroupPython] G4_URANIUM_MONOCARBIDE  # scripted group (container) (typed FeaturePython)
  Dunit = g/cm3
  Dvalue = 13.63
  Group = -> [U_element002,C_element118]
  conduct = 2
  density = 1
  expand = 3
  formula = G4_URANIUM_MONOCARBIDE
  name = G4_URANIUM_MONOCARBIDE
  specific = 4
FEATURE [App::DocumentObjectGroupPython] U_element003  label="U_element : 003"  # scripted group (container) (typed FeaturePython)
  n = 1
  ref = U_element
FEATURE [App::DocumentObjectGroupPython] O_element100  label="O_element : 054"  # scripted group (container) (typed FeaturePython)
  n = 2
  ref = O_element
FEATURE [App::DocumentObjectGroupPython] G4_URANIUM_OXIDE  # scripted group (container) (typed FeaturePython)
  Dunit = g/cm3
  Dvalue = 10.96
  Group = -> [U_element003,O_element100]
  conduct = 2
  density = 1
  expand = 3
  formula = G4_URANIUM_OXIDE
  name = G4_URANIUM_OXIDE
  specific = 4
FEATURE [App::DocumentObjectGroupPython] C_element119  label="C_element : 066"  # scripted group (container) (typed FeaturePython)
  n = 1
  ref = C_element
FEATURE [App::DocumentObjectGroupPython] H_element107  label="H_element : 057"  # scripted group (container) (typed FeaturePython)
  n = 4
  ref = H_element
FEATURE [App::DocumentObjectGroupPython] N_element046  label="N_element : 019"  # scripted group (container) (typed FeaturePython)
  n = 2
  ref = N_element
FEATURE [App::DocumentObjectGroupPython] O_element101  label="O_element : 055"  # scripted group (container) (typed FeaturePython)
  n = 1
  ref = O_element
FEATURE [App::DocumentObjectGroupPython] G4_UREA  # scripted group (container) (typed FeaturePython)
  Dunit = g/cm3
  Dvalue = 1.323
  Group = -> [C_element119,H_element107,N_element046,O_element101]
  conduct = 2
  density = 1
  expand = 3
  formula = G4_UREA
  name = G4_UREA
  specific = 4
FEATURE [App::DocumentObjectGroupPython] C_element120  label="C_element : 067"  # scripted group (container) (typed FeaturePython)
  n = 5
  ref = C_element
FEATURE [App::DocumentObjectGroupPython] H_element108  label="H_element : 058"  # scripted group (container) (typed FeaturePython)
  n = 11
  ref = H_element
FEATURE [App::DocumentObjectGroupPython] N_element047  label="N_element : 020"  # scripted group (container) (typed FeaturePython)
  n = 1
  ref = N_element
FEATURE [App::DocumentObjectGroupPython] O_element102  label="O_element : 056"  # scripted group (container) (typed FeaturePython)
  n = 2
  ref = O_element
FEATURE [App::DocumentObjectGroupPython] G4_VALINE  # scripted group (container) (typed FeaturePython)
  Dunit = g/cm3
  Dvalue = 1.23
  Group = -> [C_element120,H_element108,N_element047,O_element102]
  conduct = 2
  density = 1
  expand = 3
  formula = G4_VALINE
  name = G4_VALINE
  specific = 4
FEATURE [App::DocumentObjectGroupPython] H_element109  label="H_element : 0.009"  # scripted group (container) (typed FeaturePython)
  n = 0.009417
FEATURE [App::DocumentObjectGroupPython] C_element121  label="C_element : 0.281"  # scripted group (container) (typed FeaturePython)
  n = 0.280555
FEATURE [App::DocumentObjectGroupPython] F_element018  label="F_element : 0.710"  # scripted group (container) (typed FeaturePython)
  n = 0.710028
FEATURE [App::DocumentObjectGroupPython] G4_VITON  # scripted group (container) (typed FeaturePython)
  Dunit = g/cm3
  Dvalue = 1.8
  Group = -> [H_element109,C_element121,F_element018]
  conduct = 2
  density = 1
  expand = 3
  formula = G4_VITON
  name = G4_VITON
  specific = 4
FEATURE [App::DocumentObjectGroupPython] H_element110  label="H_element : 059"  # scripted group (container) (typed FeaturePython)
  n = 2
  ref = H_element
FEATURE [App::DocumentObjectGroupPython] O_element103  label="O_element : 057"  # scripted group (container) (typed FeaturePython)
  n = 1
  ref = O_element
FEATURE [App::DocumentObjectGroupPython] G4_WATER  # scripted group (container) (typed FeaturePython)
  Dunit = g/cm3
  Dvalue = 1
  Group = -> [H_element110,O_element103]
  conduct = 2
  density = 1
  expand = 3
  formula = G4_WATER
  name = G4_WATER
  specific = 4
FEATURE [App::DocumentObjectGroupPython] H_element111  label="H_element : 060"  # scripted group (container) (typed FeaturePython)
  n = 2
  ref = H_element
FEATURE [App::DocumentObjectGroupPython] O_element104  label="O_element : 058"  # scripted group (container) (typed FeaturePython)
  n = 1
  ref = O_element
FEATURE [App::DocumentObjectGroupPython] G4_WATER_VAPOR  # scripted group (container) (typed FeaturePython)
  Dunit = g/cm3
  Dvalue = 0.000756182
  Group = -> [H_element111,O_element104]
  conduct = 2
  density = 1
  expand = 3
  formula = G4_WATER_VAPOR
  name = G4_WATER_VAPOR
  specific = 4
FEATURE [App::DocumentObjectGroupPython] C_element122  label="C_element : 068"  # scripted group (container) (typed FeaturePython)
  n = 8
  ref = C_element
FEATURE [App::DocumentObjectGroupPython] H_element112  label="H_element : 061"  # scripted group (container) (typed FeaturePython)
  n = 10
  ref = H_element
FEATURE [App::DocumentObjectGroupPython] G4_XYLENE  # scripted group (container) (typed FeaturePython)
  Dunit = g/cm3
  Dvalue = 0.87
  Group = -> [C_element122,H_element112]
  conduct = 2
  density = 1
  expand = 3
  formula = G4_XYLENE
  name = G4_XYLENE
  specific = 4
FEATURE [App::DocumentObjectGroupPython] C_element123  label="C_element : 069"  # scripted group (container) (typed FeaturePython)
  n = 1
  ref = C_element
FEATURE [App::DocumentObjectGroupPython] G4_GRAPHITE  # scripted group (container) (typed FeaturePython)
  Dunit = g/cm3
  Dvalue = 2.21
  Group = -> [C_element123]
  conduct = 2
  density = 1
  expand = 3
  formula = G4_GRAPHITE
  name = G4_GRAPHITE
  specific = 4
FEATURE [App::DocumentObjectGroupPython] NIST  # scripted group (container) (typed FeaturePython)
  Group = -> [G4_A_150_TISSUE,G4_ACETONE,G4_ACETYLENE,G4_ADENINE,G4_ADIPOSE_TISSUE_ICRP,G4_AIR,G4_ALANINE,G4_ALUMINUM_OXIDE,G4_AMBER,G4_AMMONIA,G4_ANILINE,G4_ANTHRACENE,G4_B_100_BONE,G4_BAKELITE,G4_BARIUM_FLUORIDE,G4_BARIUM_SULFATE,G4_BENZENE,G4_BERYLLIUM_OXIDE,G4_BGO,G4_BLOOD_ICRP,G4_BONE_COMPACT_ICRU,G4_BONE_CORTICAL_ICRP,G4_BORON_CARBIDE,G4_BORON_OXIDE,G4_BRAIN_ICRP,G4_BUTANE,G4_N_BUTYL_ALCOHOL,G4_C_552,+152 more]
FEATURE [App::DocumentObjectGroupPython] H_element113  label="H_element : 062"  # scripted group (container) (typed FeaturePython)
  n = 1
  ref = H_element
FEATURE [App::DocumentObjectGroupPython] G4_H  # scripted group (container) (typed FeaturePython)
  Dunit = g/cm3
  Dvalue = 8.3748e-05
  Group = -> [H_element113]
  conduct = 2
  density = 1
  expand = 3
  formula = H
  name = G4_H
  specific = 4
FEATURE [App::DocumentObjectGroupPython] He_element001  label="He_element : 1"  # scripted group (container) (typed FeaturePython)
  n = 1
  ref = He_element
FEATURE [App::DocumentObjectGroupPython] G4_He  # scripted group (container) (typed FeaturePython)
  Dunit = g/cm3
  Dvalue = 0.000166322
  Group = -> [He_element001]
  conduct = 2
  density = 1
  expand = 3
  formula = He
  name = G4_He
  specific = 4
FEATURE [App::DocumentObjectGroupPython] Li_element008  label="Li_element : 008"  # scripted group (container) (typed FeaturePython)
  n = 1
  ref = Li_element
FEATURE [App::DocumentObjectGroupPython] G4_Li  # scripted group (container) (typed FeaturePython)
  Dunit = g/cm3
  Dvalue = 0.534
  Group = -> [Li_element008]
  conduct = 2
  density = 1
  expand = 3
  formula = Li
  name = G4_Li
  specific = 4
FEATURE [App::DocumentObjectGroupPython] Be_element002  label="Be_element : 002"  # scripted group (container) (typed FeaturePython)
  n = 1
  ref = Be_element
FEATURE [App::DocumentObjectGroupPython] G4_Be  # scripted group (container) (typed FeaturePython)
  Dunit = g/cm3
  Dvalue = 1.848
  Group = -> [Be_element002]
  conduct = 2
  density = 1
  expand = 3
  formula = Be
  name = G4_Be
  specific = 4
FEATURE [App::DocumentObjectGroupPython] B_element007  label="B_element : 007"  # scripted group (container) (typed FeaturePython)
  n = 1
  ref = B_element
FEATURE [App::DocumentObjectGroupPython] G4_B  # scripted group (container) (typed FeaturePython)
  Dunit = g/cm3
  Dvalue = 2.37
  Group = -> [B_element007]
  conduct = 2
  density = 1
  expand = 3
  formula = B
  name = G4_B
  specific = 4
FEATURE [App::DocumentObjectGroupPython] C_element124  label="C_element : 070"  # scripted group (container) (typed FeaturePython)
  n = 1
  ref = C_element
FEATURE [App::DocumentObjectGroupPython] G4_C  # scripted group (container) (typed FeaturePython)
  Dunit = g/cm3
  Dvalue = 2
  Group = -> [C_element124]
  conduct = 2
  density = 1
  expand = 3
  formula = C
  name = G4_C
  specific = 4
FEATURE [App::DocumentObjectGroupPython] N_element048  label="N_element : 021"  # scripted group (container) (typed FeaturePython)
  n = 1
  ref = N_element
FEATURE [App::DocumentObjectGroupPython] G4_N  # scripted group (container) (typed FeaturePython)
  Dunit = g/cm3
  Dvalue = 0.0011652
  Group = -> [N_element048]
  conduct = 2
  density = 1
  expand = 3
  formula = N
  name = G4_N
  specific = 4
FEATURE [App::DocumentObjectGroupPython] O_element105  label="O_element : 059"  # scripted group (container) (typed FeaturePython)
  n = 1
  ref = O_element
FEATURE [App::DocumentObjectGroupPython] G4_O  # scripted group (container) (typed FeaturePython)
  Dunit = g/cm3
  Dvalue = 0.00133151
  Group = -> [O_element105]
  conduct = 2
  density = 1
  expand = 3
  formula = O
  name = G4_O
  specific = 4
FEATURE [App::DocumentObjectGroupPython] F_element019  label="F_element : 008"  # scripted group (container) (typed FeaturePython)
  n = 1
  ref = F_element
FEATURE [App::DocumentObjectGroupPython] G4_F  # scripted group (container) (typed FeaturePython)
  Dunit = g/cm3
  Dvalue = 0.00158029
  Group = -> [F_element019]
  conduct = 2
  density = 1
  expand = 3
  formula = F
  name = G4_F
  specific = 4
FEATURE [App::DocumentObjectGroupPython] Ne_element001  label="Ne_element : 1"  # scripted group (container) (typed FeaturePython)
  n = 1
  ref = Ne_element
FEATURE [App::DocumentObjectGroupPython] G4_Ne  # scripted group (container) (typed FeaturePython)
  Dunit = g/cm3
  Dvalue = 0.000838505
  Group = -> [Ne_element001]
  conduct = 2
  density = 1
  expand = 3
  formula = Ne
  name = G4_Ne
  specific = 4
FEATURE [App::DocumentObjectGroupPython] Na_element020  label="Na_element : 005"  # scripted group (container) (typed FeaturePython)
  n = 1
  ref = Na_element
FEATURE [App::DocumentObjectGroupPython] G4_Na  # scripted group (container) (typed FeaturePython)
  Dunit = g/cm3
  Dvalue = 0.971
  Group = -> [Na_element020]
  conduct = 2
  density = 1
  expand = 3
  formula = Na
  name = G4_Na
  specific = 4
FEATURE [App::DocumentObjectGroupPython] Mg_element011  label="Mg_element : 005"  # scripted group (container) (typed FeaturePython)
  n = 1
  ref = Mg_element
FEATURE [App::DocumentObjectGroupPython] G4_Mg  # scripted group (container) (typed FeaturePython)
  Dunit = g/cm3
  Dvalue = 1.74
  Group = -> [Mg_element011]
  conduct = 2
  density = 1
  expand = 3
  formula = Mg
  name = G4_Mg
  specific = 4
FEATURE [App::DocumentObjectGroupPython] Al_element004  label="Al_element : 1"  # scripted group (container) (typed FeaturePython)
  n = 1
  ref = Al_element
FEATURE [App::DocumentObjectGroupPython] G4_Al  # scripted group (container) (typed FeaturePython)
  Dunit = g/cm3
  Dvalue = 2.699
  Group = -> [Al_element004]
  conduct = 2
  density = 1
  expand = 3
  formula = Al
  name = G4_Al
  specific = 4
FEATURE [App::DocumentObjectGroupPython] Si_element007  label="Si_element : 002"  # scripted group (container) (typed FeaturePython)
  n = 1
  ref = Si_element
FEATURE [App::DocumentObjectGroupPython] G4_Si  # scripted group (container) (typed FeaturePython)
  Dunit = g/cm3
  Dvalue = 2.33
  Group = -> [Si_element007]
  conduct = 2
  density = 1
  expand = 3
  formula = Si
  name = G4_Si
  specific = 4
FEATURE [App::DocumentObjectGroupPython] P_element013  label="P_element : 002"  # scripted group (container) (typed FeaturePython)
  n = 1
  ref = P_element
FEATURE [App::DocumentObjectGroupPython] G4_P  # scripted group (container) (typed FeaturePython)
  Dunit = g/cm3
  Dvalue = 2.2
  Group = -> [P_element013]
  conduct = 2
  density = 1
  expand = 3
  formula = P
  name = G4_P
  specific = 4
FEATURE [App::DocumentObjectGroupPython] S_element023  label="S_element : 007"  # scripted group (container) (typed FeaturePython)
  n = 1
  ref = S_element
FEATURE [App::DocumentObjectGroupPython] G4_S  # scripted group (container) (typed FeaturePython)
  Dunit = g/cm3
  Dvalue = 2
  Group = -> [S_element023]
  conduct = 2
  density = 1
  expand = 3
  formula = S
  name = G4_S
  specific = 4
FEATURE [App::DocumentObjectGroupPython] Cl_element029  label="Cl_element : 015"  # scripted group (container) (typed FeaturePython)
  n = 1
  ref = Cl_element
FEATURE [App::DocumentObjectGroupPython] G4_Cl  # scripted group (container) (typed FeaturePython)
  Dunit = g/cm3
  Dvalue = 0.00299473
  Group = -> [Cl_element029]
  conduct = 2
  density = 1
  expand = 3
  formula = Cl
  name = G4_Cl
  specific = 4
FEATURE [App::DocumentObjectGroupPython] Ar_element002  label="Ar_element : 1"  # scripted group (container) (typed FeaturePython)
  n = 1
  ref = Ar_element
FEATURE [App::DocumentObjectGroupPython] G4_Ar  # scripted group (container) (typed FeaturePython)
  Dunit = g/cm3
  Dvalue = 0.00166201
  Group = -> [Ar_element002]
  conduct = 2
  density = 1
  expand = 3
  formula = Ar
  name = G4_Ar
  specific = 4
FEATURE [App::DocumentObjectGroupPython] K_element013  label="K_element : 003"  # scripted group (container) (typed FeaturePython)
  n = 1
  ref = K_element
FEATURE [App::DocumentObjectGroupPython] G4_K  # scripted group (container) (typed FeaturePython)
  Dunit = g/cm3
  Dvalue = 0.862
  Group = -> [K_element013]
  conduct = 2
  density = 1
  expand = 3
  formula = K
  name = G4_K
  specific = 4
FEATURE [App::DocumentObjectGroupPython] Ca_element014  label="Ca_element : 007"  # scripted group (container) (typed FeaturePython)
  n = 1
  ref = Ca_element
FEATURE [App::DocumentObjectGroupPython] G4_Ca  # scripted group (container) (typed FeaturePython)
  Dunit = g/cm3
  Dvalue = 1.55
  Group = -> [Ca_element014]
  conduct = 2
  density = 1
  expand = 3
  formula = Ca
  name = G4_Ca
  specific = 4
FEATURE [App::DocumentObjectGroupPython] Sc_element001  label="Sc_element : 1"  # scripted group (container) (typed FeaturePython)
  n = 1
  ref = Sc_element
FEATURE [App::DocumentObjectGroupPython] G4_Sc  # scripted group (container) (typed FeaturePython)
  Dunit = g/cm3
  Dvalue = 2.989
  Group = -> [Sc_element001]
  conduct = 2
  density = 1
  expand = 3
  formula = Sc
  name = G4_Sc
  specific = 4
FEATURE [App::DocumentObjectGroupPython] Ti_element004  label="Ti_element : 002"  # scripted group (container) (typed FeaturePython)
  n = 1
  ref = Ti_element
FEATURE [App::DocumentObjectGroupPython] G4_Ti  # scripted group (container) (typed FeaturePython)
  Dunit = g/cm3
  Dvalue = 4.54
  Group = -> [Ti_element004]
  conduct = 2
  density = 1
  expand = 3
  formula = Ti
  name = G4_Ti
  specific = 4
FEATURE [App::DocumentObjectGroupPython] V_element001  label="V_element : 1"  # scripted group (container) (typed FeaturePython)
  n = 1
  ref = V_element
FEATURE [App::DocumentObjectGroupPython] G4_V  # scripted group (container) (typed FeaturePython)
  Dunit = g/cm3
  Dvalue = 6.11
  Group = -> [V_element001]
  conduct = 2
  density = 1
  expand = 3
  formula = V
  name = G4_V
  specific = 4
FEATURE [App::DocumentObjectGroupPython] Cr_element001  label="Cr_element : 1"  # scripted group (container) (typed FeaturePython)
  n = 1
  ref = Cr_element
FEATURE [App::DocumentObjectGroupPython] G4_Cr  # scripted group (container) (typed FeaturePython)
  Dunit = g/cm3
  Dvalue = 7.18
  Group = -> [Cr_element001]
  conduct = 2
  density = 1
  expand = 3
  formula = Cr
  name = G4_Cr
  specific = 4
FEATURE [App::DocumentObjectGroupPython] Mn_element001  label="Mn_element : 1"  # scripted group (container) (typed FeaturePython)
  n = 1
  ref = Mn_element
FEATURE [App::DocumentObjectGroupPython] G4_Mn  # scripted group (container) (typed FeaturePython)
  Dunit = g/cm3
  Dvalue = 7.44
  Group = -> [Mn_element001]
  conduct = 2
  density = 1
  expand = 3
  formula = Mn
  name = G4_Mn
  specific = 4
FEATURE [App::DocumentObjectGroupPython] Fe_element007  label="Fe_element : 004"  # scripted group (container) (typed FeaturePython)
  n = 1
  ref = Fe_element
FEATURE [App::DocumentObjectGroupPython] G4_Fe  # scripted group (container) (typed FeaturePython)
  Dunit = g/cm3
  Dvalue = 7.874
  Group = -> [Fe_element007]
  conduct = 2
  density = 1
  expand = 3
  formula = Fe
  name = G4_Fe
  specific = 4
FEATURE [App::DocumentObjectGroupPython] Co_element001  label="Co_element : 1"  # scripted group (container) (typed FeaturePython)
  n = 1
  ref = Co_element
FEATURE [App::DocumentObjectGroupPython] G4_Co  # scripted group (container) (typed FeaturePython)
  Dunit = g/cm3
  Dvalue = 8.9
  Group = -> [Co_element001]
  conduct = 2
  density = 1
  expand = 3
  formula = Co
  name = G4_Co
  specific = 4
FEATURE [App::DocumentObjectGroupPython] Ni_element001  label="Ni_element : 1"  # scripted group (container) (typed FeaturePython)
  n = 1
  ref = Ni_element
FEATURE [App::DocumentObjectGroupPython] G4_Ni  # scripted group (container) (typed FeaturePython)
  Dunit = g/cm3
  Dvalue = 8.902
  Group = -> [Ni_element001]
  conduct = 2
  density = 1
  expand = 3
  formula = Ni
  name = G4_Ni
  specific = 4
FEATURE [App::DocumentObjectGroupPython] Cu_element001  label="Cu_element : 1"  # scripted group (container) (typed FeaturePython)
  n = 1
  ref = Cu_element
FEATURE [App::DocumentObjectGroupPython] G4_Cu  # scripted group (container) (typed FeaturePython)
  Dunit = g/cm3
  Dvalue = 8.96
  Group = -> [Cu_element001]
  conduct = 2
  density = 1
  expand = 3
  formula = Cu
  name = G4_Cu
  specific = 4
FEATURE [App::DocumentObjectGroupPython] Zn_element001  label="Zn_element : 1"  # scripted group (container) (typed FeaturePython)
  n = 1
  ref = Zn_element
FEATURE [App::DocumentObjectGroupPython] G4_Zn  # scripted group (container) (typed FeaturePython)
  Dunit = g/cm3
  Dvalue = 7.133
  Group = -> [Zn_element001]
  conduct = 2
  density = 1
  expand = 3
  formula = Zn
  name = G4_Zn
  specific = 4
FEATURE [App::DocumentObjectGroupPython] Ga_element002  label="Ga_element : 002"  # scripted group (container) (typed FeaturePython)
  n = 1
  ref = Ga_element
FEATURE [App::DocumentObjectGroupPython] G4_Ga  # scripted group (container) (typed FeaturePython)
  Dunit = g/cm3
  Dvalue = 5.904
  Group = -> [Ga_element002]
  conduct = 2
  density = 1
  expand = 3
  formula = Ga
  name = G4_Ga
  specific = 4
FEATURE [App::DocumentObjectGroupPython] Ge_element002  label="Ge_element : 1"  # scripted group (container) (typed FeaturePython)
  n = 1
  ref = Ge_element
FEATURE [App::DocumentObjectGroupPython] G4_Ge  # scripted group (container) (typed FeaturePython)
  Dunit = g/cm3
  Dvalue = 5.323
  Group = -> [Ge_element002]
  conduct = 2
  density = 1
  expand = 3
  formula = Ge
  name = G4_Ge
  specific = 4
FEATURE [App::DocumentObjectGroupPython] As_element003  label="As_element : 002"  # scripted group (container) (typed FeaturePython)
  n = 1
  ref = As_element
FEATURE [App::DocumentObjectGroupPython] G4_As  # scripted group (container) (typed FeaturePython)
  Dunit = g/cm3
  Dvalue = 5.73
  Group = -> [As_element003]
  conduct = 2
  density = 1
  expand = 3
  formula = As
  name = G4_As
  specific = 4
FEATURE [App::DocumentObjectGroupPython] Se_element001  label="Se_element : 1"  # scripted group (container) (typed FeaturePython)
  n = 1
  ref = Se_element
FEATURE [App::DocumentObjectGroupPython] G4_Se  # scripted group (container) (typed FeaturePython)
  Dunit = g/cm3
  Dvalue = 4.5
  Group = -> [Se_element001]
  conduct = 2
  density = 1
  expand = 3
  formula = Se
  name = G4_Se
  specific = 4
FEATURE [App::DocumentObjectGroupPython] Br_element007  label="Br_element : 004"  # scripted group (container) (typed FeaturePython)
  n = 1
  ref = Br_element
FEATURE [App::DocumentObjectGroupPython] G4_Br  # scripted group (container) (typed FeaturePython)
  Dunit = g/cm3
  Dvalue = 0.0070721
  Group = -> [Br_element007]
  conduct = 2
  density = 1
  expand = 3
  formula = Br
  name = G4_Br
  specific = 4
FEATURE [App::DocumentObjectGroupPython] Kr_element001  label="Kr_element : 1"  # scripted group (container) (typed FeaturePython)
  n = 1
  ref = Kr_element
FEATURE [App::DocumentObjectGroupPython] G4_Kr  # scripted group (container) (typed FeaturePython)
  Dunit = g/cm3
  Dvalue = 0.00347832
  Group = -> [Kr_element001]
  conduct = 2
  density = 1
  expand = 3
  formula = Kr
  name = G4_Kr
  specific = 4
FEATURE [App::DocumentObjectGroupPython] Rb_element001  label="Rb_element : 1"  # scripted group (container) (typed FeaturePython)
  n = 1
  ref = Rb_element
FEATURE [App::DocumentObjectGroupPython] G4_Rb  # scripted group (container) (typed FeaturePython)
  Dunit = g/cm3
  Dvalue = 1.532
  Group = -> [Rb_element001]
  conduct = 2
  density = 1
  expand = 3
  formula = Rb
  name = G4_Rb
  specific = 4
FEATURE [App::DocumentObjectGroupPython] Sr_element001  label="Sr_element : 1"  # scripted group (container) (typed FeaturePython)
  n = 1
  ref = Sr_element
FEATURE [App::DocumentObjectGroupPython] G4_Sr  # scripted group (container) (typed FeaturePython)
  Dunit = g/cm3
  Dvalue = 2.54
  Group = -> [Sr_element001]
  conduct = 2
  density = 1
  expand = 3
  formula = Sr
  name = G4_Sr
  specific = 4
FEATURE [App::DocumentObjectGroupPython] Y_element001  label="Y_element : 1"  # scripted group (container) (typed FeaturePython)
  n = 1
  ref = Y_element
FEATURE [App::DocumentObjectGroupPython] G4_Y  # scripted group (container) (typed FeaturePython)
  Dunit = g/cm3
  Dvalue = 4.469
  Group = -> [Y_element001]
  conduct = 2
  density = 1
  expand = 3
  formula = Y
  name = G4_Y
  specific = 4
FEATURE [App::DocumentObjectGroupPython] Zr_element001  label="Zr_element : 1"  # scripted group (container) (typed FeaturePython)
  n = 1
  ref = Zr_element
FEATURE [App::DocumentObjectGroupPython] G4_Zr  # scripted group (container) (typed FeaturePython)
  Dunit = g/cm3
  Dvalue = 6.506
  Group = -> [Zr_element001]
  conduct = 2
  density = 1
  expand = 3
  formula = Zr
  name = G4_Zr
  specific = 4
FEATURE [App::DocumentObjectGroupPython] Nb_element001  label="Nb_element : 1"  # scripted group (container) (typed FeaturePython)
  n = 1
  ref = Nb_element
FEATURE [App::DocumentObjectGroupPython] G4_Nb  # scripted group (container) (typed FeaturePython)
  Dunit = g/cm3
  Dvalue = 8.57
  Group = -> [Nb_element001]
  conduct = 2
  density = 1
  expand = 3
  formula = Nb
  name = G4_Nb
  specific = 4
FEATURE [App::DocumentObjectGroupPython] Mo_element001  label="Mo_element : 1"  # scripted group (container) (typed FeaturePython)
  n = 1
  ref = Mo_element
FEATURE [App::DocumentObjectGroupPython] G4_Mo  # scripted group (container) (typed FeaturePython)
  Dunit = g/cm3
  Dvalue = 10.22
  Group = -> [Mo_element001]
  conduct = 2
  density = 1
  expand = 3
  formula = Mo
  name = G4_Mo
  specific = 4
FEATURE [App::DocumentObjectGroupPython] Tc_element001  label="Tc_element : 1"  # scripted group (container) (typed FeaturePython)
  n = 1
  ref = Tc_element
FEATURE [App::DocumentObjectGroupPython] G4_Tc  # scripted group (container) (typed FeaturePython)
  Dunit = g/cm3
  Dvalue = 11.5
  Group = -> [Tc_element001]
  conduct = 2
  density = 1
  expand = 3
  formula = Tc
  name = G4_Tc
  specific = 4
FEATURE [App::DocumentObjectGroupPython] Ru_element001  label="Ru_element : 1"  # scripted group (container) (typed FeaturePython)
  n = 1
  ref = Ru_element
FEATURE [App::DocumentObjectGroupPython] G4_Ru  # scripted group (container) (typed FeaturePython)
  Dunit = g/cm3
  Dvalue = 12.41
  Group = -> [Ru_element001]
  conduct = 2
  density = 1
  expand = 3
  formula = Ru
  name = G4_Ru
  specific = 4
FEATURE [App::DocumentObjectGroupPython] Rh_element001  label="Rh_element : 1"  # scripted group (container) (typed FeaturePython)
  n = 1
  ref = Rh_element
FEATURE [App::DocumentObjectGroupPython] G4_Rh  # scripted group (container) (typed FeaturePython)
  Dunit = g/cm3
  Dvalue = 12.41
  Group = -> [Rh_element001]
  conduct = 2
  density = 1
  expand = 3
  formula = Rh
  name = G4_Rh
  specific = 4
FEATURE [App::DocumentObjectGroupPython] Pd_element001  label="Pd_element : 1"  # scripted group (container) (typed FeaturePython)
  n = 1
  ref = Pd_element
FEATURE [App::DocumentObjectGroupPython] G4_Pd  # scripted group (container) (typed FeaturePython)
  Dunit = g/cm3
  Dvalue = 12.02
  Group = -> [Pd_element001]
  conduct = 2
  density = 1
  expand = 3
  formula = Pd
  name = G4_Pd
  specific = 4
FEATURE [App::DocumentObjectGroupPython] Ag_element006  label="Ag_element : 004"  # scripted group (container) (typed FeaturePython)
  n = 1
  ref = Ag_element
FEATURE [App::DocumentObjectGroupPython] G4_Ag  # scripted group (container) (typed FeaturePython)
  Dunit = g/cm3
  Dvalue = 10.5
  Group = -> [Ag_element006]
  conduct = 2
  density = 1
  expand = 3
  formula = Ag
  name = G4_Ag
  specific = 4
FEATURE [App::DocumentObjectGroupPython] Cd_element003  label="Cd_element : 003"  # scripted group (container) (typed FeaturePython)
  n = 1
  ref = Cd_element
FEATURE [App::DocumentObjectGroupPython] G4_Cd  # scripted group (container) (typed FeaturePython)
  Dunit = g/cm3
  Dvalue = 8.65
  Group = -> [Cd_element003]
  conduct = 2
  density = 1
  expand = 3
  formula = Cd
  name = G4_Cd
  specific = 4
FEATURE [App::DocumentObjectGroupPython] In_element001  label="In_element : 1"  # scripted group (container) (typed FeaturePython)
  n = 1
  ref = In_element
FEATURE [App::DocumentObjectGroupPython] G4_In  # scripted group (container) (typed FeaturePython)
  Dunit = g/cm3
  Dvalue = 7.31
  Group = -> [In_element001]
  conduct = 2
  density = 1
  expand = 3
  formula = In
  name = G4_In
  specific = 4
FEATURE [App::DocumentObjectGroupPython] Sn_element001  label="Sn_element : 1"  # scripted group (container) (typed FeaturePython)
  n = 1
  ref = Sn_element
FEATURE [App::DocumentObjectGroupPython] G4_Sn  # scripted group (container) (typed FeaturePython)
  Dunit = g/cm3
  Dvalue = 7.31
  Group = -> [Sn_element001]
  conduct = 2
  density = 1
  expand = 3
  formula = Sn
  name = G4_Sn
  specific = 4
FEATURE [App::DocumentObjectGroupPython] Sb_element001  label="Sb_element : 1"  # scripted group (container) (typed FeaturePython)
  n = 1
  ref = Sb_element
FEATURE [App::DocumentObjectGroupPython] G4_Sb  # scripted group (container) (typed FeaturePython)
  Dunit = g/cm3
  Dvalue = 6.691
  Group = -> [Sb_element001]
  conduct = 2
  density = 1
  expand = 3
  formula = Sb
  name = G4_Sb
  specific = 4
FEATURE [App::DocumentObjectGroupPython] Te_element002  label="Te_element : 002"  # scripted group (container) (typed FeaturePython)
  n = 1
  ref = Te_element
FEATURE [App::DocumentObjectGroupPython] G4_Te  # scripted group (container) (typed FeaturePython)
  Dunit = g/cm3
  Dvalue = 6.24
  Group = -> [Te_element002]
  conduct = 2
  density = 1
  expand = 3
  formula = Te
  name = G4_Te
  specific = 4
FEATURE [App::DocumentObjectGroupPython] I_element010  label="I_element : 006"  # scripted group (container) (typed FeaturePython)
  n = 1
  ref = I_element
FEATURE [App::DocumentObjectGroupPython] G4_I  # scripted group (container) (typed FeaturePython)
  Dunit = g/cm3
  Dvalue = 4.93
  Group = -> [I_element010]
  conduct = 2
  density = 1
  expand = 3
  formula = I
  name = G4_I
  specific = 4
FEATURE [App::DocumentObjectGroupPython] Xe_element001  label="Xe_element : 1"  # scripted group (container) (typed FeaturePython)
  n = 1
  ref = Xe_element
FEATURE [App::DocumentObjectGroupPython] G4_Xe  # scripted group (container) (typed FeaturePython)
  Dunit = g/cm3
  Dvalue = 0.00548536
  Group = -> [Xe_element001]
  conduct = 2
  density = 1
  expand = 3
  formula = Xe
  name = G4_Xe
  specific = 4
FEATURE [App::DocumentObjectGroupPython] Cs_element003  label="Cs_element : 003"  # scripted group (container) (typed FeaturePython)
  n = 1
  ref = Cs_element
FEATURE [App::DocumentObjectGroupPython] G4_Cs  # scripted group (container) (typed FeaturePython)
  Dunit = g/cm3
  Dvalue = 1.873
  Group = -> [Cs_element003]
  conduct = 2
  density = 1
  expand = 3
  formula = Cs
  name = G4_Cs
  specific = 4
FEATURE [App::DocumentObjectGroupPython] Ba_element003  label="Ba_element : 003"  # scripted group (container) (typed FeaturePython)
  n = 1
  ref = Ba_element
FEATURE [App::DocumentObjectGroupPython] G4_Ba  # scripted group (container) (typed FeaturePython)
  Dunit = g/cm3
  Dvalue = 3.5
  Group = -> [Ba_element003]
  conduct = 2
  density = 1
  expand = 3
  formula = Ba
  name = G4_Ba
  specific = 4
FEATURE [App::DocumentObjectGroupPython] La_element003  label="La_element : 003"  # scripted group (container) (typed FeaturePython)
  n = 1
  ref = La_element
FEATURE [App::DocumentObjectGroupPython] G4_La  # scripted group (container) (typed FeaturePython)
  Dunit = g/cm3
  Dvalue = 6.154
  Group = -> [La_element003]
  conduct = 2
  density = 1
  expand = 3
  formula = La
  name = G4_La
  specific = 4
FEATURE [App::DocumentObjectGroupPython] Ce_element002  label="Ce_element : 1"  # scripted group (container) (typed FeaturePython)
  n = 1
  ref = Ce_element
FEATURE [App::DocumentObjectGroupPython] G4_Ce  # scripted group (container) (typed FeaturePython)
  Dunit = g/cm3
  Dvalue = 6.657
  Group = -> [Ce_element002]
  conduct = 2
  density = 1
  expand = 3
  formula = Ce
  name = G4_Ce
  specific = 4
FEATURE [App::DocumentObjectGroupPython] Pr_element001  label="Pr_element : 1"  # scripted group (container) (typed FeaturePython)
  n = 1
  ref = Pr_element
FEATURE [App::DocumentObjectGroupPython] G4_Pr  # scripted group (container) (typed FeaturePython)
  Dunit = g/cm3
  Dvalue = 6.71
  Group = -> [Pr_element001]
  conduct = 2
  density = 1
  expand = 3
  formula = Pr
  name = G4_Pr
  specific = 4
FEATURE [App::DocumentObjectGroupPython] Nd_element001  label="Nd_element : 1"  # scripted group (container) (typed FeaturePython)
  n = 1
  ref = Nd_element
FEATURE [App::DocumentObjectGroupPython] G4_Nd  # scripted group (container) (typed FeaturePython)
  Dunit = g/cm3
  Dvalue = 6.9
  Group = -> [Nd_element001]
  conduct = 2
  density = 1
  expand = 3
  formula = Nd
  name = G4_Nd
  specific = 4
FEATURE [App::DocumentObjectGroupPython] Pm_element001  label="Pm_element : 1"  # scripted group (container) (typed FeaturePython)
  n = 1
  ref = Pm_element
FEATURE [App::DocumentObjectGroupPython] G4_Pm  # scripted group (container) (typed FeaturePython)
  Dunit = g/cm3
  Dvalue = 7.22
  Group = -> [Pm_element001]
  conduct = 2
  density = 1
  expand = 3
  formula = Pm
  name = G4_Pm
  specific = 4
FEATURE [App::DocumentObjectGroupPython] Sm_element001  label="Sm_element : 1"  # scripted group (container) (typed FeaturePython)
  n = 1
  ref = Sm_element
FEATURE [App::DocumentObjectGroupPython] G4_Sm  # scripted group (container) (typed FeaturePython)
  Dunit = g/cm3
  Dvalue = 7.46
  Group = -> [Sm_element001]
  conduct = 2
  density = 1
  expand = 3
  formula = Sm
  name = G4_Sm
  specific = 4
FEATURE [App::DocumentObjectGroupPython] Eu_element001  label="Eu_element : 1"  # scripted group (container) (typed FeaturePython)
  n = 1
  ref = Eu_element
FEATURE [App::DocumentObjectGroupPython] G4_Eu  # scripted group (container) (typed FeaturePython)
  Dunit = g/cm3
  Dvalue = 5.243
  Group = -> [Eu_element001]
  conduct = 2
  density = 1
  expand = 3
  formula = Eu
  name = G4_Eu
  specific = 4
FEATURE [App::DocumentObjectGroupPython] Gd_element002  label="Gd_element : 1"  # scripted group (container) (typed FeaturePython)
  n = 1
  ref = Gd_element
FEATURE [App::DocumentObjectGroupPython] G4_Gd  # scripted group (container) (typed FeaturePython)
  Dunit = g/cm3
  Dvalue = 7.9004
  Group = -> [Gd_element002]
  conduct = 2
  density = 1
  expand = 3
  formula = Gd
  name = G4_Gd
  specific = 4
FEATURE [App::DocumentObjectGroupPython] Tb_element001  label="Tb_element : 1"  # scripted group (container) (typed FeaturePython)
  n = 1
  ref = Tb_element
FEATURE [App::DocumentObjectGroupPython] G4_Tb  # scripted group (container) (typed FeaturePython)
  Dunit = g/cm3
  Dvalue = 8.229
  Group = -> [Tb_element001]
  conduct = 2
  density = 1
  expand = 3
  formula = Tb
  name = G4_Tb
  specific = 4
FEATURE [App::DocumentObjectGroupPython] Dy_element001  label="Dy_element : 1"  # scripted group (container) (typed FeaturePython)
  n = 1
  ref = Dy_element
FEATURE [App::DocumentObjectGroupPython] G4_Dy  # scripted group (container) (typed FeaturePython)
  Dunit = g/cm3
  Dvalue = 8.55
  Group = -> [Dy_element001]
  conduct = 2
  density = 1
  expand = 3
  formula = Dy
  name = G4_Dy
  specific = 4
FEATURE [App::DocumentObjectGroupPython] Ho_element001  label="Ho_element : 1"  # scripted group (container) (typed FeaturePython)
  n = 1
  ref = Ho_element
FEATURE [App::DocumentObjectGroupPython] G4_Ho  # scripted group (container) (typed FeaturePython)
  Dunit = g/cm3
  Dvalue = 8.795
  Group = -> [Ho_element001]
  conduct = 2
  density = 1
  expand = 3
  formula = Ho
  name = G4_Ho
  specific = 4
FEATURE [App::DocumentObjectGroupPython] Er_element001  label="Er_element : 1"  # scripted group (container) (typed FeaturePython)
  n = 1
  ref = Er_element
FEATURE [App::DocumentObjectGroupPython] G4_Er  # scripted group (container) (typed FeaturePython)
  Dunit = g/cm3
  Dvalue = 9.066
  Group = -> [Er_element001]
  conduct = 2
  density = 1
  expand = 3
  formula = Er
  name = G4_Er
  specific = 4
FEATURE [App::DocumentObjectGroupPython] Tm_element001  label="Tm_element : 1"  # scripted group (container) (typed FeaturePython)
  n = 1
  ref = Tm_element
FEATURE [App::DocumentObjectGroupPython] G4_Tm  # scripted group (container) (typed FeaturePython)
  Dunit = g/cm3
  Dvalue = 9.321
  Group = -> [Tm_element001]
  conduct = 2
  density = 1
  expand = 3
  formula = Tm
  name = G4_Tm
  specific = 4
FEATURE [App::DocumentObjectGroupPython] Yb_element001  label="Yb_element : 1"  # scripted group (container) (typed FeaturePython)
  n = 1
  ref = Yb_element
FEATURE [App::DocumentObjectGroupPython] G4_Yb  # scripted group (container) (typed FeaturePython)
  Dunit = g/cm3
  Dvalue = 6.73
  Group = -> [Yb_element001]
  conduct = 2
  density = 1
  expand = 3
  formula = Yb
  name = G4_Yb
  specific = 4
FEATURE [App::DocumentObjectGroupPython] Lu_element001  label="Lu_element : 1"  # scripted group (container) (typed FeaturePython)
  n = 1
  ref = Lu_element
FEATURE [App::DocumentObjectGroupPython] G4_Lu  # scripted group (container) (typed FeaturePython)
  Dunit = g/cm3
  Dvalue = 9.84
  Group = -> [Lu_element001]
  conduct = 2
  density = 1
  expand = 3
  formula = Lu
  name = G4_Lu
  specific = 4
FEATURE [App::DocumentObjectGroupPython] Hf_element001  label="Hf_element : 1"  # scripted group (container) (typed FeaturePython)
  n = 1
  ref = Hf_element
FEATURE [App::DocumentObjectGroupPython] G4_Hf  # scripted group (container) (typed FeaturePython)
  Dunit = g/cm3
  Dvalue = 13.31
  Group = -> [Hf_element001]
  conduct = 2
  density = 1
  expand = 3
  formula = Hf
  name = G4_Hf
  specific = 4
FEATURE [App::DocumentObjectGroupPython] Ta_element001  label="Ta_element : 1"  # scripted group (container) (typed FeaturePython)
  n = 1
  ref = Ta_element
FEATURE [App::DocumentObjectGroupPython] G4_Ta  # scripted group (container) (typed FeaturePython)
  Dunit = g/cm3
  Dvalue = 16.654
  Group = -> [Ta_element001]
  conduct = 2
  density = 1
  expand = 3
  formula = Ta
  name = G4_Ta
  specific = 4
FEATURE [App::DocumentObjectGroupPython] W_element004  label="W_element : 004"  # scripted group (container) (typed FeaturePython)
  n = 1
  ref = W_element
FEATURE [App::DocumentObjectGroupPython] G4_W  # scripted group (container) (typed FeaturePython)
  Dunit = g/cm3
  Dvalue = 19.3
  Group = -> [W_element004]
  conduct = 2
  density = 1
  expand = 3
  formula = W
  name = G4_W
  specific = 4
FEATURE [App::DocumentObjectGroupPython] Re_element001  label="Re_element : 1"  # scripted group (container) (typed FeaturePython)
  n = 1
  ref = Re_element
FEATURE [App::DocumentObjectGroupPython] G4_Re  # scripted group (container) (typed FeaturePython)
  Dunit = g/cm3
  Dvalue = 21.02
  Group = -> [Re_element001]
  conduct = 2
  density = 1
  expand = 3
  formula = Re
  name = G4_Re
  specific = 4
FEATURE [App::DocumentObjectGroupPython] Os_element001  label="Os_element : 1"  # scripted group (container) (typed FeaturePython)
  n = 1
  ref = Os_element
FEATURE [App::DocumentObjectGroupPython] G4_Os  # scripted group (container) (typed FeaturePython)
  Dunit = g/cm3
  Dvalue = 22.57
  Group = -> [Os_element001]
  conduct = 2
  density = 1
  expand = 3
  formula = Os
  name = G4_Os
  specific = 4
FEATURE [App::DocumentObjectGroupPython] Ir_element001  label="Ir_element : 1"  # scripted group (container) (typed FeaturePython)
  n = 1
  ref = Ir_element
FEATURE [App::DocumentObjectGroupPython] G4_Ir  # scripted group (container) (typed FeaturePython)
  Dunit = g/cm3
  Dvalue = 22.42
  Group = -> [Ir_element001]
  conduct = 2
  density = 1
  expand = 3
  formula = Ir
  name = G4_Ir
  specific = 4
FEATURE [App::DocumentObjectGroupPython] Pt_element001  label="Pt_element : 1"  # scripted group (container) (typed FeaturePython)
  n = 1
  ref = Pt_element
FEATURE [App::DocumentObjectGroupPython] G4_Pt  # scripted group (container) (typed FeaturePython)
  Dunit = g/cm3
  Dvalue = 21.45
  Group = -> [Pt_element001]
  conduct = 2
  density = 1
  expand = 3
  formula = Pt
  name = G4_Pt
  specific = 4
FEATURE [App::DocumentObjectGroupPython] Au_element001  label="Au_element : 1"  # scripted group (container) (typed FeaturePython)
  n = 1
  ref = Au_element
FEATURE [App::DocumentObjectGroupPython] G4_Au  # scripted group (container) (typed FeaturePython)
  Dunit = g/cm3
  Dvalue = 19.32
  Group = -> [Au_element001]
  conduct = 2
  density = 1
  expand = 3
  formula = Au
  name = G4_Au
  specific = 4
FEATURE [App::DocumentObjectGroupPython] Hg_element002  label="Hg_element : 002"  # scripted group (container) (typed FeaturePython)
  n = 1
  ref = Hg_element
FEATURE [App::DocumentObjectGroupPython] G4_Hg  # scripted group (container) (typed FeaturePython)
  Dunit = g/cm3
  Dvalue = 13.546
  Group = -> [Hg_element002]
  conduct = 2
  density = 1
  expand = 3
  formula = Hg
  name = G4_Hg
  specific = 4
FEATURE [App::DocumentObjectGroupPython] Tl_element002  label="Tl_element : 002"  # scripted group (container) (typed FeaturePython)
  n = 1
  ref = Tl_element
FEATURE [App::DocumentObjectGroupPython] G4_Tl  # scripted group (container) (typed FeaturePython)
  Dunit = g/cm3
  Dvalue = 11.72
  Group = -> [Tl_element002]
  conduct = 2
  density = 1
  expand = 3
  formula = Tl
  name = G4_Tl
  specific = 4
FEATURE [App::DocumentObjectGroupPython] Pb_element003  label="Pb_element : 1"  # scripted group (container) (typed FeaturePython)
  n = 1
  ref = Pb_element
FEATURE [App::DocumentObjectGroupPython] G4_Pb  # scripted group (container) (typed FeaturePython)
  Dunit = g/cm3
  Dvalue = 11.35
  Group = -> [Pb_element003]
  conduct = 2
  density = 1
  expand = 3
  formula = Pb
  name = G4_Pb
  specific = 4
FEATURE [App::DocumentObjectGroupPython] Bi_element002  label="Bi_element : 1"  # scripted group (container) (typed FeaturePython)
  n = 1
  ref = Bi_element
FEATURE [App::DocumentObjectGroupPython] G4_Bi  # scripted group (container) (typed FeaturePython)
  Dunit = g/cm3
  Dvalue = 9.747
  Group = -> [Bi_element002]
  conduct = 2
  density = 1
  expand = 3
  formula = Bi
  name = G4_Bi
  specific = 4
FEATURE [App::DocumentObjectGroupPython] Po_element001  label="Po_element : 1"  # scripted group (container) (typed FeaturePython)
  n = 1
  ref = Po_element
FEATURE [App::DocumentObjectGroupPython] G4_Po  # scripted group (container) (typed FeaturePython)
  Dunit = g/cm3
  Dvalue = 9.32
  Group = -> [Po_element001]
  conduct = 2
  density = 1
  expand = 3
  formula = Po
  name = G4_Po
  specific = 4
FEATURE [App::DocumentObjectGroupPython] At_element001  label="At_element : 1"  # scripted group (container) (typed FeaturePython)
  n = 1
  ref = At_element
FEATURE [App::DocumentObjectGroupPython] G4_At  # scripted group (container) (typed FeaturePython)
  Dunit = g/cm3
  Dvalue = 9.32
  Group = -> [At_element001]
  conduct = 2
  density = 1
  expand = 3
  formula = At
  name = G4_At
  specific = 4
FEATURE [App::DocumentObjectGroupPython] Rn_element001  label="Rn_element : 1"  # scripted group (container) (typed FeaturePython)
  n = 1
  ref = Rn_element
FEATURE [App::DocumentObjectGroupPython] G4_Rn  # scripted group (container) (typed FeaturePython)
  Dunit = g/cm3
  Dvalue = 0.00900662
  Group = -> [Rn_element001]
  conduct = 2
  density = 1
  expand = 3
  formula = Rn
  name = G4_Rn
  specific = 4
FEATURE [App::DocumentObjectGroupPython] Fr_element001  label="Fr_element : 1"  # scripted group (container) (typed FeaturePython)
  n = 1
  ref = Fr_element
FEATURE [App::DocumentObjectGroupPython] G4_Fr  # scripted group (container) (typed FeaturePython)
  Dunit = g/cm3
  Dvalue = 1
  Group = -> [Fr_element001]
  conduct = 2
  density = 1
  expand = 3
  formula = Fr
  name = G4_Fr
  specific = 4
FEATURE [App::DocumentObjectGroupPython] Ra_element001  label="Ra_element : 1"  # scripted group (container) (typed FeaturePython)
  n = 1
  ref = Ra_element
FEATURE [App::DocumentObjectGroupPython] G4_Ra  # scripted group (container) (typed FeaturePython)
  Dunit = g/cm3
  Dvalue = 5
  Group = -> [Ra_element001]
  conduct = 2
  density = 1
  expand = 3
  formula = Ra
  name = G4_Ra
  specific = 4
FEATURE [App::DocumentObjectGroupPython] Ac_element001  label="Ac_element : 1"  # scripted group (container) (typed FeaturePython)
  n = 1
  ref = Ac_element
FEATURE [App::DocumentObjectGroupPython] G4_Ac  # scripted group (container) (typed FeaturePython)
  Dunit = g/cm3
  Dvalue = 10.07
  Group = -> [Ac_element001]
  conduct = 2
  density = 1
  expand = 3
  formula = Ac
  name = G4_Ac
  specific = 4
FEATURE [App::DocumentObjectGroupPython] Th_element001  label="Th_element : 1"  # scripted group (container) (typed FeaturePython)
  n = 1
  ref = Th_element
FEATURE [App::DocumentObjectGroupPython] G4_Th  # scripted group (container) (typed FeaturePython)
  Dunit = g/cm3
  Dvalue = 11.72
  Group = -> [Th_element001]
  conduct = 2
  density = 1
  expand = 3
  formula = Th
  name = G4_Th
  specific = 4
FEATURE [App::DocumentObjectGroupPython] Pa_element001  label="Pa_element : 1"  # scripted group (container) (typed FeaturePython)
  n = 1
  ref = Pa_element
FEATURE [App::DocumentObjectGroupPython] G4_Pa  # scripted group (container) (typed FeaturePython)
  Dunit = g/cm3
  Dvalue = 15.37
  Group = -> [Pa_element001]
  conduct = 2
  density = 1
  expand = 3
  formula = Pa
  name = G4_Pa
  specific = 4
FEATURE [App::DocumentObjectGroupPython] U_element004  label="U_element : 004"  # scripted group (container) (typed FeaturePython)
  n = 1
  ref = U_element
FEATURE [App::DocumentObjectGroupPython] G4_U  # scripted group (container) (typed FeaturePython)
  Dunit = g/cm3
  Dvalue = 18.95
  Group = -> [U_element004]
  conduct = 2
  density = 1
  expand = 3
  formula = U
  name = G4_U
  specific = 4
FEATURE [App::DocumentObjectGroupPython] Np_element001  label="Np_element : 1"  # scripted group (container) (typed FeaturePython)
  n = 1
  ref = Np_element
FEATURE [App::DocumentObjectGroupPython] G4_Np  # scripted group (container) (typed FeaturePython)
  Dunit = g/cm3
  Dvalue = 20.25
  Group = -> [Np_element001]
  conduct = 2
  density = 1
  expand = 3
  formula = Np
  name = G4_Np
  specific = 4
FEATURE [App::DocumentObjectGroupPython] Pu_element002  label="Pu_element : 002"  # scripted group (container) (typed FeaturePython)
  n = 1
  ref = Pu_element
FEATURE [App::DocumentObjectGroupPython] G4_Pu  # scripted group (container) (typed FeaturePython)
  Dunit = g/cm3
  Dvalue = 19.84
  Group = -> [Pu_element002]
  conduct = 2
  density = 1
  expand = 3
  formula = Pu
  name = G4_Pu
  specific = 4
FEATURE [App::DocumentObjectGroupPython] Am_element001  label="Am_element : 1"  # scripted group (container) (typed FeaturePython)
  n = 1
  ref = Am_element
FEATURE [App::DocumentObjectGroupPython] G4_Am  # scripted group (container) (typed FeaturePython)
  Dunit = g/cm3
  Dvalue = 13.67
  Group = -> [Am_element001]
  conduct = 2
  density = 1
  expand = 3
  formula = Am
  name = G4_Am
  specific = 4
FEATURE [App::DocumentObjectGroupPython] Cm_element001  label="Cm_element : 1"  # scripted group (container) (typed FeaturePython)
  n = 1
  ref = Cm_element
FEATURE [App::DocumentObjectGroupPython] G4_Cm  # scripted group (container) (typed FeaturePython)
  Dunit = g/cm3
  Dvalue = 13.51
  Group = -> [Cm_element001]
  conduct = 2
  density = 1
  expand = 3
  formula = Cm
  name = G4_Cm
  specific = 4
FEATURE [App::DocumentObjectGroupPython] Bk_element001  label="Bk_element : 1"  # scripted group (container) (typed FeaturePython)
  n = 1
  ref = Bk_element
FEATURE [App::DocumentObjectGroupPython] G4_Bk  # scripted group (container) (typed FeaturePython)
  Dunit = g/cm3
  Dvalue = 14
  Group = -> [Bk_element001]
  conduct = 2
  density = 1
  expand = 3
  formula = Bk
  name = G4_Bk
  specific = 4
FEATURE [App::DocumentObjectGroupPython] Cf_element001  label="Cf_element : 1"  # scripted group (container) (typed FeaturePython)
  n = 1
  ref = Cf_element
FEATURE [App::DocumentObjectGroupPython] G4_Cf  # scripted group (container) (typed FeaturePython)
  Dunit = g/cm3
  Dvalue = 10
  Group = -> [Cf_element001]
  conduct = 2
  density = 1
  expand = 3
  formula = Cf
  name = G4_Cf
  specific = 4
FEATURE [App::DocumentObjectGroupPython] Element  # scripted group (container) (typed FeaturePython)
  Group = -> [G4_H,G4_He,G4_Li,G4_Be,G4_B,G4_C,G4_N,G4_O,G4_F,G4_Ne,G4_Na,G4_Mg,G4_Al,G4_Si,G4_P,G4_S,G4_Cl,G4_Ar,G4_K,G4_Ca,G4_Sc,G4_Ti,G4_V,G4_Cr,G4_Mn,G4_Fe,G4_Co,G4_Ni,G4_Cu,G4_Zn,G4_Ga,G4_Ge,G4_As,G4_Se,G4_Br,G4_Kr,G4_Rb,G4_Sr,G4_Y,G4_Zr,G4_Nb,G4_Mo,G4_Tc,G4_Ru,G4_Rh,G4_Pd,G4_Ag,G4_Cd,G4_In,G4_Sn,G4_Sb,G4_Te,G4_I,G4_Xe,G4_Cs,G4_Ba,G4_La,G4_Ce,G4_Pr,G4_Nd,G4_Pm,G4_Sm,G4_Eu,G4_Gd,G4_Tb,G4_Dy,G4_Ho,G4_Er,+30 more]
FEATURE [App::DocumentObjectGroupPython] H_element114  label="H_element : 063"  # scripted group (container) (typed FeaturePython)
  n = 2
  ref = H_element
FEATURE [App::DocumentObjectGroupPython] G4_lH2  # scripted group (container) (typed FeaturePython)
  Dunit = g/cm3
  Dvalue = 0.0708
  Group = -> [H_element114]
  conduct = 2
  density = 1
  expand = 3
  formula = G4_lH2
  name = G4_lH2
  specific = 4
FEATURE [App::DocumentObjectGroupPython] N_element049  label="N_element : 022"  # scripted group (container) (typed FeaturePython)
  n = 2
  ref = N_element
FEATURE [App::DocumentObjectGroupPython] G4_lN2  # scripted group (container) (typed FeaturePython)
  Dunit = g/cm3
  Dvalue = 0.807
  Group = -> [N_element049]
  conduct = 2
  density = 1
  expand = 3
  formula = G4_lN2
  name = G4_lN2
  specific = 4
FEATURE [App::DocumentObjectGroupPython] O_element106  label="O_element : 060"  # scripted group (container) (typed FeaturePython)
  n = 2
  ref = O_element
FEATURE [App::DocumentObjectGroupPython] G4_lO2  # scripted group (container) (typed FeaturePython)
  Dunit = g/cm3
  Dvalue = 1.141
  Group = -> [O_element106]
  conduct = 2
  density = 1
  expand = 3
  formula = G4_lO2
  name = G4_lO2
  specific = 4
FEATURE [App::DocumentObjectGroupPython] Ar  label="Ar : 1"  # scripted group (container) (typed FeaturePython)
  n = 1
  ref = Ar
FEATURE [App::DocumentObjectGroupPython] G4_lAr  # scripted group (container) (typed FeaturePython)
  Dunit = g/cm3
  Dvalue = 1.396
  Group = -> [Ar]
  conduct = 2
  density = 1
  expand = 3
  formula = G4_lAr
  name = G4_lAr
  specific = 4
FEATURE [App::DocumentObjectGroupPython] Br  label="Br : 1"  # scripted group (container) (typed FeaturePython)
  n = 1
  ref = Br
FEATURE [App::DocumentObjectGroupPython] G4_lBr  # scripted group (container) (typed FeaturePython)
  Dunit = g/cm3
  Dvalue = 3.1028
  Group = -> [Br]
  conduct = 2
  density = 1
  expand = 3
  formula = G4_lBr
  name = G4_lBr
  specific = 4
FEATURE [App::DocumentObjectGroupPython] Kr  label="Kr : 1"  # scripted group (container) (typed FeaturePython)
  n = 1
  ref = Kr
FEATURE [App::DocumentObjectGroupPython] G4_lKr  # scripted group (container) (typed FeaturePython)
  Dunit = g/cm3
  Dvalue = 2.418
  Group = -> [Kr]
  conduct = 2
  density = 1
  expand = 3
  formula = G4_lKr
  name = G4_lKr
  specific = 4
FEATURE [App::DocumentObjectGroupPython] Xe  label="Xe : 1"  # scripted group (container) (typed FeaturePython)
  n = 1
  ref = Xe
FEATURE [App::DocumentObjectGroupPython] G4_lXe  # scripted group (container) (typed FeaturePython)
  Dunit = g/cm3
  Dvalue = 2.953
  Group = -> [Xe]
  conduct = 2
  density = 1
  expand = 3
  formula = G4_lXe
  name = G4_lXe
  specific = 4
FEATURE [App::DocumentObjectGroupPython] O_element107  label="O_element : 061"  # scripted group (container) (typed FeaturePython)
  n = 4
  ref = O_element
FEATURE [App::DocumentObjectGroupPython] Pb_element004  label="Pb_element : 002"  # scripted group (container) (typed FeaturePython)
  n = 1
  ref = Pb_element
FEATURE [App::DocumentObjectGroupPython] W_element005  label="W_element : 005"  # scripted group (container) (typed FeaturePython)
  n = 1
  ref = W_element
FEATURE [App::DocumentObjectGroupPython] G4_PbWO4  # scripted group (container) (typed FeaturePython)
  Dunit = g/cm3
  Dvalue = 8.28
  Group = -> [O_element107,Pb_element004,W_element005]
  conduct = 2
  density = 1
  expand = 3
  formula = G4_PbWO4
  name = G4_PbWO4
  specific = 4
FEATURE [App::DocumentObjectGroupPython] alactic  label="alactic : 1"  # scripted group (container) (typed FeaturePython)
  n = 1
  ref = alactic
FEATURE [App::DocumentObjectGroupPython] G4_Galactic  # scripted group (container) (typed FeaturePython)
  Dunit = g/cm3
  Dvalue = 0
  Group = -> [alactic]
  conduct = 2
  density = 1
  expand = 3
  formula = G4_Galactic
  name = G4_Galactic
  specific = 4
FEATURE [App::DocumentObjectGroupPython] RAPHITE_POROUS  label="RAPHITE_POROUS : 1"  # scripted group (container) (typed FeaturePython)
  n = 1
  ref = RAPHITE_POROUS
FEATURE [App::DocumentObjectGroupPython] G4_GRAPHITE_POROUS  # scripted group (container) (typed FeaturePython)
  Dunit = g/cm3
  Dvalue = 1.7
  Group = -> [RAPHITE_POROUS]
  conduct = 2
  density = 1
  expand = 3
  formula = G4_GRAPHITE_POROUS
  name = G4_GRAPHITE_POROUS
  specific = 4
FEATURE [App::DocumentObjectGroupPython] H_element115  label="H_element : 0.150"  # scripted group (container) (typed FeaturePython)
  n = 0.080538
FEATURE [App::DocumentObjectGroupPython] C_element125  label="C_element : 0.600"  # scripted group (container) (typed FeaturePython)
  n = 0.599848
FEATURE [App::DocumentObjectGroupPython] O_element108  label="O_element : 0.320"  # scripted group (container) (typed FeaturePython)
  n = 0.319614
FEATURE [App::DocumentObjectGroupPython] G4_LUCITE  # scripted group (container) (typed FeaturePython)
  Dunit = g/cm3
  Dvalue = 1.19
  Group = -> [H_element115,C_element125,O_element108]
  conduct = 2
  density = 1
  expand = 3
  formula = G4_LUCITE
  name = G4_LUCITE
  specific = 4
FEATURE [App::DocumentObjectGroupPython] Cu_element002  label="Cu_element : 62"  # scripted group (container) (typed FeaturePython)
  n = 62
  ref = Cu_element
FEATURE [App::DocumentObjectGroupPython] Zn_element002  label="Zn_element : 35"  # scripted group (container) (typed FeaturePython)
  n = 35
  ref = Zn_element
FEATURE [App::DocumentObjectGroupPython] Pb_element005  label="Pb_element : 3"  # scripted group (container) (typed FeaturePython)
  n = 3
  ref = Pb_element
FEATURE [App::DocumentObjectGroupPython] G4_BRASS  # scripted group (container) (typed FeaturePython)
  Dunit = g/cm3
  Dvalue = 8.52
  Group = -> [Cu_element002,Zn_element002,Pb_element005]
  conduct = 2
  density = 1
  expand = 3
  formula = G4_BRASS
  name = G4_BRASS
  specific = 4
FEATURE [App::DocumentObjectGroupPython] Cu_element003  label="Cu_element : 89"  # scripted group (container) (typed FeaturePython)
  n = 89
  ref = Cu_element
FEATURE [App::DocumentObjectGroupPython] Zn_element003  label="Zn_element : 9"  # scripted group (container) (typed FeaturePython)
  n = 9
  ref = Zn_element
FEATURE [App::DocumentObjectGroupPython] Pb_element006  label="Pb_element : 2"  # scripted group (container) (typed FeaturePython)
  n = 2
  ref = Pb_element
FEATURE [App::DocumentObjectGroupPython] G4_BRONZE  # scripted group (container) (typed FeaturePython)
  Dunit = g/cm3
  Dvalue = 8.82
  Group = -> [Cu_element003,Zn_element003,Pb_element006]
  conduct = 2
  density = 1
  expand = 3
  formula = G4_BRONZE
  name = G4_BRONZE
  specific = 4
FEATURE [App::DocumentObjectGroupPython] Fe_element008  label="Fe_element : 74"  # scripted group (container) (typed FeaturePython)
  n = 74
  ref = Fe_element
FEATURE [App::DocumentObjectGroupPython] Cr_element002  label="Cr_element : 18"  # scripted group (container) (typed FeaturePython)
  n = 18
  ref = Cr_element
FEATURE [App::DocumentObjectGroupPython] Ni_element002  label="Ni_element : 8"  # scripted group (container) (typed FeaturePython)
  n = 8
  ref = Ni_element
FEATURE [App::DocumentObjectGroupPython] G4_STAINLESS_STEEL  label="G4_STAINLESS-STEEL"  # scripted group (container) (typed FeaturePython)
  Dunit = g/cm3
  Dvalue = 8
  Group = -> [Fe_element008,Cr_element002,Ni_element002]
  conduct = 2
  density = 1
  expand = 3
  formula = G4_STAINLESS-STEEL
  name = G4_STAINLESS-STEEL
  specific = 4
FEATURE [App::DocumentObjectGroupPython] H_element116  label="H_element : 064"  # scripted group (container) (typed FeaturePython)
  n = 18
  ref = H_element
FEATURE [App::DocumentObjectGroupPython] C_element126  label="C_element : 071"  # scripted group (container) (typed FeaturePython)
  n = 12
  ref = C_element
FEATURE [App::DocumentObjectGroupPython] O_element109  label="O_element : 062"  # scripted group (container) (typed FeaturePython)
  n = 7
  ref = O_element
FEATURE [App::DocumentObjectGroupPython] G4_CR39  # scripted group (container) (typed FeaturePython)
  Dunit = g/cm3
  Dvalue = 1.32
  Group = -> [H_element116,C_element126,O_element109]
  conduct = 2
  density = 1
  expand = 3
  formula = G4_CR39
  name = G4_CR39
  specific = 4
FEATURE [App::DocumentObjectGroupPython] H_element117  label="H_element : 38"  # scripted group (container) (typed FeaturePython)
  n = 38
  ref = H_element
FEATURE [App::DocumentObjectGroupPython] C_element127  label="C_element : 072"  # scripted group (container) (typed FeaturePython)
  n = 18
  ref = C_element
FEATURE [App::DocumentObjectGroupPython] O_element110  label="O_element : 063"  # scripted group (container) (typed FeaturePython)
  n = 1
  ref = O_element
FEATURE [App::DocumentObjectGroupPython] G4_OCTADECANOL  # scripted group (container) (typed FeaturePython)
  Dunit = g/cm3
  Dvalue = 0.812
  Group = -> [H_element117,C_element127,O_element110]
  conduct = 2
  density = 1
  expand = 3
  formula = G4_OCTADECANOL
  name = G4_OCTADECANOL
  specific = 4
FEATURE [App::DocumentObjectGroupPython] HEP  # scripted group (container) (typed FeaturePython)
  Group = -> [G4_lH2,G4_lN2,G4_lO2,G4_lAr,G4_lBr,G4_lKr,G4_lXe,G4_PbWO4,G4_Galactic,G4_GRAPHITE_POROUS,G4_LUCITE,G4_BRASS,G4_BRONZE,G4_STAINLESS_STEEL,G4_CR39,G4_OCTADECANOL]
FEATURE [App::DocumentObjectGroupPython] C_element128  label="C_element : 073"  # scripted group (container) (typed FeaturePython)
  n = 14
  ref = C_element
FEATURE [App::DocumentObjectGroupPython] H_element118  label="H_element : 065"  # scripted group (container) (typed FeaturePython)
  n = 10
  ref = H_element
FEATURE [App::DocumentObjectGroupPython] O_element111  label="O_element : 064"  # scripted group (container) (typed FeaturePython)
  n = 2
  ref = O_element
FEATURE [App::DocumentObjectGroupPython] N_element050  label="N_element : 023"  # scripted group (container) (typed FeaturePython)
  n = 2
  ref = N_element
FEATURE [App::DocumentObjectGroupPython] G4_KEVLAR  # scripted group (container) (typed FeaturePython)
  Dunit = g/cm3
  Dvalue = 1.44
  Group = -> [C_element128,H_element118,O_element111,N_element050]
  conduct = 2
  density = 1
  expand = 3
  formula = G4_KEVLAR
  name = G4_KEVLAR
  specific = 4
FEATURE [App::DocumentObjectGroupPython] C_element129  label="C_element : 074"  # scripted group (container) (typed FeaturePython)
  n = 10
  ref = C_element
FEATURE [App::DocumentObjectGroupPython] H_element119  label="H_element : 066"  # scripted group (container) (typed FeaturePython)
  n = 8
  ref = H_element
FEATURE [App::DocumentObjectGroupPython] O_element112  label="O_element : 065"  # scripted group (container) (typed FeaturePython)
  n = 4
  ref = O_element
FEATURE [App::DocumentObjectGroupPython] G4_DACRON  # scripted group (container) (typed FeaturePython)
  Dunit = g/cm3
  Dvalue = 1.4
  Group = -> [C_element129,H_element119,O_element112]
  conduct = 2
  density = 1
  expand = 3
  formula = G4_DACRON
  name = G4_DACRON
  specific = 4
FEATURE [App::DocumentObjectGroupPython] C_element130  label="C_element : 075"  # scripted group (container) (typed FeaturePython)
  n = 4
  ref = C_element
FEATURE [App::DocumentObjectGroupPython] H_element120  label="H_element : 067"  # scripted group (container) (typed FeaturePython)
  n = 5
  ref = H_element
FEATURE [App::DocumentObjectGroupPython] Cl_element030  label="Cl_element : 016"  # scripted group (container) (typed FeaturePython)
  n = 1
  ref = Cl_element
FEATURE [App::DocumentObjectGroupPython] G4_NEOPRENE  # scripted group (container) (typed FeaturePython)
  Dunit = g/cm3
  Dvalue = 1.23
  Group = -> [C_element130,H_element120,Cl_element030]
  conduct = 2
  density = 1
  expand = 3
  formula = G4_NEOPRENE
  name = G4_NEOPRENE
  specific = 4
FEATURE [App::DocumentObjectGroupPython] Space  # scripted group (container) (typed FeaturePython)
  Group = -> [G4_KEVLAR,G4_DACRON,G4_NEOPRENE]
FEATURE [App::DocumentObjectGroupPython] H_element121  label="H_element : 068"  # scripted group (container) (typed FeaturePython)
  n = 5
  ref = H_element
FEATURE [App::DocumentObjectGroupPython] C_element131  label="C_element : 076"  # scripted group (container) (typed FeaturePython)
  n = 4
  ref = C_element
FEATURE [App::DocumentObjectGroupPython] N_element051  label="N_element : 3"  # scripted group (container) (typed FeaturePython)
  n = 3
  ref = N_element
FEATURE [App::DocumentObjectGroupPython] O_element113  label="O_element : 066"  # scripted group (container) (typed FeaturePython)
  n = 1
  ref = O_element
FEATURE [App::DocumentObjectGroupPython] G4_CYTOSINE  # scripted group (container) (typed FeaturePython)
  Dunit = g/cm3
  Dvalue = 1.55
  Group = -> [H_element121,C_element131,N_element051,O_element113]
  conduct = 2
  density = 1
  expand = 3
  formula = G4_CYTOSINE
  name = G4_CYTOSINE
  specific = 4
FEATURE [App::DocumentObjectGroupPython] H_element122  label="H_element : 069"  # scripted group (container) (typed FeaturePython)
  n = 6
  ref = H_element
FEATURE [App::DocumentObjectGroupPython] C_element132  label="C_element : 077"  # scripted group (container) (typed FeaturePython)
  n = 5
  ref = C_element
FEATURE [App::DocumentObjectGroupPython] N_element052  label="N_element : 024"  # scripted group (container) (typed FeaturePython)
  n = 2
  ref = N_element
FEATURE [App::DocumentObjectGroupPython] O_element114  label="O_element : 067"  # scripted group (container) (typed FeaturePython)
  n = 2
  ref = O_element
FEATURE [App::DocumentObjectGroupPython] G4_THYMINE  # scripted group (container) (typed FeaturePython)
  Dunit = g/cm3
  Dvalue = 1.23
  Group = -> [H_element122,C_element132,N_element052,O_element114]
  conduct = 2
  density = 1
  expand = 3
  formula = G4_THYMINE
  name = G4_THYMINE
  specific = 4
FEATURE [App::DocumentObjectGroupPython] H_element123  label="H_element : 070"  # scripted group (container) (typed FeaturePython)
  n = 4
  ref = H_element
FEATURE [App::DocumentObjectGroupPython] C_element133  label="C_element : 078"  # scripted group (container) (typed FeaturePython)
  n = 4
  ref = C_element
FEATURE [App::DocumentObjectGroupPython] N_element053  label="N_element : 025"  # scripted group (container) (typed FeaturePython)
  n = 2
  ref = N_element
FEATURE [App::DocumentObjectGroupPython] O_element115  label="O_element : 068"  # scripted group (container) (typed FeaturePython)
  n = 2
  ref = O_element
FEATURE [App::DocumentObjectGroupPython] G4_URACIL  # scripted group (container) (typed FeaturePython)
  Dunit = g/cm3
  Dvalue = 1.32
  Group = -> [H_element123,C_element133,N_element053,O_element115]
  conduct = 2
  density = 1
  expand = 3
  formula = G4_URACIL
  name = G4_URACIL
  specific = 4
FEATURE [App::DocumentObjectGroupPython] H_element124  label="H_element : 071"  # scripted group (container) (typed FeaturePython)
  n = 4
  ref = H_element
FEATURE [App::DocumentObjectGroupPython] C_element134  label="C_element : 079"  # scripted group (container) (typed FeaturePython)
  n = 5
  ref = C_element
FEATURE [App::DocumentObjectGroupPython] N_element054  label="N_element : 026"  # scripted group (container) (typed FeaturePython)
  n = 5
  ref = N_element
FEATURE [App::DocumentObjectGroupPython] G4_DNA_ADENINE  # scripted group (container) (typed FeaturePython)
  Dunit = g/cm3
  Dvalue = 1
  Group = -> [H_element124,C_element134,N_element054]
  conduct = 2
  density = 1
  expand = 3
  formula = G4_DNA_ADENINE
  name = G4_DNA_ADENINE
  specific = 4
FEATURE [App::DocumentObjectGroupPython] H_element125  label="H_element : 072"  # scripted group (container) (typed FeaturePython)
  n = 4
  ref = H_element
FEATURE [App::DocumentObjectGroupPython] C_element135  label="C_element : 080"  # scripted group (container) (typed FeaturePython)
  n = 5
  ref = C_element
FEATURE [App::DocumentObjectGroupPython] N_element055  label="N_element : 027"  # scripted group (container) (typed FeaturePython)
  n = 5
  ref = N_element
FEATURE [App::DocumentObjectGroupPython] O_element116  label="O_element : 069"  # scripted group (container) (typed FeaturePython)
  n = 1
  ref = O_element
FEATURE [App::DocumentObjectGroupPython] G4_DNA_GUANINE  # scripted group (container) (typed FeaturePython)
  Dunit = g/cm3
  Dvalue = 1
  Group = -> [H_element125,C_element135,N_element055,O_element116]
  conduct = 2
  density = 1
  expand = 3
  formula = G4_DNA_GUANINE
  name = G4_DNA_GUANINE
  specific = 4
FEATURE [App::DocumentObjectGroupPython] H_element126  label="H_element : 073"  # scripted group (container) (typed FeaturePython)
  n = 4
  ref = H_element
FEATURE [App::DocumentObjectGroupPython] C_element136  label="C_element : 081"  # scripted group (container) (typed FeaturePython)
  n = 4
  ref = C_element
FEATURE [App::DocumentObjectGroupPython] N_element056  label="N_element : 028"  # scripted group (container) (typed FeaturePython)
  n = 3
  ref = N_element
FEATURE [App::DocumentObjectGroupPython] O_element117  label="O_element : 070"  # scripted group (container) (typed FeaturePython)
  n = 1
  ref = O_element
FEATURE [App::DocumentObjectGroupPython] G4_DNA_CYTOSINE  # scripted group (container) (typed FeaturePython)
  Dunit = g/cm3
  Dvalue = 1
  Group = -> [H_element126,C_element136,N_element056,O_element117]
  conduct = 2
  density = 1
  expand = 3
  formula = G4_DNA_CYTOSINE
  name = G4_DNA_CYTOSINE
  specific = 4
FEATURE [App::DocumentObjectGroupPython] H_element127  label="H_element : 074"  # scripted group (container) (typed FeaturePython)
  n = 5
  ref = H_element
FEATURE [App::DocumentObjectGroupPython] C_element137  label="C_element : 082"  # scripted group (container) (typed FeaturePython)
  n = 5
  ref = C_element
FEATURE [App::DocumentObjectGroupPython] N_element057  label="N_element : 029"  # scripted group (container) (typed FeaturePython)
  n = 2
  ref = N_element
FEATURE [App::DocumentObjectGroupPython] O_element118  label="O_element : 071"  # scripted group (container) (typed FeaturePython)
  n = 2
  ref = O_element
FEATURE [App::DocumentObjectGroupPython] G4_DNA_THYMINE  # scripted group (container) (typed FeaturePython)
  Dunit = g/cm3
  Dvalue = 1
  Group = -> [H_element127,C_element137,N_element057,O_element118]
  conduct = 2
  density = 1
  expand = 3
  formula = G4_DNA_THYMINE
  name = G4_DNA_THYMINE
  specific = 4
FEATURE [App::DocumentObjectGroupPython] H_element128  label="H_element : 075"  # scripted group (container) (typed FeaturePython)
  n = 3
  ref = H_element
FEATURE [App::DocumentObjectGroupPython] C_element138  label="C_element : 083"  # scripted group (container) (typed FeaturePython)
  n = 4
  ref = C_element
FEATURE [App::DocumentObjectGroupPython] N_element058  label="N_element : 030"  # scripted group (container) (typed FeaturePython)
  n = 2
  ref = N_element
FEATURE [App::DocumentObjectGroupPython] O_element119  label="O_element : 072"  # scripted group (container) (typed FeaturePython)
  n = 2
  ref = O_element
FEATURE [App::DocumentObjectGroupPython] G4_DNA_URACIL  # scripted group (container) (typed FeaturePython)
  Dunit = g/cm3
  Dvalue = 1
  Group = -> [H_element128,C_element138,N_element058,O_element119]
  conduct = 2
  density = 1
  expand = 3
  formula = G4_DNA_URACIL
  name = G4_DNA_URACIL
  specific = 4
FEATURE [App::DocumentObjectGroupPython] H_element129  label="H_element : 076"  # scripted group (container) (typed FeaturePython)
  n = 10
  ref = H_element
FEATURE [App::DocumentObjectGroupPython] C_element139  label="C_element : 084"  # scripted group (container) (typed FeaturePython)
  n = 10
  ref = C_element
FEATURE [App::DocumentObjectGroupPython] N_element059  label="N_element : 031"  # scripted group (container) (typed FeaturePython)
  n = 5
  ref = N_element
FEATURE [App::DocumentObjectGroupPython] O_element120  label="O_element : 073"  # scripted group (container) (typed FeaturePython)
  n = 4
  ref = O_element
FEATURE [App::DocumentObjectGroupPython] G4_DNA_ADENOSINE  # scripted group (container) (typed FeaturePython)
  Dunit = g/cm3
  Dvalue = 1
  Group = -> [H_element129,C_element139,N_element059,O_element120]
  conduct = 2
  density = 1
  expand = 3
  formula = G4_DNA_ADENOSINE
  name = G4_DNA_ADENOSINE
  specific = 4
FEATURE [App::DocumentObjectGroupPython] H_element130  label="H_element : 077"  # scripted group (container) (typed FeaturePython)
  n = 10
  ref = H_element
FEATURE [App::DocumentObjectGroupPython] C_element140  label="C_element : 085"  # scripted group (container) (typed FeaturePython)
  n = 10
  ref = C_element
FEATURE [App::DocumentObjectGroupPython] N_element060  label="N_element : 032"  # scripted group (container) (typed FeaturePython)
  n = 5
  ref = N_element
FEATURE [App::DocumentObjectGroupPython] O_element121  label="O_element : 074"  # scripted group (container) (typed FeaturePython)
  n = 5
  ref = O_element
FEATURE [App::DocumentObjectGroupPython] G4_DNA_GUANOSINE  # scripted group (container) (typed FeaturePython)
  Dunit = g/cm3
  Dvalue = 1
  Group = -> [H_element130,C_element140,N_element060,O_element121]
  conduct = 2
  density = 1
  expand = 3
  formula = G4_DNA_GUANOSINE
  name = G4_DNA_GUANOSINE
  specific = 4
FEATURE [App::DocumentObjectGroupPython] H_element131  label="H_element : 078"  # scripted group (container) (typed FeaturePython)
  n = 10
  ref = H_element
FEATURE [App::DocumentObjectGroupPython] C_element141  label="C_element : 086"  # scripted group (container) (typed FeaturePython)
  n = 9
  ref = C_element
FEATURE [App::DocumentObjectGroupPython] N_element061  label="N_element : 033"  # scripted group (container) (typed FeaturePython)
  n = 3
  ref = N_element
FEATURE [App::DocumentObjectGroupPython] O_element122  label="O_element : 075"  # scripted group (container) (typed FeaturePython)
  n = 5
  ref = O_element
FEATURE [App::DocumentObjectGroupPython] G4_DNA_CYTIDINE  # scripted group (container) (typed FeaturePython)
  Dunit = g/cm3
  Dvalue = 1
  Group = -> [H_element131,C_element141,N_element061,O_element122]
  conduct = 2
  density = 1
  expand = 3
  formula = G4_DNA_CYTIDINE
  name = G4_DNA_CYTIDINE
  specific = 4
FEATURE [App::DocumentObjectGroupPython] H_element132  label="H_element : 079"  # scripted group (container) (typed FeaturePython)
  n = 9
  ref = H_element
FEATURE [App::DocumentObjectGroupPython] C_element142  label="C_element : 087"  # scripted group (container) (typed FeaturePython)
  n = 9
  ref = C_element
FEATURE [App::DocumentObjectGroupPython] N_element062  label="N_element : 034"  # scripted group (container) (typed FeaturePython)
  n = 2
  ref = N_element
FEATURE [App::DocumentObjectGroupPython] O_element123  label="O_element : 076"  # scripted group (container) (typed FeaturePython)
  n = 6
  ref = O_element
FEATURE [App::DocumentObjectGroupPython] G4_DNA_URIDINE  # scripted group (container) (typed FeaturePython)
  Dunit = g/cm3
  Dvalue = 1
  Group = -> [H_element132,C_element142,N_element062,O_element123]
  conduct = 2
  density = 1
  expand = 3
  formula = G4_DNA_URIDINE
  name = G4_DNA_URIDINE
  specific = 4
FEATURE [App::DocumentObjectGroupPython] H_element133  label="H_element : 080"  # scripted group (container) (typed FeaturePython)
  n = 11
  ref = H_element
FEATURE [App::DocumentObjectGroupPython] C_element143  label="C_element : 088"  # scripted group (container) (typed FeaturePython)
  n = 10
  ref = C_element
FEATURE [App::DocumentObjectGroupPython] N_element063  label="N_element : 035"  # scripted group (container) (typed FeaturePython)
  n = 2
  ref = N_element
FEATURE [App::DocumentObjectGroupPython] O_element124  label="O_element : 077"  # scripted group (container) (typed FeaturePython)
  n = 6
  ref = O_element
FEATURE [App::DocumentObjectGroupPython] G4_DNA_METHYLURIDINE  # scripted group (container) (typed FeaturePython)
  Dunit = g/cm3
  Dvalue = 1
  Group = -> [H_element133,C_element143,N_element063,O_element124]
  conduct = 2
  density = 1
  expand = 3
  formula = G4_DNA_METHYLURIDINE
  name = G4_DNA_METHYLURIDINE
  specific = 4
FEATURE [App::DocumentObjectGroupPython] P_element014  label="P_element : 003"  # scripted group (container) (typed FeaturePython)
  n = 1
  ref = P_element
FEATURE [App::DocumentObjectGroupPython] O_element125  label="O_element : 078"  # scripted group (container) (typed FeaturePython)
  n = 3
  ref = O_element
FEATURE [App::DocumentObjectGroupPython] G4_DNA_MONOPHOSPHATE  # scripted group (container) (typed FeaturePython)
  Dunit = g/cm3
  Dvalue = 1
  Group = -> [P_element014,O_element125]
  conduct = 2
  density = 1
  expand = 3
  formula = G4_DNA_MONOPHOSPHATE
  name = G4_DNA_MONOPHOSPHATE
  specific = 4
FEATURE [App::DocumentObjectGroupPython] H_element134  label="H_element : 081"  # scripted group (container) (typed FeaturePython)
  n = 10
  ref = H_element
FEATURE [App::DocumentObjectGroupPython] C_element144  label="C_element : 089"  # scripted group (container) (typed FeaturePython)
  n = 10
  ref = C_element
FEATURE [App::DocumentObjectGroupPython] N_element064  label="N_element : 036"  # scripted group (container) (typed FeaturePython)
  n = 5
  ref = N_element
FEATURE [App::DocumentObjectGroupPython] O_element126  label="O_element : 079"  # scripted group (container) (typed FeaturePython)
  n = 7
  ref = O_element
FEATURE [App::DocumentObjectGroupPython] P_element015  label="P_element : 004"  # scripted group (container) (typed FeaturePython)
  n = 1
  ref = P_element
FEATURE [App::DocumentObjectGroupPython] G4_DNA_A  # scripted group (container) (typed FeaturePython)
  Dunit = g/cm3
  Dvalue = 1
  Group = -> [H_element134,C_element144,N_element064,O_element126,P_element015]
  conduct = 2
  density = 1
  expand = 3
  formula = G4_DNA_A
  name = G4_DNA_A
  specific = 4
FEATURE [App::DocumentObjectGroupPython] H_element135  label="H_element : 082"  # scripted group (container) (typed FeaturePython)
  n = 10
  ref = H_element
FEATURE [App::DocumentObjectGroupPython] C_element145  label="C_element : 090"  # scripted group (container) (typed FeaturePython)
  n = 10
  ref = C_element
FEATURE [App::DocumentObjectGroupPython] N_element065  label="N_element : 037"  # scripted group (container) (typed FeaturePython)
  n = 5
  ref = N_element
FEATURE [App::DocumentObjectGroupPython] O_element127  label="O_element : 8"  # scripted group (container) (typed FeaturePython)
  n = 8
  ref = O_element
FEATURE [App::DocumentObjectGroupPython] P_element016  label="P_element : 005"  # scripted group (container) (typed FeaturePython)
  n = 1
  ref = P_element
FEATURE [App::DocumentObjectGroupPython] G4_DNA_G  # scripted group (container) (typed FeaturePython)
  Dunit = g/cm3
  Dvalue = 1
  Group = -> [H_element135,C_element145,N_element065,O_element127,P_element016]
  conduct = 2
  density = 1
  expand = 3
  formula = G4_DNA_G
  name = G4_DNA_G
  specific = 4
FEATURE [App::DocumentObjectGroupPython] H_element136  label="H_element : 083"  # scripted group (container) (typed FeaturePython)
  n = 10
  ref = H_element
FEATURE [App::DocumentObjectGroupPython] C_element146  label="C_element : 091"  # scripted group (container) (typed FeaturePython)
  n = 9
  ref = C_element
FEATURE [App::DocumentObjectGroupPython] N_element066  label="N_element : 038"  # scripted group (container) (typed FeaturePython)
  n = 3
  ref = N_element
FEATURE [App::DocumentObjectGroupPython] O_element128  label="O_element : 080"  # scripted group (container) (typed FeaturePython)
  n = 8
  ref = O_element
FEATURE [App::DocumentObjectGroupPython] P_element017  label="P_element : 006"  # scripted group (container) (typed FeaturePython)
  n = 1
  ref = P_element
FEATURE [App::DocumentObjectGroupPython] G4_DNA_C  # scripted group (container) (typed FeaturePython)
  Dunit = g/cm3
  Dvalue = 1
  Group = -> [H_element136,C_element146,N_element066,O_element128,P_element017]
  conduct = 2
  density = 1
  expand = 3
  formula = G4_DNA_C
  name = G4_DNA_C
  specific = 4
FEATURE [App::DocumentObjectGroupPython] H_element137  label="H_element : 084"  # scripted group (container) (typed FeaturePython)
  n = 9
  ref = H_element
FEATURE [App::DocumentObjectGroupPython] C_element147  label="C_element : 092"  # scripted group (container) (typed FeaturePython)
  n = 9
  ref = C_element
FEATURE [App::DocumentObjectGroupPython] N_element067  label="N_element : 039"  # scripted group (container) (typed FeaturePython)
  n = 2
  ref = N_element
FEATURE [App::DocumentObjectGroupPython] O_element129  label="O_element : 9"  # scripted group (container) (typed FeaturePython)
  n = 9
  ref = O_element
FEATURE [App::DocumentObjectGroupPython] P_element018  label="P_element : 007"  # scripted group (container) (typed FeaturePython)
  n = 1
  ref = P_element
FEATURE [App::DocumentObjectGroupPython] G4_DNA_U  # scripted group (container) (typed FeaturePython)
  Dunit = g/cm3
  Dvalue = 1
  Group = -> [H_element137,C_element147,N_element067,O_element129,P_element018]
  conduct = 2
  density = 1
  expand = 3
  formula = G4_DNA_U
  name = G4_DNA_U
  specific = 4
FEATURE [App::DocumentObjectGroupPython] H_element138  label="H_element : 085"  # scripted group (container) (typed FeaturePython)
  n = 11
  ref = H_element
FEATURE [App::DocumentObjectGroupPython] C_element148  label="C_element : 093"  # scripted group (container) (typed FeaturePython)
  n = 10
  ref = C_element
FEATURE [App::DocumentObjectGroupPython] N_element068  label="N_element : 040"  # scripted group (container) (typed FeaturePython)
  n = 2
  ref = N_element
FEATURE [App::DocumentObjectGroupPython] O_element130  label="O_element : 081"  # scripted group (container) (typed FeaturePython)
  n = 9
  ref = O_element
FEATURE [App::DocumentObjectGroupPython] P_element019  label="P_element : 008"  # scripted group (container) (typed FeaturePython)
  n = 1
  ref = P_element
FEATURE [App::DocumentObjectGroupPython] G4_DNA_MU  # scripted group (container) (typed FeaturePython)
  Dunit = g/cm3
  Dvalue = 1
  Group = -> [H_element138,C_element148,N_element068,O_element130,P_element019]
  conduct = 2
  density = 1
  expand = 3
  formula = G4_DNA_MU
  name = G4_DNA_MU
  specific = 4
FEATURE [App::DocumentObjectGroupPython] BioChemical  # scripted group (container) (typed FeaturePython)
  Group = -> [G4_CYTOSINE,G4_THYMINE,G4_URACIL,G4_DNA_ADENINE,G4_DNA_GUANINE,G4_DNA_CYTOSINE,G4_DNA_THYMINE,G4_DNA_URACIL,G4_DNA_ADENOSINE,G4_DNA_GUANOSINE,G4_DNA_CYTIDINE,G4_DNA_URIDINE,G4_DNA_METHYLURIDINE,G4_DNA_MONOPHOSPHATE,G4_DNA_A,G4_DNA_G,G4_DNA_C,G4_DNA_U,G4_DNA_MU]
FEATURE [App::DocumentObjectGroupPython] G4Materials  # scripted group (container) (typed FeaturePython)
  Group = -> [NIST,Element,HEP,Space,BioChemical]
  version = 1
FEATURE [App::DocumentObjectGroupPython] Geant4  # scripted group (container) (typed FeaturePython)
  Group = -> [G4Isotopes,G4Elements,G4Materials]
FEATURE [App::DocumentObjectGroupPython] Materials  # scripted group (container) (typed FeaturePython)
  Group = -> [Geant4]
FEATURE [Part::FeaturePython] GDMLBox_WorldBox  # WARN: FeaturePython — macro-defined, semantics opaque (R4)
  lunit = 2
  material = 5
  x = 273
  y = 273
  z = 130
FEATURE [Part::FeaturePython] GDMLBox_Box  # WARN: FeaturePython — macro-defined, semantics opaque (R4)
  Placement = pos=(20,0,0) rot=(0,0,1;0rad)
  lunit = 2
  material = 0
  x = 10
  y = 10
  z = 10
FEATURE [Part::FeaturePython] GDMLTube  # WARN: FeaturePython — macro-defined, semantics opaque (R4)
  Placement = pos=(17,-4,0) rot=(0,0,1;0rad)
  aunit = 1
  deltaphi = 90
  lunit = 2
  material = 0
  rmax = 7
  rmin = 5
  startphi = 0
  z = 7
FEATURE [App::Part] LV_Tube
  Group = -> [GDMLTube]
  Origin = -> Origin003
  SkinSurface = 0
FEATURE [App::Part] LV_Box
  Group = -> [GDMLBox_Box,LV_Tube]
  Origin = -> Origin002
  Placement = pos=(0,0,0) rot=(0,0,1;-0.523599rad)
FEATURE [Part::FeaturePython] Array  # Draft array (typed FeaturePython)
  AlwaysSyncPlacement = false
  Angle = 180
  ArrayType = 1
  Axis = (0,0,1)
  Base = -> LV_Box
  Center = (0,0,0)
  Count = 5
  ExpandArray = false
  Fuse = false
  IntervalAxis = (0,0,0)
  IntervalX = (100,0,0)
  IntervalY = (0,100,0)
  IntervalZ = (0,0,100)
  NumberCircles = 3
  NumberPolar = 5
  NumberX = 2
  NumberY = 2
  NumberZ = 1
  PlacementList = 5 placements: [(0,0,0),(0,0,0),(0,0,0),(0,0,0),(0,0,0)]
  RadialDistance = 50
  ScaleList = (5) [(1,1,1),(1,1,1),(1,1,1),(1,1,1),(1,1,1)]
  Symmetry = 1
  TangentialDistance = 25
FEATURE [App::Part] Part  label="experiment"
  Group = -> [LV_Box,Array]
  Origin = -> Origin001
FEATURE [App::Part] worldVOL
  Group = -> [GDMLBox_WorldBox,Part]
  Origin = -> Origin
